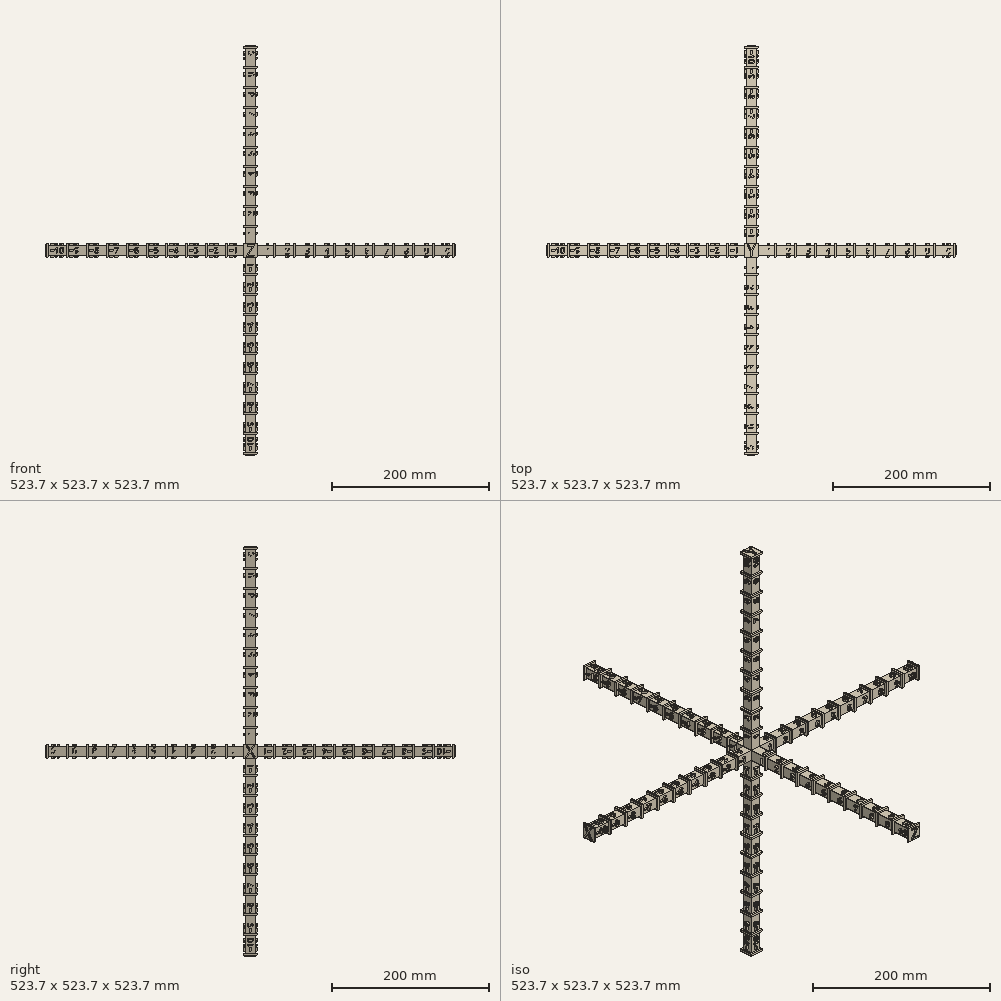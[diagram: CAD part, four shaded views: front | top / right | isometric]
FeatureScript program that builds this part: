
annotation { "Feature Type Name" : "Feature", "Feature Type Description" : "" }
export const myFeature = defineFeature(function(context is Context, id is Id, definition is map)
    precondition{}
    {
        {
            var Q0;
            Q0=qCreatedBy(makeId("Front.planeOp"),FACE);
            var sketch = newSketch(context, id + "F0", { "sketchPlane" : qUnion([Q0])});
            skLineSegment(sketch, "E0.bottom", {"start": v(-6.35, 260.35) * mm, "end": v(6.35, 260.35) * mm});
            skLineSegment(sketch, "E0.top", {"start": v(-6.35, -260.35) * mm, "end": v(6.35, -260.35) * mm});
            skLineSegment(sketch, "E0.left", {"start": v(-6.35, 260.35) * mm, "end": v(-6.35, -260.35) * mm});
            skLineSegment(sketch, "E0.right", {"start": v(6.35, 260.35) * mm, "end": v(6.35, -260.35) * mm});
            skPoint(sketch, "E0.middle", {"position": v(0, 0) * mm});
            skLineSegment(sketch, "E1.bottom", {"start": v(-260.35, 6.35) * mm, "end": v(260.35, 6.35) * mm});
            skLineSegment(sketch, "E1.top", {"start": v(-260.35, -6.35) * mm, "end": v(260.35, -6.35) * mm});
            skLineSegment(sketch, "E1.left", {"start": v(-260.35, 6.35) * mm, "end": v(-260.35, -6.35) * mm});
            skLineSegment(sketch, "E1.right", {"start": v(260.35, 6.35) * mm, "end": v(260.35, -6.35) * mm});
            skSolve(sketch);
        }
        {
            var Q0;
            Q0 = qSketchRegion(id + "F0", true);
            extrude(context, id + "F1", {"entities" : qUnion([Q0]), "endBound" : BoundingType.SYMMETRIC, "depth" : 12.7 * mm});
        }
        {
            var Q0;
            Q0=makeQuery(id+"F1.opExtrude","CAP_FACE",FACE,{"disambiguationData":[OSD([sQuery(id+"F0.wireOp",EDGE,"E0.bottom"),sQuery(id+"F0.wireOp",EDGE,"E0.top"),sQuery(id+"F0.wireOp",EDGE,"E0.left"),sQuery(id+"F0.wireOp",EDGE,"E0.right"),sQuery(id+"F0.wireOp",EDGE,"E1.bottom"),sQuery(id+"F0.wireOp",EDGE,"E1.top"),sQuery(id+"F0.wireOp",EDGE,"E1.left"),sQuery(id+"F0.wireOp",EDGE,"E1.right")])],"isStart":false});
            var sketch = newSketch(context, id + "F2", { "sketchPlane" : qUnion([Q0])});
            skLineSegment(sketch, "E2.bottom", {"start": v(-6.35, 6.35) * mm, "end": v(6.35, 6.35) * mm});
            skLineSegment(sketch, "E2.top", {"start": v(-6.35, -6.35) * mm, "end": v(6.35, -6.35) * mm});
            skLineSegment(sketch, "E2.left", {"start": v(-6.35, 6.35) * mm, "end": v(-6.35, -6.35) * mm});
            skLineSegment(sketch, "E2.right", {"start": v(6.35, 6.35) * mm, "end": v(6.35, -6.35) * mm});
            skSolve(sketch);
        }
        {
            var Q0;
            Q0 = qSketchRegion(id + "F2", true);
            extrude(context, id + "F3", {"entities" : qUnion([Q0]), "operationType" : NewBodyOperationType.ADD, "depth" : 254 * mm, "hasSecondDirection" : true, "secondDirectionOppositeDirection" : true, "secondDirectionDepth" : 266.7 * mm});
        }
        {
            var Q0;
            {var subQ0=sQuery(id+"F0.wireOp",EDGE,"E0.right");var subQ1=sQuery(id+"F0.wireOp",EDGE,"E0.top");var subQ2=sQuery(id+"F0.wireOp",EDGE,"E1.top");var subQ4=sQuery(id+"F0.wireOp",EDGE,"E0.bottom");var subQ5=sQuery(id+"F0.wireOp",EDGE,"E1.bottom");var subQ7=sQuery(id+"F0.wireOp",EDGE,"E1.right");var subQ8=makeQuery(id+"F1.opExtrude","CAP_FACE",FACE,{"disambiguationData":[OSD([subQ4,subQ1,sQuery(id+"F0.wireOp",EDGE,"E0.left"),subQ0,subQ5,subQ2,sQuery(id+"F0.wireOp",EDGE,"E1.left"),subQ7])],"isStart":false});Q0=makeQuery(id+"F3.boolean.opBoolean","SPLIT",FACE,{"disambiguationData":[TD([makeQuery(id+"F1.opExtrude","SWEPT_FACE",FACE,{"disambiguationData":[OSD([subQ7])]})])],"derivedFrom":subQ8});}
            var sketch = newSketch(context, id + "F4", { "sketchPlane" : qUnion([Q0])});
            skLineSegment(sketch, "E3.bottom", {"start": v(29.21, 6.35) * mm, "end": v(31.75, 6.35) * mm});
            skLineSegment(sketch, "E3.top", {"start": v(29.21, -6.35) * mm, "end": v(31.75, -6.35) * mm});
            skLineSegment(sketch, "E3.left", {"start": v(29.21, 6.35) * mm, "end": v(29.21, -6.35) * mm});
            skLineSegment(sketch, "E3.right", {"start": v(31.75, 6.35) * mm, "end": v(31.75, -6.35) * mm});
            skLineSegment(sketch, "E4.1.0.0", {"start": v(54.61, 6.35) * mm, "end": v(54.61, -6.35) * mm});
            skLineSegment(sketch, "E4.1.0.1", {"start": v(54.61, 6.35) * mm, "end": v(57.15, 6.35) * mm});
            skLineSegment(sketch, "E4.1.0.2", {"start": v(57.15, 6.35) * mm, "end": v(57.15, -6.35) * mm});
            skLineSegment(sketch, "E4.1.0.3", {"start": v(54.61, -6.35) * mm, "end": v(57.15, -6.35) * mm});
            skLineSegment(sketch, "E4.2.0.0", {"start": v(80.01, 6.35) * mm, "end": v(80.01, -6.35) * mm});
            skLineSegment(sketch, "E4.2.0.1", {"start": v(80.01, 6.35) * mm, "end": v(82.55, 6.35) * mm});
            skLineSegment(sketch, "E4.2.0.2", {"start": v(82.55, 6.35) * mm, "end": v(82.55, -6.35) * mm});
            skLineSegment(sketch, "E4.2.0.3", {"start": v(80.01, -6.35) * mm, "end": v(82.55, -6.35) * mm});
            skLineSegment(sketch, "E4.3.0.0", {"start": v(105.41, 6.35) * mm, "end": v(105.41, -6.35) * mm});
            skLineSegment(sketch, "E4.3.0.1", {"start": v(105.41, 6.35) * mm, "end": v(107.95, 6.35) * mm});
            skLineSegment(sketch, "E4.3.0.2", {"start": v(107.95, 6.35) * mm, "end": v(107.95, -6.35) * mm});
            skLineSegment(sketch, "E4.3.0.3", {"start": v(105.41, -6.35) * mm, "end": v(107.95, -6.35) * mm});
            skLineSegment(sketch, "E4.4.0.0", {"start": v(130.81, 6.35) * mm, "end": v(130.81, -6.35) * mm});
            skLineSegment(sketch, "E4.4.0.1", {"start": v(130.81, 6.35) * mm, "end": v(133.35, 6.35) * mm});
            skLineSegment(sketch, "E4.4.0.2", {"start": v(133.35, 6.35) * mm, "end": v(133.35, -6.35) * mm});
            skLineSegment(sketch, "E4.4.0.3", {"start": v(130.81, -6.35) * mm, "end": v(133.35, -6.35) * mm});
            skLineSegment(sketch, "E4.5.0.0", {"start": v(156.21, 6.35) * mm, "end": v(156.21, -6.35) * mm});
            skLineSegment(sketch, "E4.5.0.1", {"start": v(156.21, 6.35) * mm, "end": v(158.75, 6.35) * mm});
            skLineSegment(sketch, "E4.5.0.2", {"start": v(158.75, 6.35) * mm, "end": v(158.75, -6.35) * mm});
            skLineSegment(sketch, "E4.5.0.3", {"start": v(156.21, -6.35) * mm, "end": v(158.75, -6.35) * mm});
            skLineSegment(sketch, "E4.6.0.0", {"start": v(181.61, 6.35) * mm, "end": v(181.61, -6.35) * mm});
            skLineSegment(sketch, "E4.6.0.1", {"start": v(181.61, 6.35) * mm, "end": v(184.15, 6.35) * mm});
            skLineSegment(sketch, "E4.6.0.2", {"start": v(184.15, 6.35) * mm, "end": v(184.15, -6.35) * mm});
            skLineSegment(sketch, "E4.6.0.3", {"start": v(181.61, -6.35) * mm, "end": v(184.15, -6.35) * mm});
            skLineSegment(sketch, "E4.7.0.0", {"start": v(207.01, 6.35) * mm, "end": v(207.01, -6.35) * mm});
            skLineSegment(sketch, "E4.7.0.1", {"start": v(207.01, 6.35) * mm, "end": v(209.55, 6.35) * mm});
            skLineSegment(sketch, "E4.7.0.2", {"start": v(209.55, 6.35) * mm, "end": v(209.55, -6.35) * mm});
            skLineSegment(sketch, "E4.7.0.3", {"start": v(207.01, -6.35) * mm, "end": v(209.55, -6.35) * mm});
            skLineSegment(sketch, "E4.8.0.0", {"start": v(232.41, 6.35) * mm, "end": v(232.41, -6.35) * mm});
            skLineSegment(sketch, "E4.8.0.1", {"start": v(232.41, 6.35) * mm, "end": v(234.95, 6.35) * mm});
            skLineSegment(sketch, "E4.8.0.2", {"start": v(234.95, 6.35) * mm, "end": v(234.95, -6.35) * mm});
            skLineSegment(sketch, "E4.8.0.3", {"start": v(232.41, -6.35) * mm, "end": v(234.95, -6.35) * mm});
            skLineSegment(sketch, "E4.9.0.0", {"start": v(257.81, 6.35) * mm, "end": v(257.81, -6.35) * mm});
            skLineSegment(sketch, "E4.9.0.1", {"start": v(257.81, 6.35) * mm, "end": v(260.35, 6.35) * mm});
            skLineSegment(sketch, "E4.9.0.2", {"start": v(260.35, 6.35) * mm, "end": v(260.35, -6.35) * mm});
            skLineSegment(sketch, "E4.9.0.3", {"start": v(257.81, -6.35) * mm, "end": v(260.35, -6.35) * mm});
            skLineSegment(sketch, "E4.direction1", {"start": v(29.21, -6.35) * mm, "end": v(54.61, -6.35) * mm, "construction": true});
            skSolve(sketch);
        }
        {
            var Q0;
            Q0 = qSketchRegion(id + "F4", true);
            extrude(context, id + "F5", {"entities" : qUnion([Q0]), "depth" : 2.54 * mm});
        }
        {
            var Q0;
            {var subQ0=sQuery(id+"F0.wireOp",EDGE,"E1.bottom");Q0=makeQuery(id+"F5.boolean.opBoolean","MERGE",FACE,{"derivedFrom":[makeQuery(id+"F1.opExtrude","SWEPT_FACE",FACE,{"disambiguationData":[OSD([subQ0]),TDD([makeQuery(id+"F0.imprint","IMPRINT",EDGE,{"disambiguationData":[TD([[makeQuery(id+"F0.imprint","INTERSECT",VERTEX,{"derivedFrom":[subQ0,sQuery(id+"F0.wireOp",EDGE,"E1.right")]}),1.0]])],"derivedFrom":subQ0})])]}),makeQuery(id+"F5.opExtrude","SWEPT_FACE",FACE,{"disambiguationData":[OSD([sQuery(id+"F4.wireOp",EDGE,"E3.bottom")])]}),makeQuery(id+"F5.opExtrude","SWEPT_FACE",FACE,{"disambiguationData":[OSD([sQuery(id+"F4.wireOp",EDGE,"E4.1.0.1")])]}),makeQuery(id+"F5.opExtrude","SWEPT_FACE",FACE,{"disambiguationData":[OSD([sQuery(id+"F4.wireOp",EDGE,"E4.2.0.1")])]}),makeQuery(id+"F5.opExtrude","SWEPT_FACE",FACE,{"disambiguationData":[OSD([sQuery(id+"F4.wireOp",EDGE,"E4.3.0.1")])]}),makeQuery(id+"F5.opExtrude","SWEPT_FACE",FACE,{"disambiguationData":[OSD([sQuery(id+"F4.wireOp",EDGE,"E4.4.0.1")])]}),makeQuery(id+"F5.opExtrude","SWEPT_FACE",FACE,{"disambiguationData":[OSD([sQuery(id+"F4.wireOp",EDGE,"E4.5.0.1")])]}),makeQuery(id+"F5.opExtrude","SWEPT_FACE",FACE,{"disambiguationData":[OSD([sQuery(id+"F4.wireOp",EDGE,"E4.6.0.1")])]}),makeQuery(id+"F5.opExtrude","SWEPT_FACE",FACE,{"disambiguationData":[OSD([sQuery(id+"F4.wireOp",EDGE,"E4.7.0.1")])]}),makeQuery(id+"F5.opExtrude","SWEPT_FACE",FACE,{"disambiguationData":[OSD([sQuery(id+"F4.wireOp",EDGE,"E4.8.0.1")])]}),makeQuery(id+"F5.opExtrude","SWEPT_FACE",FACE,{"disambiguationData":[OSD([sQuery(id+"F4.wireOp",EDGE,"E4.9.0.1")])]})]});}
            var sketch = newSketch(context, id + "F6", { "sketchPlane" : qUnion([Q0])});
            skLineSegment(sketch, "E5.bottom", {"start": v(29.21, -8.9) * mm, "end": v(31.75, -8.9) * mm});
            skLineSegment(sketch, "E5.top", {"start": v(29.21, 6.35) * mm, "end": v(31.75, 6.35) * mm});
            skLineSegment(sketch, "E5.left", {"start": v(29.21, -8.9) * mm, "end": v(29.21, 6.35) * mm});
            skLineSegment(sketch, "E5.right", {"start": v(31.75, -8.9) * mm, "end": v(31.75, 6.35) * mm});
            skLineSegment(sketch, "E6.1.0.0", {"start": v(57.15, -8.9) * mm, "end": v(57.15, 6.35) * mm});
            skLineSegment(sketch, "E6.1.0.1", {"start": v(54.61, -8.9) * mm, "end": v(54.61, 6.35) * mm});
            skLineSegment(sketch, "E6.1.0.2", {"start": v(54.61, -8.9) * mm, "end": v(57.15, -8.9) * mm});
            skLineSegment(sketch, "E6.1.0.3", {"start": v(54.61, 6.35) * mm, "end": v(57.15, 6.35) * mm});
            skLineSegment(sketch, "E6.2.0.0", {"start": v(82.55, -8.9) * mm, "end": v(82.55, 6.35) * mm});
            skLineSegment(sketch, "E6.2.0.1", {"start": v(80.01, -8.9) * mm, "end": v(80.01, 6.35) * mm});
            skLineSegment(sketch, "E6.2.0.2", {"start": v(80.01, -8.9) * mm, "end": v(82.55, -8.9) * mm});
            skLineSegment(sketch, "E6.2.0.3", {"start": v(80.01, 6.35) * mm, "end": v(82.55, 6.35) * mm});
            skLineSegment(sketch, "E6.3.0.0", {"start": v(107.95, -8.9) * mm, "end": v(107.95, 6.35) * mm});
            skLineSegment(sketch, "E6.3.0.1", {"start": v(105.41, -8.9) * mm, "end": v(105.41, 6.35) * mm});
            skLineSegment(sketch, "E6.3.0.2", {"start": v(105.41, -8.9) * mm, "end": v(107.95, -8.9) * mm});
            skLineSegment(sketch, "E6.3.0.3", {"start": v(105.41, 6.35) * mm, "end": v(107.95, 6.35) * mm});
            skLineSegment(sketch, "E6.4.0.0", {"start": v(133.35, -8.9) * mm, "end": v(133.35, 6.35) * mm});
            skLineSegment(sketch, "E6.4.0.1", {"start": v(130.81, -8.9) * mm, "end": v(130.81, 6.35) * mm});
            skLineSegment(sketch, "E6.4.0.2", {"start": v(130.81, -8.9) * mm, "end": v(133.35, -8.9) * mm});
            skLineSegment(sketch, "E6.4.0.3", {"start": v(130.81, 6.35) * mm, "end": v(133.35, 6.35) * mm});
            skLineSegment(sketch, "E6.5.0.0", {"start": v(158.75, -8.9) * mm, "end": v(158.75, 6.35) * mm});
            skLineSegment(sketch, "E6.5.0.1", {"start": v(156.21, -8.9) * mm, "end": v(156.21, 6.35) * mm});
            skLineSegment(sketch, "E6.5.0.2", {"start": v(156.21, -8.9) * mm, "end": v(158.75, -8.9) * mm});
            skLineSegment(sketch, "E6.5.0.3", {"start": v(156.21, 6.35) * mm, "end": v(158.75, 6.35) * mm});
            skLineSegment(sketch, "E6.6.0.0", {"start": v(184.15, -8.9) * mm, "end": v(184.15, 6.35) * mm});
            skLineSegment(sketch, "E6.6.0.1", {"start": v(181.61, -8.9) * mm, "end": v(181.61, 6.35) * mm});
            skLineSegment(sketch, "E6.6.0.2", {"start": v(181.61, -8.9) * mm, "end": v(184.15, -8.9) * mm});
            skLineSegment(sketch, "E6.6.0.3", {"start": v(181.61, 6.35) * mm, "end": v(184.15, 6.35) * mm});
            skLineSegment(sketch, "E6.7.0.0", {"start": v(209.55, -8.9) * mm, "end": v(209.55, 6.35) * mm});
            skLineSegment(sketch, "E6.7.0.1", {"start": v(207.01, -8.9) * mm, "end": v(207.01, 6.35) * mm});
            skLineSegment(sketch, "E6.7.0.2", {"start": v(207.01, -8.9) * mm, "end": v(209.55, -8.9) * mm});
            skLineSegment(sketch, "E6.7.0.3", {"start": v(207.01, 6.35) * mm, "end": v(209.55, 6.35) * mm});
            skLineSegment(sketch, "E6.8.0.0", {"start": v(234.95, -8.9) * mm, "end": v(234.95, 6.35) * mm});
            skLineSegment(sketch, "E6.8.0.1", {"start": v(232.41, -8.9) * mm, "end": v(232.41, 6.35) * mm});
            skLineSegment(sketch, "E6.8.0.2", {"start": v(232.41, -8.9) * mm, "end": v(234.95, -8.9) * mm});
            skLineSegment(sketch, "E6.8.0.3", {"start": v(232.41, 6.35) * mm, "end": v(234.95, 6.35) * mm});
            skLineSegment(sketch, "E6.9.0.0", {"start": v(260.35, -8.9) * mm, "end": v(260.35, 6.35) * mm});
            skLineSegment(sketch, "E6.9.0.1", {"start": v(257.81, -8.9) * mm, "end": v(257.81, 6.35) * mm});
            skLineSegment(sketch, "E6.9.0.2", {"start": v(257.81, -8.9) * mm, "end": v(260.35, -8.9) * mm});
            skLineSegment(sketch, "E6.9.0.3", {"start": v(257.81, 6.35) * mm, "end": v(260.35, 6.35) * mm});
            skLineSegment(sketch, "E6.direction1", {"start": v(31.75, -8.9) * mm, "end": v(57.15, -8.9) * mm, "construction": true});
            skSolve(sketch);
        }
        {
            var Q0;
            Q0 = qSketchRegion(id + "F6", true);
            extrude(context, id + "F7", {"entities" : qUnion([Q0]), "depth" : 2.54 * mm});
        }
        {
            var Q0;
            {var subQ0=sQuery(id+"F0.wireOp",EDGE,"E1.right");var subQ1=sQuery(id+"F0.wireOp",EDGE,"E1.bottom");var subQ2=sQuery(id+"F0.wireOp",EDGE,"E0.right");var subQ4=sQuery(id+"F0.wireOp",EDGE,"E0.top");var subQ5=sQuery(id+"F0.wireOp",EDGE,"E1.top");var subQ7=sQuery(id+"F0.wireOp",EDGE,"E0.bottom");var subQ8=makeQuery(id+"F1.opExtrude","CAP_FACE",FACE,{"disambiguationData":[OSD([subQ7,subQ4,sQuery(id+"F0.wireOp",EDGE,"E0.left"),subQ2,subQ1,subQ5,sQuery(id+"F0.wireOp",EDGE,"E1.left"),subQ0])],"isStart":true});Q0=makeQuery(id+"F7.boolean.opBoolean","MERGE",FACE,{"derivedFrom":[makeQuery(id+"F3.boolean.opBoolean","SPLIT",FACE,{"disambiguationData":[TD([makeQuery(id+"F1.opExtrude","SWEPT_FACE",FACE,{"disambiguationData":[OSD([subQ0])]})])],"derivedFrom":subQ8}),makeQuery(id+"F7.opExtrude","SWEPT_FACE",FACE,{"disambiguationData":[OSD([sQuery(id+"F6.wireOp",EDGE,"E5.top")])]}),makeQuery(id+"F7.opExtrude","SWEPT_FACE",FACE,{"disambiguationData":[OSD([sQuery(id+"F6.wireOp",EDGE,"E6.1.0.3")])]}),makeQuery(id+"F7.opExtrude","SWEPT_FACE",FACE,{"disambiguationData":[OSD([sQuery(id+"F6.wireOp",EDGE,"E6.2.0.3")])]}),makeQuery(id+"F7.opExtrude","SWEPT_FACE",FACE,{"disambiguationData":[OSD([sQuery(id+"F6.wireOp",EDGE,"E6.3.0.3")])]}),makeQuery(id+"F7.opExtrude","SWEPT_FACE",FACE,{"disambiguationData":[OSD([sQuery(id+"F6.wireOp",EDGE,"E6.4.0.3")])]}),makeQuery(id+"F7.opExtrude","SWEPT_FACE",FACE,{"disambiguationData":[OSD([sQuery(id+"F6.wireOp",EDGE,"E6.5.0.3")])]}),makeQuery(id+"F7.opExtrude","SWEPT_FACE",FACE,{"disambiguationData":[OSD([sQuery(id+"F6.wireOp",EDGE,"E6.6.0.3")])]}),makeQuery(id+"F7.opExtrude","SWEPT_FACE",FACE,{"disambiguationData":[OSD([sQuery(id+"F6.wireOp",EDGE,"E6.7.0.3")])]}),makeQuery(id+"F7.opExtrude","SWEPT_FACE",FACE,{"disambiguationData":[OSD([sQuery(id+"F6.wireOp",EDGE,"E6.8.0.3")])]}),makeQuery(id+"F7.opExtrude","SWEPT_FACE",FACE,{"disambiguationData":[OSD([sQuery(id+"F6.wireOp",EDGE,"E6.9.0.3")])]})]});}
            var sketch = newSketch(context, id + "F8", { "sketchPlane" : qUnion([Q0])});
            skLineSegment(sketch, "E7.bottom", {"start": v(-29.21, 8.9) * mm, "end": v(-31.75, 8.9) * mm});
            skLineSegment(sketch, "E7.top", {"start": v(-29.21, -6.35) * mm, "end": v(-31.75, -6.35) * mm});
            skLineSegment(sketch, "E7.left", {"start": v(-29.21, 8.9) * mm, "end": v(-29.21, -6.35) * mm});
            skLineSegment(sketch, "E7.right", {"start": v(-31.75, 8.9) * mm, "end": v(-31.75, -6.35) * mm});
            skLineSegment(sketch, "E8.1.0.0", {"start": v(-54.61, 8.9) * mm, "end": v(-54.61, -6.35) * mm});
            skLineSegment(sketch, "E8.1.0.1", {"start": v(-54.61, -6.35) * mm, "end": v(-57.15, -6.35) * mm});
            skLineSegment(sketch, "E8.1.0.2", {"start": v(-57.15, 8.9) * mm, "end": v(-57.15, -6.35) * mm});
            skLineSegment(sketch, "E8.1.0.3", {"start": v(-54.61, 8.9) * mm, "end": v(-57.15, 8.9) * mm});
            skLineSegment(sketch, "E8.2.0.0", {"start": v(-80.01, 8.9) * mm, "end": v(-80.01, -6.35) * mm});
            skLineSegment(sketch, "E8.2.0.1", {"start": v(-80.01, -6.35) * mm, "end": v(-82.55, -6.35) * mm});
            skLineSegment(sketch, "E8.2.0.2", {"start": v(-82.55, 8.9) * mm, "end": v(-82.55, -6.35) * mm});
            skLineSegment(sketch, "E8.2.0.3", {"start": v(-80.01, 8.9) * mm, "end": v(-82.55, 8.9) * mm});
            skLineSegment(sketch, "E8.3.0.0", {"start": v(-105.41, 8.9) * mm, "end": v(-105.41, -6.35) * mm});
            skLineSegment(sketch, "E8.3.0.1", {"start": v(-105.41, -6.35) * mm, "end": v(-107.95, -6.35) * mm});
            skLineSegment(sketch, "E8.3.0.2", {"start": v(-107.95, 8.9) * mm, "end": v(-107.95, -6.35) * mm});
            skLineSegment(sketch, "E8.3.0.3", {"start": v(-105.41, 8.9) * mm, "end": v(-107.95, 8.9) * mm});
            skLineSegment(sketch, "E8.4.0.0", {"start": v(-130.81, 8.9) * mm, "end": v(-130.81, -6.35) * mm});
            skLineSegment(sketch, "E8.4.0.1", {"start": v(-130.81, -6.35) * mm, "end": v(-133.35, -6.35) * mm});
            skLineSegment(sketch, "E8.4.0.2", {"start": v(-133.35, 8.9) * mm, "end": v(-133.35, -6.35) * mm});
            skLineSegment(sketch, "E8.4.0.3", {"start": v(-130.81, 8.9) * mm, "end": v(-133.35, 8.9) * mm});
            skLineSegment(sketch, "E8.5.0.0", {"start": v(-156.21, 8.9) * mm, "end": v(-156.21, -6.35) * mm});
            skLineSegment(sketch, "E8.5.0.1", {"start": v(-156.21, -6.35) * mm, "end": v(-158.75, -6.35) * mm});
            skLineSegment(sketch, "E8.5.0.2", {"start": v(-158.75, 8.9) * mm, "end": v(-158.75, -6.35) * mm});
            skLineSegment(sketch, "E8.5.0.3", {"start": v(-156.21, 8.9) * mm, "end": v(-158.75, 8.9) * mm});
            skLineSegment(sketch, "E8.6.0.0", {"start": v(-181.61, 8.9) * mm, "end": v(-181.61, -6.35) * mm});
            skLineSegment(sketch, "E8.6.0.1", {"start": v(-181.61, -6.35) * mm, "end": v(-184.15, -6.35) * mm});
            skLineSegment(sketch, "E8.6.0.2", {"start": v(-184.15, 8.9) * mm, "end": v(-184.15, -6.35) * mm});
            skLineSegment(sketch, "E8.6.0.3", {"start": v(-181.61, 8.9) * mm, "end": v(-184.15, 8.9) * mm});
            skLineSegment(sketch, "E8.7.0.0", {"start": v(-207.01, 8.9) * mm, "end": v(-207.01, -6.35) * mm});
            skLineSegment(sketch, "E8.7.0.1", {"start": v(-207.01, -6.35) * mm, "end": v(-209.55, -6.35) * mm});
            skLineSegment(sketch, "E8.7.0.2", {"start": v(-209.55, 8.9) * mm, "end": v(-209.55, -6.35) * mm});
            skLineSegment(sketch, "E8.7.0.3", {"start": v(-207.01, 8.9) * mm, "end": v(-209.55, 8.9) * mm});
            skLineSegment(sketch, "E8.8.0.0", {"start": v(-232.41, 8.9) * mm, "end": v(-232.41, -6.35) * mm});
            skLineSegment(sketch, "E8.8.0.1", {"start": v(-232.41, -6.35) * mm, "end": v(-234.95, -6.35) * mm});
            skLineSegment(sketch, "E8.8.0.2", {"start": v(-234.95, 8.9) * mm, "end": v(-234.95, -6.35) * mm});
            skLineSegment(sketch, "E8.8.0.3", {"start": v(-232.41, 8.9) * mm, "end": v(-234.95, 8.9) * mm});
            skLineSegment(sketch, "E8.9.0.0", {"start": v(-257.81, 8.9) * mm, "end": v(-257.81, -6.35) * mm});
            skLineSegment(sketch, "E8.9.0.1", {"start": v(-257.81, -6.35) * mm, "end": v(-260.35, -6.35) * mm});
            skLineSegment(sketch, "E8.9.0.2", {"start": v(-260.35, 8.9) * mm, "end": v(-260.35, -6.35) * mm});
            skLineSegment(sketch, "E8.9.0.3", {"start": v(-257.81, 8.9) * mm, "end": v(-260.35, 8.9) * mm});
            skLineSegment(sketch, "E8.direction1", {"start": v(-29.21, -6.35) * mm, "end": v(-54.61, -6.35) * mm, "construction": true});
            skSolve(sketch);
        }
        {
            var Q0;
            Q0 = qSketchRegion(id + "F8", true);
            extrude(context, id + "F9", {"entities" : qUnion([Q0]), "depth" : 2.54 * mm});
        }
        {
            var Q0;
            {var subQ0=sQuery(id+"F0.wireOp",EDGE,"E1.top");Q0=makeQuery(id+"F9.boolean.opBoolean","MERGE",FACE,{"derivedFrom":[makeQuery(id+"F5.boolean.opBoolean","MERGE",FACE,{"derivedFrom":[makeQuery(id+"F1.opExtrude","SWEPT_FACE",FACE,{"disambiguationData":[OSD([subQ0]),TDD([makeQuery(id+"F0.imprint","IMPRINT",EDGE,{"disambiguationData":[TD([[makeQuery(id+"F0.imprint","INTERSECT",VERTEX,{"derivedFrom":[subQ0,sQuery(id+"F0.wireOp",EDGE,"E1.right")]}),1.0]])],"derivedFrom":subQ0})])]}),makeQuery(id+"F5.opExtrude","SWEPT_FACE",FACE,{"disambiguationData":[OSD([sQuery(id+"F4.wireOp",EDGE,"E3.top")])]}),makeQuery(id+"F5.opExtrude","SWEPT_FACE",FACE,{"disambiguationData":[OSD([sQuery(id+"F4.wireOp",EDGE,"E4.1.0.3")])]}),makeQuery(id+"F5.opExtrude","SWEPT_FACE",FACE,{"disambiguationData":[OSD([sQuery(id+"F4.wireOp",EDGE,"E4.2.0.3")])]}),makeQuery(id+"F5.opExtrude","SWEPT_FACE",FACE,{"disambiguationData":[OSD([sQuery(id+"F4.wireOp",EDGE,"E4.3.0.3")])]}),makeQuery(id+"F5.opExtrude","SWEPT_FACE",FACE,{"disambiguationData":[OSD([sQuery(id+"F4.wireOp",EDGE,"E4.4.0.3")])]}),makeQuery(id+"F5.opExtrude","SWEPT_FACE",FACE,{"disambiguationData":[OSD([sQuery(id+"F4.wireOp",EDGE,"E4.5.0.3")])]}),makeQuery(id+"F5.opExtrude","SWEPT_FACE",FACE,{"disambiguationData":[OSD([sQuery(id+"F4.wireOp",EDGE,"E4.6.0.3")])]}),makeQuery(id+"F5.opExtrude","SWEPT_FACE",FACE,{"disambiguationData":[OSD([sQuery(id+"F4.wireOp",EDGE,"E4.7.0.3")])]}),makeQuery(id+"F5.opExtrude","SWEPT_FACE",FACE,{"disambiguationData":[OSD([sQuery(id+"F4.wireOp",EDGE,"E4.8.0.3")])]}),makeQuery(id+"F5.opExtrude","SWEPT_FACE",FACE,{"disambiguationData":[OSD([sQuery(id+"F4.wireOp",EDGE,"E4.9.0.3")])]})]}),makeQuery(id+"F9.opExtrude","SWEPT_FACE",FACE,{"disambiguationData":[OSD([sQuery(id+"F8.wireOp",EDGE,"E7.top")])]}),makeQuery(id+"F9.opExtrude","SWEPT_FACE",FACE,{"disambiguationData":[OSD([sQuery(id+"F8.wireOp",EDGE,"E8.1.0.1")])]}),makeQuery(id+"F9.opExtrude","SWEPT_FACE",FACE,{"disambiguationData":[OSD([sQuery(id+"F8.wireOp",EDGE,"E8.2.0.1")])]}),makeQuery(id+"F9.opExtrude","SWEPT_FACE",FACE,{"disambiguationData":[OSD([sQuery(id+"F8.wireOp",EDGE,"E8.3.0.1")])]}),makeQuery(id+"F9.opExtrude","SWEPT_FACE",FACE,{"disambiguationData":[OSD([sQuery(id+"F8.wireOp",EDGE,"E8.4.0.1")])]}),makeQuery(id+"F9.opExtrude","SWEPT_FACE",FACE,{"disambiguationData":[OSD([sQuery(id+"F8.wireOp",EDGE,"E8.5.0.1")])]}),makeQuery(id+"F9.opExtrude","SWEPT_FACE",FACE,{"disambiguationData":[OSD([sQuery(id+"F8.wireOp",EDGE,"E8.6.0.1")])]}),makeQuery(id+"F9.opExtrude","SWEPT_FACE",FACE,{"disambiguationData":[OSD([sQuery(id+"F8.wireOp",EDGE,"E8.7.0.1")])]}),makeQuery(id+"F9.opExtrude","SWEPT_FACE",FACE,{"disambiguationData":[OSD([sQuery(id+"F8.wireOp",EDGE,"E8.8.0.1")])]}),makeQuery(id+"F9.opExtrude","SWEPT_FACE",FACE,{"disambiguationData":[OSD([sQuery(id+"F8.wireOp",EDGE,"E8.9.0.1")])]})]});}
            var sketch = newSketch(context, id + "F10", { "sketchPlane" : qUnion([Q0])});
            skLineSegment(sketch, "E9.bottom", {"start": v(29.21, -8.9) * mm, "end": v(31.75, -8.9) * mm});
            skLineSegment(sketch, "E9.top", {"start": v(29.21, 8.9) * mm, "end": v(31.75, 8.9) * mm});
            skLineSegment(sketch, "E9.left", {"start": v(29.21, -8.9) * mm, "end": v(29.21, 8.9) * mm});
            skLineSegment(sketch, "E9.right", {"start": v(31.75, -8.9) * mm, "end": v(31.75, 8.9) * mm});
            skLineSegment(sketch, "E10.1.0.0", {"start": v(54.61, -8.9) * mm, "end": v(54.61, 8.9) * mm});
            skLineSegment(sketch, "E10.1.0.1", {"start": v(54.61, 8.9) * mm, "end": v(57.15, 8.9) * mm});
            skLineSegment(sketch, "E10.1.0.2", {"start": v(57.15, -8.9) * mm, "end": v(57.15, 8.9) * mm});
            skLineSegment(sketch, "E10.1.0.3", {"start": v(54.61, -8.9) * mm, "end": v(57.15, -8.9) * mm});
            skLineSegment(sketch, "E10.2.0.0", {"start": v(80.01, -8.9) * mm, "end": v(80.01, 8.9) * mm});
            skLineSegment(sketch, "E10.2.0.1", {"start": v(80.01, 8.9) * mm, "end": v(82.55, 8.9) * mm});
            skLineSegment(sketch, "E10.2.0.2", {"start": v(82.55, -8.9) * mm, "end": v(82.55, 8.9) * mm});
            skLineSegment(sketch, "E10.2.0.3", {"start": v(80.01, -8.9) * mm, "end": v(82.55, -8.9) * mm});
            skLineSegment(sketch, "E10.3.0.0", {"start": v(105.41, -8.9) * mm, "end": v(105.41, 8.9) * mm});
            skLineSegment(sketch, "E10.3.0.1", {"start": v(105.41, 8.9) * mm, "end": v(107.95, 8.9) * mm});
            skLineSegment(sketch, "E10.3.0.2", {"start": v(107.95, -8.9) * mm, "end": v(107.95, 8.9) * mm});
            skLineSegment(sketch, "E10.3.0.3", {"start": v(105.41, -8.9) * mm, "end": v(107.95, -8.9) * mm});
            skLineSegment(sketch, "E10.4.0.0", {"start": v(130.81, -8.9) * mm, "end": v(130.81, 8.9) * mm});
            skLineSegment(sketch, "E10.4.0.1", {"start": v(130.81, 8.9) * mm, "end": v(133.35, 8.9) * mm});
            skLineSegment(sketch, "E10.4.0.2", {"start": v(133.35, -8.9) * mm, "end": v(133.35, 8.9) * mm});
            skLineSegment(sketch, "E10.4.0.3", {"start": v(130.81, -8.9) * mm, "end": v(133.35, -8.9) * mm});
            skLineSegment(sketch, "E10.5.0.0", {"start": v(156.21, -8.9) * mm, "end": v(156.21, 8.9) * mm});
            skLineSegment(sketch, "E10.5.0.1", {"start": v(156.21, 8.9) * mm, "end": v(158.75, 8.9) * mm});
            skLineSegment(sketch, "E10.5.0.2", {"start": v(158.75, -8.9) * mm, "end": v(158.75, 8.9) * mm});
            skLineSegment(sketch, "E10.5.0.3", {"start": v(156.21, -8.9) * mm, "end": v(158.75, -8.9) * mm});
            skLineSegment(sketch, "E10.6.0.0", {"start": v(181.61, -8.9) * mm, "end": v(181.61, 8.9) * mm});
            skLineSegment(sketch, "E10.6.0.1", {"start": v(181.61, 8.9) * mm, "end": v(184.15, 8.9) * mm});
            skLineSegment(sketch, "E10.6.0.2", {"start": v(184.15, -8.9) * mm, "end": v(184.15, 8.9) * mm});
            skLineSegment(sketch, "E10.6.0.3", {"start": v(181.61, -8.9) * mm, "end": v(184.15, -8.9) * mm});
            skLineSegment(sketch, "E10.7.0.0", {"start": v(207.01, -8.9) * mm, "end": v(207.01, 8.9) * mm});
            skLineSegment(sketch, "E10.7.0.1", {"start": v(207.01, 8.9) * mm, "end": v(209.55, 8.9) * mm});
            skLineSegment(sketch, "E10.7.0.2", {"start": v(209.55, -8.9) * mm, "end": v(209.55, 8.9) * mm});
            skLineSegment(sketch, "E10.7.0.3", {"start": v(207.01, -8.9) * mm, "end": v(209.55, -8.9) * mm});
            skLineSegment(sketch, "E10.8.0.0", {"start": v(232.41, -8.9) * mm, "end": v(232.41, 8.9) * mm});
            skLineSegment(sketch, "E10.8.0.1", {"start": v(232.41, 8.9) * mm, "end": v(234.95, 8.9) * mm});
            skLineSegment(sketch, "E10.8.0.2", {"start": v(234.95, -8.9) * mm, "end": v(234.95, 8.9) * mm});
            skLineSegment(sketch, "E10.8.0.3", {"start": v(232.41, -8.9) * mm, "end": v(234.95, -8.9) * mm});
            skLineSegment(sketch, "E10.9.0.0", {"start": v(257.81, -8.9) * mm, "end": v(257.81, 8.9) * mm});
            skLineSegment(sketch, "E10.9.0.1", {"start": v(257.81, 8.9) * mm, "end": v(260.35, 8.9) * mm});
            skLineSegment(sketch, "E10.9.0.2", {"start": v(260.35, -8.9) * mm, "end": v(260.35, 8.9) * mm});
            skLineSegment(sketch, "E10.9.0.3", {"start": v(257.81, -8.9) * mm, "end": v(260.35, -8.9) * mm});
            skLineSegment(sketch, "E10.direction1", {"start": v(29.21, -8.9) * mm, "end": v(54.61, -8.9) * mm, "construction": true});
            skSolve(sketch);
        }
        {
            var Q0;
            Q0 = qSketchRegion(id + "F10", true);
            extrude(context, id + "F11", {"entities" : qUnion([Q0]), "depth" : 2.54 * mm});
        }
        {
            var Q0;
            Q0=qCreatedBy(makeId("Front.planeOp"),FACE);
            var sketch = newSketch(context, id + "F12", { "sketchPlane" : qUnion([Q0])});
            skLineSegment(sketch, "E11", {"start": v(0, 259.8) * mm, "end": v(0, -262.33) * mm});
            skSolve(sketch);
        }
        {
            var Q0;
            Q0=qCreatedBy(makeId("Top.planeOp"),FACE);
            var sketch = newSketch(context, id + "F13", { "sketchPlane" : qUnion([Q0])});
            skLineSegment(sketch, "E12", {"start": v(-260.75, 0) * mm, "end": v(260.1, 0) * mm});
            skSolve(sketch);
        }
        {
            var Q0;
            Q0=qCreatedBy(makeId("Top.planeOp"),FACE);
            var sketch = newSketch(context, id + "F14", { "sketchPlane" : qUnion([Q0])});
            skLineSegment(sketch, "E13", {"start": v(0, -260.56) * mm, "end": v(0, 260.69) * mm});
            skSolve(sketch);
        }
        {
            var Q0;
            Q0=makeQuery(id+"F5.opExtrude","SWEPT_BODY",BODY,{"disambiguationData":[OSD([sQuery(id+"F4.wireOp",EDGE,"E3.bottom"),sQuery(id+"F4.wireOp",EDGE,"E3.top"),sQuery(id+"F4.wireOp",EDGE,"E3.left"),sQuery(id+"F4.wireOp",EDGE,"E3.right")])]});
            var Q1;
            Q1=makeQuery(id+"F5.opExtrude","SWEPT_BODY",BODY,{"disambiguationData":[OSD([sQuery(id+"F4.wireOp",EDGE,"E4.1.0.0"),sQuery(id+"F4.wireOp",EDGE,"E4.1.0.1"),sQuery(id+"F4.wireOp",EDGE,"E4.1.0.2"),sQuery(id+"F4.wireOp",EDGE,"E4.1.0.3")])]});
            var Q2;
            Q2=makeQuery(id+"F5.opExtrude","SWEPT_BODY",BODY,{"disambiguationData":[OSD([sQuery(id+"F4.wireOp",EDGE,"E4.2.0.0"),sQuery(id+"F4.wireOp",EDGE,"E4.2.0.1"),sQuery(id+"F4.wireOp",EDGE,"E4.2.0.2"),sQuery(id+"F4.wireOp",EDGE,"E4.2.0.3")])]});
            var Q3;
            Q3=makeQuery(id+"F5.opExtrude","SWEPT_BODY",BODY,{"disambiguationData":[OSD([sQuery(id+"F4.wireOp",EDGE,"E4.3.0.0"),sQuery(id+"F4.wireOp",EDGE,"E4.3.0.1"),sQuery(id+"F4.wireOp",EDGE,"E4.3.0.2"),sQuery(id+"F4.wireOp",EDGE,"E4.3.0.3")])]});
            var Q4;
            Q4=makeQuery(id+"F5.opExtrude","SWEPT_BODY",BODY,{"disambiguationData":[OSD([sQuery(id+"F4.wireOp",EDGE,"E4.4.0.0"),sQuery(id+"F4.wireOp",EDGE,"E4.4.0.1"),sQuery(id+"F4.wireOp",EDGE,"E4.4.0.2"),sQuery(id+"F4.wireOp",EDGE,"E4.4.0.3")])]});
            var Q5;
            Q5=makeQuery(id+"F5.opExtrude","SWEPT_BODY",BODY,{"disambiguationData":[OSD([sQuery(id+"F4.wireOp",EDGE,"E4.5.0.0"),sQuery(id+"F4.wireOp",EDGE,"E4.5.0.1"),sQuery(id+"F4.wireOp",EDGE,"E4.5.0.2"),sQuery(id+"F4.wireOp",EDGE,"E4.5.0.3")])]});
            var Q6;
            Q6=makeQuery(id+"F5.opExtrude","SWEPT_BODY",BODY,{"disambiguationData":[OSD([sQuery(id+"F4.wireOp",EDGE,"E4.6.0.0"),sQuery(id+"F4.wireOp",EDGE,"E4.6.0.1"),sQuery(id+"F4.wireOp",EDGE,"E4.6.0.2"),sQuery(id+"F4.wireOp",EDGE,"E4.6.0.3")])]});
            var Q7;
            Q7=makeQuery(id+"F5.opExtrude","SWEPT_BODY",BODY,{"disambiguationData":[OSD([sQuery(id+"F4.wireOp",EDGE,"E4.7.0.0"),sQuery(id+"F4.wireOp",EDGE,"E4.7.0.1"),sQuery(id+"F4.wireOp",EDGE,"E4.7.0.2"),sQuery(id+"F4.wireOp",EDGE,"E4.7.0.3")])]});
            var Q8;
            Q8=makeQuery(id+"F5.opExtrude","SWEPT_BODY",BODY,{"disambiguationData":[OSD([sQuery(id+"F4.wireOp",EDGE,"E4.8.0.0"),sQuery(id+"F4.wireOp",EDGE,"E4.8.0.1"),sQuery(id+"F4.wireOp",EDGE,"E4.8.0.2"),sQuery(id+"F4.wireOp",EDGE,"E4.8.0.3")])]});
            var Q9;
            Q9=makeQuery(id+"F5.opExtrude","SWEPT_BODY",BODY,{"disambiguationData":[OSD([sQuery(id+"F4.wireOp",EDGE,"E4.9.0.0"),sQuery(id+"F4.wireOp",EDGE,"E4.9.0.1"),sQuery(id+"F4.wireOp",EDGE,"E4.9.0.2"),sQuery(id+"F4.wireOp",EDGE,"E4.9.0.3")])]});
            var Q10;
            Q10=makeQuery(id+"F7.opExtrude","SWEPT_BODY",BODY,{"disambiguationData":[OSD([sQuery(id+"F6.wireOp",EDGE,"E5.bottom"),sQuery(id+"F6.wireOp",EDGE,"E5.top"),sQuery(id+"F6.wireOp",EDGE,"E5.left"),sQuery(id+"F6.wireOp",EDGE,"E5.right")])]});
            var Q11;
            Q11=makeQuery(id+"F7.opExtrude","SWEPT_BODY",BODY,{"disambiguationData":[OSD([sQuery(id+"F6.wireOp",EDGE,"E6.1.0.0"),sQuery(id+"F6.wireOp",EDGE,"E6.1.0.1"),sQuery(id+"F6.wireOp",EDGE,"E6.1.0.2"),sQuery(id+"F6.wireOp",EDGE,"E6.1.0.3")])]});
            var Q12;
            Q12=makeQuery(id+"F7.opExtrude","SWEPT_BODY",BODY,{"disambiguationData":[OSD([sQuery(id+"F6.wireOp",EDGE,"E6.2.0.0"),sQuery(id+"F6.wireOp",EDGE,"E6.2.0.1"),sQuery(id+"F6.wireOp",EDGE,"E6.2.0.2"),sQuery(id+"F6.wireOp",EDGE,"E6.2.0.3")])]});
            var Q13;
            Q13=makeQuery(id+"F7.opExtrude","SWEPT_BODY",BODY,{"disambiguationData":[OSD([sQuery(id+"F6.wireOp",EDGE,"E6.3.0.0"),sQuery(id+"F6.wireOp",EDGE,"E6.3.0.1"),sQuery(id+"F6.wireOp",EDGE,"E6.3.0.2"),sQuery(id+"F6.wireOp",EDGE,"E6.3.0.3")])]});
            var Q14;
            Q14=makeQuery(id+"F7.opExtrude","SWEPT_BODY",BODY,{"disambiguationData":[OSD([sQuery(id+"F6.wireOp",EDGE,"E6.4.0.0"),sQuery(id+"F6.wireOp",EDGE,"E6.4.0.1"),sQuery(id+"F6.wireOp",EDGE,"E6.4.0.2"),sQuery(id+"F6.wireOp",EDGE,"E6.4.0.3")])]});
            var Q15;
            Q15=makeQuery(id+"F7.opExtrude","SWEPT_BODY",BODY,{"disambiguationData":[OSD([sQuery(id+"F6.wireOp",EDGE,"E6.5.0.0"),sQuery(id+"F6.wireOp",EDGE,"E6.5.0.1"),sQuery(id+"F6.wireOp",EDGE,"E6.5.0.2"),sQuery(id+"F6.wireOp",EDGE,"E6.5.0.3")])]});
            var Q16;
            Q16=makeQuery(id+"F7.opExtrude","SWEPT_BODY",BODY,{"disambiguationData":[OSD([sQuery(id+"F6.wireOp",EDGE,"E6.6.0.0"),sQuery(id+"F6.wireOp",EDGE,"E6.6.0.1"),sQuery(id+"F6.wireOp",EDGE,"E6.6.0.2"),sQuery(id+"F6.wireOp",EDGE,"E6.6.0.3")])]});
            var Q17;
            Q17=makeQuery(id+"F7.opExtrude","SWEPT_BODY",BODY,{"disambiguationData":[OSD([sQuery(id+"F6.wireOp",EDGE,"E6.7.0.0"),sQuery(id+"F6.wireOp",EDGE,"E6.7.0.1"),sQuery(id+"F6.wireOp",EDGE,"E6.7.0.2"),sQuery(id+"F6.wireOp",EDGE,"E6.7.0.3")])]});
            var Q18;
            Q18=makeQuery(id+"F7.opExtrude","SWEPT_BODY",BODY,{"disambiguationData":[OSD([sQuery(id+"F6.wireOp",EDGE,"E6.8.0.0"),sQuery(id+"F6.wireOp",EDGE,"E6.8.0.1"),sQuery(id+"F6.wireOp",EDGE,"E6.8.0.2"),sQuery(id+"F6.wireOp",EDGE,"E6.8.0.3")])]});
            var Q19;
            Q19=makeQuery(id+"F7.opExtrude","SWEPT_BODY",BODY,{"disambiguationData":[OSD([sQuery(id+"F6.wireOp",EDGE,"E6.9.0.0"),sQuery(id+"F6.wireOp",EDGE,"E6.9.0.1"),sQuery(id+"F6.wireOp",EDGE,"E6.9.0.2"),sQuery(id+"F6.wireOp",EDGE,"E6.9.0.3")])]});
            var Q20;
            Q20=makeQuery(id+"F9.opExtrude","SWEPT_BODY",BODY,{"disambiguationData":[OSD([sQuery(id+"F8.wireOp",EDGE,"E7.bottom"),sQuery(id+"F8.wireOp",EDGE,"E7.top"),sQuery(id+"F8.wireOp",EDGE,"E7.left"),sQuery(id+"F8.wireOp",EDGE,"E7.right")])]});
            var Q21;
            Q21=makeQuery(id+"F9.opExtrude","SWEPT_BODY",BODY,{"disambiguationData":[OSD([sQuery(id+"F8.wireOp",EDGE,"E8.1.0.0"),sQuery(id+"F8.wireOp",EDGE,"E8.1.0.1"),sQuery(id+"F8.wireOp",EDGE,"E8.1.0.2"),sQuery(id+"F8.wireOp",EDGE,"E8.1.0.3")])]});
            var Q22;
            Q22=makeQuery(id+"F9.opExtrude","SWEPT_BODY",BODY,{"disambiguationData":[OSD([sQuery(id+"F8.wireOp",EDGE,"E8.2.0.0"),sQuery(id+"F8.wireOp",EDGE,"E8.2.0.1"),sQuery(id+"F8.wireOp",EDGE,"E8.2.0.2"),sQuery(id+"F8.wireOp",EDGE,"E8.2.0.3")])]});
            var Q23;
            Q23=makeQuery(id+"F9.opExtrude","SWEPT_BODY",BODY,{"disambiguationData":[OSD([sQuery(id+"F8.wireOp",EDGE,"E8.3.0.0"),sQuery(id+"F8.wireOp",EDGE,"E8.3.0.1"),sQuery(id+"F8.wireOp",EDGE,"E8.3.0.2"),sQuery(id+"F8.wireOp",EDGE,"E8.3.0.3")])]});
            var Q24;
            Q24=makeQuery(id+"F9.opExtrude","SWEPT_BODY",BODY,{"disambiguationData":[OSD([sQuery(id+"F8.wireOp",EDGE,"E8.4.0.0"),sQuery(id+"F8.wireOp",EDGE,"E8.4.0.1"),sQuery(id+"F8.wireOp",EDGE,"E8.4.0.2"),sQuery(id+"F8.wireOp",EDGE,"E8.4.0.3")])]});
            var Q25;
            Q25=makeQuery(id+"F9.opExtrude","SWEPT_BODY",BODY,{"disambiguationData":[OSD([sQuery(id+"F8.wireOp",EDGE,"E8.5.0.0"),sQuery(id+"F8.wireOp",EDGE,"E8.5.0.1"),sQuery(id+"F8.wireOp",EDGE,"E8.5.0.2"),sQuery(id+"F8.wireOp",EDGE,"E8.5.0.3")])]});
            var Q26;
            Q26=makeQuery(id+"F9.opExtrude","SWEPT_BODY",BODY,{"disambiguationData":[OSD([sQuery(id+"F8.wireOp",EDGE,"E8.6.0.0"),sQuery(id+"F8.wireOp",EDGE,"E8.6.0.1"),sQuery(id+"F8.wireOp",EDGE,"E8.6.0.2"),sQuery(id+"F8.wireOp",EDGE,"E8.6.0.3")])]});
            var Q27;
            Q27=makeQuery(id+"F9.opExtrude","SWEPT_BODY",BODY,{"disambiguationData":[OSD([sQuery(id+"F8.wireOp",EDGE,"E8.7.0.0"),sQuery(id+"F8.wireOp",EDGE,"E8.7.0.1"),sQuery(id+"F8.wireOp",EDGE,"E8.7.0.2"),sQuery(id+"F8.wireOp",EDGE,"E8.7.0.3")])]});
            var Q28;
            Q28=makeQuery(id+"F9.opExtrude","SWEPT_BODY",BODY,{"disambiguationData":[OSD([sQuery(id+"F8.wireOp",EDGE,"E8.8.0.0"),sQuery(id+"F8.wireOp",EDGE,"E8.8.0.1"),sQuery(id+"F8.wireOp",EDGE,"E8.8.0.2"),sQuery(id+"F8.wireOp",EDGE,"E8.8.0.3")])]});
            var Q29;
            Q29=makeQuery(id+"F9.opExtrude","SWEPT_BODY",BODY,{"disambiguationData":[OSD([sQuery(id+"F8.wireOp",EDGE,"E8.9.0.0"),sQuery(id+"F8.wireOp",EDGE,"E8.9.0.1"),sQuery(id+"F8.wireOp",EDGE,"E8.9.0.2"),sQuery(id+"F8.wireOp",EDGE,"E8.9.0.3")])]});
            var Q30;
            Q30=makeQuery(id+"F11.opExtrude","SWEPT_BODY",BODY,{"disambiguationData":[OSD([sQuery(id+"F10.wireOp",EDGE,"E9.bottom"),sQuery(id+"F10.wireOp",EDGE,"E9.top"),sQuery(id+"F10.wireOp",EDGE,"E9.left"),sQuery(id+"F10.wireOp",EDGE,"E9.right")])]});
            var Q31;
            Q31=makeQuery(id+"F11.opExtrude","SWEPT_BODY",BODY,{"disambiguationData":[OSD([sQuery(id+"F10.wireOp",EDGE,"E10.1.0.0"),sQuery(id+"F10.wireOp",EDGE,"E10.1.0.1"),sQuery(id+"F10.wireOp",EDGE,"E10.1.0.2"),sQuery(id+"F10.wireOp",EDGE,"E10.1.0.3")])]});
            var Q32;
            Q32=makeQuery(id+"F11.opExtrude","SWEPT_BODY",BODY,{"disambiguationData":[OSD([sQuery(id+"F10.wireOp",EDGE,"E10.2.0.0"),sQuery(id+"F10.wireOp",EDGE,"E10.2.0.1"),sQuery(id+"F10.wireOp",EDGE,"E10.2.0.2"),sQuery(id+"F10.wireOp",EDGE,"E10.2.0.3")])]});
            var Q33;
            Q33=makeQuery(id+"F11.opExtrude","SWEPT_BODY",BODY,{"disambiguationData":[OSD([sQuery(id+"F10.wireOp",EDGE,"E10.3.0.0"),sQuery(id+"F10.wireOp",EDGE,"E10.3.0.1"),sQuery(id+"F10.wireOp",EDGE,"E10.3.0.2"),sQuery(id+"F10.wireOp",EDGE,"E10.3.0.3")])]});
            var Q34;
            Q34=makeQuery(id+"F11.opExtrude","SWEPT_BODY",BODY,{"disambiguationData":[OSD([sQuery(id+"F10.wireOp",EDGE,"E10.4.0.0"),sQuery(id+"F10.wireOp",EDGE,"E10.4.0.1"),sQuery(id+"F10.wireOp",EDGE,"E10.4.0.2"),sQuery(id+"F10.wireOp",EDGE,"E10.4.0.3")])]});
            var Q35;
            Q35=makeQuery(id+"F11.opExtrude","SWEPT_BODY",BODY,{"disambiguationData":[OSD([sQuery(id+"F10.wireOp",EDGE,"E10.5.0.0"),sQuery(id+"F10.wireOp",EDGE,"E10.5.0.1"),sQuery(id+"F10.wireOp",EDGE,"E10.5.0.2"),sQuery(id+"F10.wireOp",EDGE,"E10.5.0.3")])]});
            var Q36;
            Q36=makeQuery(id+"F11.opExtrude","SWEPT_BODY",BODY,{"disambiguationData":[OSD([sQuery(id+"F10.wireOp",EDGE,"E10.6.0.0"),sQuery(id+"F10.wireOp",EDGE,"E10.6.0.1"),sQuery(id+"F10.wireOp",EDGE,"E10.6.0.2"),sQuery(id+"F10.wireOp",EDGE,"E10.6.0.3")])]});
            var Q37;
            Q37=makeQuery(id+"F11.opExtrude","SWEPT_BODY",BODY,{"disambiguationData":[OSD([sQuery(id+"F10.wireOp",EDGE,"E10.7.0.0"),sQuery(id+"F10.wireOp",EDGE,"E10.7.0.1"),sQuery(id+"F10.wireOp",EDGE,"E10.7.0.2"),sQuery(id+"F10.wireOp",EDGE,"E10.7.0.3")])]});
            var Q38;
            Q38=makeQuery(id+"F11.opExtrude","SWEPT_BODY",BODY,{"disambiguationData":[OSD([sQuery(id+"F10.wireOp",EDGE,"E10.8.0.0"),sQuery(id+"F10.wireOp",EDGE,"E10.8.0.1"),sQuery(id+"F10.wireOp",EDGE,"E10.8.0.2"),sQuery(id+"F10.wireOp",EDGE,"E10.8.0.3")])]});
            var Q39;
            Q39=makeQuery(id+"F11.opExtrude","SWEPT_BODY",BODY,{"disambiguationData":[OSD([sQuery(id+"F10.wireOp",EDGE,"E10.9.0.0"),sQuery(id+"F10.wireOp",EDGE,"E10.9.0.1"),sQuery(id+"F10.wireOp",EDGE,"E10.9.0.2"),sQuery(id+"F10.wireOp",EDGE,"E10.9.0.3")])]});
            booleanBodies(context, id + "F15", {"operationType" : BooleanOperationType.UNION, "tools" : qUnion([Q0, Q1, Q2, Q3, Q4, Q5, Q6, Q7, Q8, Q9, Q10, Q11, Q12, Q13, Q14, Q15, Q16, Q17, Q18, Q19, Q20, Q21, Q22, Q23, Q24, Q25, Q26, Q27, Q28, Q29, Q30, Q31, Q32, Q33, Q34, Q35, Q36, Q37, Q38, Q39])});
        }
        {
            var Q0;
            Q0=makeQuery(id+"F5.opExtrude","SWEPT_BODY",BODY,{"disambiguationData":[OSD([sQuery(id+"F4.wireOp",EDGE,"E3.bottom"),sQuery(id+"F4.wireOp",EDGE,"E3.top"),sQuery(id+"F4.wireOp",EDGE,"E3.left"),sQuery(id+"F4.wireOp",EDGE,"E3.right")])]});
            var Q1;
            Q1=makeQuery(id+"F5.opExtrude","SWEPT_BODY",BODY,{"disambiguationData":[OSD([sQuery(id+"F4.wireOp",EDGE,"E4.1.0.0"),sQuery(id+"F4.wireOp",EDGE,"E4.1.0.1"),sQuery(id+"F4.wireOp",EDGE,"E4.1.0.2"),sQuery(id+"F4.wireOp",EDGE,"E4.1.0.3")])]});
            var Q2;
            Q2=makeQuery(id+"F5.opExtrude","SWEPT_BODY",BODY,{"disambiguationData":[OSD([sQuery(id+"F4.wireOp",EDGE,"E4.2.0.0"),sQuery(id+"F4.wireOp",EDGE,"E4.2.0.1"),sQuery(id+"F4.wireOp",EDGE,"E4.2.0.2"),sQuery(id+"F4.wireOp",EDGE,"E4.2.0.3")])]});
            var Q3;
            Q3=makeQuery(id+"F5.opExtrude","SWEPT_BODY",BODY,{"disambiguationData":[OSD([sQuery(id+"F4.wireOp",EDGE,"E4.3.0.0"),sQuery(id+"F4.wireOp",EDGE,"E4.3.0.1"),sQuery(id+"F4.wireOp",EDGE,"E4.3.0.2"),sQuery(id+"F4.wireOp",EDGE,"E4.3.0.3")])]});
            var Q4;
            Q4=makeQuery(id+"F5.opExtrude","SWEPT_BODY",BODY,{"disambiguationData":[OSD([sQuery(id+"F4.wireOp",EDGE,"E4.4.0.0"),sQuery(id+"F4.wireOp",EDGE,"E4.4.0.1"),sQuery(id+"F4.wireOp",EDGE,"E4.4.0.2"),sQuery(id+"F4.wireOp",EDGE,"E4.4.0.3")])]});
            var Q5;
            Q5=makeQuery(id+"F5.opExtrude","SWEPT_BODY",BODY,{"disambiguationData":[OSD([sQuery(id+"F4.wireOp",EDGE,"E4.5.0.0"),sQuery(id+"F4.wireOp",EDGE,"E4.5.0.1"),sQuery(id+"F4.wireOp",EDGE,"E4.5.0.2"),sQuery(id+"F4.wireOp",EDGE,"E4.5.0.3")])]});
            var Q6;
            Q6=makeQuery(id+"F5.opExtrude","SWEPT_BODY",BODY,{"disambiguationData":[OSD([sQuery(id+"F4.wireOp",EDGE,"E4.6.0.0"),sQuery(id+"F4.wireOp",EDGE,"E4.6.0.1"),sQuery(id+"F4.wireOp",EDGE,"E4.6.0.2"),sQuery(id+"F4.wireOp",EDGE,"E4.6.0.3")])]});
            var Q7;
            Q7=makeQuery(id+"F5.opExtrude","SWEPT_BODY",BODY,{"disambiguationData":[OSD([sQuery(id+"F4.wireOp",EDGE,"E4.7.0.0"),sQuery(id+"F4.wireOp",EDGE,"E4.7.0.1"),sQuery(id+"F4.wireOp",EDGE,"E4.7.0.2"),sQuery(id+"F4.wireOp",EDGE,"E4.7.0.3")])]});
            var Q8;
            Q8=makeQuery(id+"F5.opExtrude","SWEPT_BODY",BODY,{"disambiguationData":[OSD([sQuery(id+"F4.wireOp",EDGE,"E4.8.0.0"),sQuery(id+"F4.wireOp",EDGE,"E4.8.0.1"),sQuery(id+"F4.wireOp",EDGE,"E4.8.0.2"),sQuery(id+"F4.wireOp",EDGE,"E4.8.0.3")])]});
            var Q9;
            Q9=makeQuery(id+"F5.opExtrude","SWEPT_BODY",BODY,{"disambiguationData":[OSD([sQuery(id+"F4.wireOp",EDGE,"E4.9.0.0"),sQuery(id+"F4.wireOp",EDGE,"E4.9.0.1"),sQuery(id+"F4.wireOp",EDGE,"E4.9.0.2"),sQuery(id+"F4.wireOp",EDGE,"E4.9.0.3")])]});
            var Q10;
            Q10=sQuery(id+"F12.wireOp",EDGE,"E11");
            circularPattern(context, id + "F16", {"entities" : qUnion([Q0, Q1, Q2, Q3, Q4, Q5, Q6, Q7, Q8, Q9]), "axis" : qUnion([Q10]), "angle" : 360 * degree, "instanceCount" : 4, "equalSpace" : true});
        }
        {
            var Q0;
            Q0=makeQuery(id+"F5.opExtrude","SWEPT_BODY",BODY,{"disambiguationData":[OSD([sQuery(id+"F4.wireOp",EDGE,"E3.bottom"),sQuery(id+"F4.wireOp",EDGE,"E3.top"),sQuery(id+"F4.wireOp",EDGE,"E3.left"),sQuery(id+"F4.wireOp",EDGE,"E3.right")])]});
            var Q1;
            Q1=makeQuery(id+"F5.opExtrude","SWEPT_BODY",BODY,{"disambiguationData":[OSD([sQuery(id+"F4.wireOp",EDGE,"E4.1.0.0"),sQuery(id+"F4.wireOp",EDGE,"E4.1.0.1"),sQuery(id+"F4.wireOp",EDGE,"E4.1.0.2"),sQuery(id+"F4.wireOp",EDGE,"E4.1.0.3")])]});
            var Q2;
            Q2=makeQuery(id+"F5.opExtrude","SWEPT_BODY",BODY,{"disambiguationData":[OSD([sQuery(id+"F4.wireOp",EDGE,"E4.2.0.0"),sQuery(id+"F4.wireOp",EDGE,"E4.2.0.1"),sQuery(id+"F4.wireOp",EDGE,"E4.2.0.2"),sQuery(id+"F4.wireOp",EDGE,"E4.2.0.3")])]});
            var Q3;
            Q3=makeQuery(id+"F5.opExtrude","SWEPT_BODY",BODY,{"disambiguationData":[OSD([sQuery(id+"F4.wireOp",EDGE,"E4.3.0.0"),sQuery(id+"F4.wireOp",EDGE,"E4.3.0.1"),sQuery(id+"F4.wireOp",EDGE,"E4.3.0.2"),sQuery(id+"F4.wireOp",EDGE,"E4.3.0.3")])]});
            var Q4;
            Q4=makeQuery(id+"F5.opExtrude","SWEPT_BODY",BODY,{"disambiguationData":[OSD([sQuery(id+"F4.wireOp",EDGE,"E4.4.0.0"),sQuery(id+"F4.wireOp",EDGE,"E4.4.0.1"),sQuery(id+"F4.wireOp",EDGE,"E4.4.0.2"),sQuery(id+"F4.wireOp",EDGE,"E4.4.0.3")])]});
            var Q5;
            Q5=makeQuery(id+"F5.opExtrude","SWEPT_BODY",BODY,{"disambiguationData":[OSD([sQuery(id+"F4.wireOp",EDGE,"E4.5.0.0"),sQuery(id+"F4.wireOp",EDGE,"E4.5.0.1"),sQuery(id+"F4.wireOp",EDGE,"E4.5.0.2"),sQuery(id+"F4.wireOp",EDGE,"E4.5.0.3")])]});
            var Q6;
            Q6=makeQuery(id+"F5.opExtrude","SWEPT_BODY",BODY,{"disambiguationData":[OSD([sQuery(id+"F4.wireOp",EDGE,"E4.6.0.0"),sQuery(id+"F4.wireOp",EDGE,"E4.6.0.1"),sQuery(id+"F4.wireOp",EDGE,"E4.6.0.2"),sQuery(id+"F4.wireOp",EDGE,"E4.6.0.3")])]});
            var Q7;
            Q7=makeQuery(id+"F5.opExtrude","SWEPT_BODY",BODY,{"disambiguationData":[OSD([sQuery(id+"F4.wireOp",EDGE,"E4.7.0.0"),sQuery(id+"F4.wireOp",EDGE,"E4.7.0.1"),sQuery(id+"F4.wireOp",EDGE,"E4.7.0.2"),sQuery(id+"F4.wireOp",EDGE,"E4.7.0.3")])]});
            var Q8;
            Q8=makeQuery(id+"F5.opExtrude","SWEPT_BODY",BODY,{"disambiguationData":[OSD([sQuery(id+"F4.wireOp",EDGE,"E4.8.0.0"),sQuery(id+"F4.wireOp",EDGE,"E4.8.0.1"),sQuery(id+"F4.wireOp",EDGE,"E4.8.0.2"),sQuery(id+"F4.wireOp",EDGE,"E4.8.0.3")])]});
            var Q9;
            Q9=makeQuery(id+"F5.opExtrude","SWEPT_BODY",BODY,{"disambiguationData":[OSD([sQuery(id+"F4.wireOp",EDGE,"E4.9.0.0"),sQuery(id+"F4.wireOp",EDGE,"E4.9.0.1"),sQuery(id+"F4.wireOp",EDGE,"E4.9.0.2"),sQuery(id+"F4.wireOp",EDGE,"E4.9.0.3")])]});
            var Q10;
            Q10=sQuery(id+"F14.wireOp",EDGE,"E13");
            circularPattern(context, id + "F17", {"entities" : qUnion([Q0, Q1, Q2, Q3, Q4, Q5, Q6, Q7, Q8, Q9]), "axis" : qUnion([Q10]), "angle" : 90 * degree, "instanceCount" : 2});
        }
        {
            var Q0;
            Q0=makeQuery(id+"F5.opExtrude","SWEPT_BODY",BODY,{"disambiguationData":[OSD([sQuery(id+"F4.wireOp",EDGE,"E3.bottom"),sQuery(id+"F4.wireOp",EDGE,"E3.top"),sQuery(id+"F4.wireOp",EDGE,"E3.left"),sQuery(id+"F4.wireOp",EDGE,"E3.right")])]});
            var Q1;
            Q1=makeQuery(id+"F5.opExtrude","SWEPT_BODY",BODY,{"disambiguationData":[OSD([sQuery(id+"F4.wireOp",EDGE,"E4.1.0.0"),sQuery(id+"F4.wireOp",EDGE,"E4.1.0.1"),sQuery(id+"F4.wireOp",EDGE,"E4.1.0.2"),sQuery(id+"F4.wireOp",EDGE,"E4.1.0.3")])]});
            var Q2;
            Q2=makeQuery(id+"F5.opExtrude","SWEPT_BODY",BODY,{"disambiguationData":[OSD([sQuery(id+"F4.wireOp",EDGE,"E4.2.0.0"),sQuery(id+"F4.wireOp",EDGE,"E4.2.0.1"),sQuery(id+"F4.wireOp",EDGE,"E4.2.0.2"),sQuery(id+"F4.wireOp",EDGE,"E4.2.0.3")])]});
            var Q3;
            Q3=makeQuery(id+"F5.opExtrude","SWEPT_BODY",BODY,{"disambiguationData":[OSD([sQuery(id+"F4.wireOp",EDGE,"E4.3.0.0"),sQuery(id+"F4.wireOp",EDGE,"E4.3.0.1"),sQuery(id+"F4.wireOp",EDGE,"E4.3.0.2"),sQuery(id+"F4.wireOp",EDGE,"E4.3.0.3")])]});
            var Q4;
            Q4=makeQuery(id+"F5.opExtrude","SWEPT_BODY",BODY,{"disambiguationData":[OSD([sQuery(id+"F4.wireOp",EDGE,"E4.4.0.0"),sQuery(id+"F4.wireOp",EDGE,"E4.4.0.1"),sQuery(id+"F4.wireOp",EDGE,"E4.4.0.2"),sQuery(id+"F4.wireOp",EDGE,"E4.4.0.3")])]});
            var Q5;
            Q5=makeQuery(id+"F5.opExtrude","SWEPT_BODY",BODY,{"disambiguationData":[OSD([sQuery(id+"F4.wireOp",EDGE,"E4.5.0.0"),sQuery(id+"F4.wireOp",EDGE,"E4.5.0.1"),sQuery(id+"F4.wireOp",EDGE,"E4.5.0.2"),sQuery(id+"F4.wireOp",EDGE,"E4.5.0.3")])]});
            var Q6;
            Q6=makeQuery(id+"F5.opExtrude","SWEPT_BODY",BODY,{"disambiguationData":[OSD([sQuery(id+"F4.wireOp",EDGE,"E4.6.0.0"),sQuery(id+"F4.wireOp",EDGE,"E4.6.0.1"),sQuery(id+"F4.wireOp",EDGE,"E4.6.0.2"),sQuery(id+"F4.wireOp",EDGE,"E4.6.0.3")])]});
            var Q7;
            Q7=makeQuery(id+"F5.opExtrude","SWEPT_BODY",BODY,{"disambiguationData":[OSD([sQuery(id+"F4.wireOp",EDGE,"E4.7.0.0"),sQuery(id+"F4.wireOp",EDGE,"E4.7.0.1"),sQuery(id+"F4.wireOp",EDGE,"E4.7.0.2"),sQuery(id+"F4.wireOp",EDGE,"E4.7.0.3")])]});
            var Q8;
            Q8=makeQuery(id+"F5.opExtrude","SWEPT_BODY",BODY,{"disambiguationData":[OSD([sQuery(id+"F4.wireOp",EDGE,"E4.8.0.0"),sQuery(id+"F4.wireOp",EDGE,"E4.8.0.1"),sQuery(id+"F4.wireOp",EDGE,"E4.8.0.2"),sQuery(id+"F4.wireOp",EDGE,"E4.8.0.3")])]});
            var Q9;
            Q9=makeQuery(id+"F5.opExtrude","SWEPT_BODY",BODY,{"disambiguationData":[OSD([sQuery(id+"F4.wireOp",EDGE,"E4.9.0.0"),sQuery(id+"F4.wireOp",EDGE,"E4.9.0.1"),sQuery(id+"F4.wireOp",EDGE,"E4.9.0.2"),sQuery(id+"F4.wireOp",EDGE,"E4.9.0.3")])]});
            var Q10;
            Q10=sQuery(id+"F14.wireOp",EDGE,"E13");
            circularPattern(context, id + "F18", {"entities" : qUnion([Q0, Q1, Q2, Q3, Q4, Q5, Q6, Q7, Q8, Q9]), "axis" : qUnion([Q10]), "angle" : 90 * degree, "instanceCount" : 2, "oppositeDirection" : true});
        }
        {
            var Q0;
            Q0=makeQuery(id+"F1.opExtrude","SWEPT_BODY",BODY,{"disambiguationData":[OSD([sQuery(id+"F0.wireOp",EDGE,"E0.bottom"),sQuery(id+"F0.wireOp",EDGE,"E0.top"),sQuery(id+"F0.wireOp",EDGE,"E0.left"),sQuery(id+"F0.wireOp",EDGE,"E0.right"),sQuery(id+"F0.wireOp",EDGE,"E1.bottom"),sQuery(id+"F0.wireOp",EDGE,"E1.top"),sQuery(id+"F0.wireOp",EDGE,"E1.left"),sQuery(id+"F0.wireOp",EDGE,"E1.right")])]});
            var Q1;
            Q1=makeQuery(id+"F5.opExtrude","SWEPT_BODY",BODY,{"disambiguationData":[OSD([sQuery(id+"F4.wireOp",EDGE,"E3.bottom"),sQuery(id+"F4.wireOp",EDGE,"E3.top"),sQuery(id+"F4.wireOp",EDGE,"E3.left"),sQuery(id+"F4.wireOp",EDGE,"E3.right")])]});
            var Q2;
            Q2=makeQuery(id+"F5.opExtrude","SWEPT_BODY",BODY,{"disambiguationData":[OSD([sQuery(id+"F4.wireOp",EDGE,"E4.1.0.0"),sQuery(id+"F4.wireOp",EDGE,"E4.1.0.1"),sQuery(id+"F4.wireOp",EDGE,"E4.1.0.2"),sQuery(id+"F4.wireOp",EDGE,"E4.1.0.3")])]});
            var Q3;
            Q3=makeQuery(id+"F5.opExtrude","SWEPT_BODY",BODY,{"disambiguationData":[OSD([sQuery(id+"F4.wireOp",EDGE,"E4.2.0.0"),sQuery(id+"F4.wireOp",EDGE,"E4.2.0.1"),sQuery(id+"F4.wireOp",EDGE,"E4.2.0.2"),sQuery(id+"F4.wireOp",EDGE,"E4.2.0.3")])]});
            var Q4;
            Q4=makeQuery(id+"F5.opExtrude","SWEPT_BODY",BODY,{"disambiguationData":[OSD([sQuery(id+"F4.wireOp",EDGE,"E4.3.0.0"),sQuery(id+"F4.wireOp",EDGE,"E4.3.0.1"),sQuery(id+"F4.wireOp",EDGE,"E4.3.0.2"),sQuery(id+"F4.wireOp",EDGE,"E4.3.0.3")])]});
            var Q5;
            Q5=makeQuery(id+"F5.opExtrude","SWEPT_BODY",BODY,{"disambiguationData":[OSD([sQuery(id+"F4.wireOp",EDGE,"E4.4.0.0"),sQuery(id+"F4.wireOp",EDGE,"E4.4.0.1"),sQuery(id+"F4.wireOp",EDGE,"E4.4.0.2"),sQuery(id+"F4.wireOp",EDGE,"E4.4.0.3")])]});
            var Q6;
            Q6=makeQuery(id+"F5.opExtrude","SWEPT_BODY",BODY,{"disambiguationData":[OSD([sQuery(id+"F4.wireOp",EDGE,"E4.5.0.0"),sQuery(id+"F4.wireOp",EDGE,"E4.5.0.1"),sQuery(id+"F4.wireOp",EDGE,"E4.5.0.2"),sQuery(id+"F4.wireOp",EDGE,"E4.5.0.3")])]});
            var Q7;
            Q7=makeQuery(id+"F5.opExtrude","SWEPT_BODY",BODY,{"disambiguationData":[OSD([sQuery(id+"F4.wireOp",EDGE,"E4.6.0.0"),sQuery(id+"F4.wireOp",EDGE,"E4.6.0.1"),sQuery(id+"F4.wireOp",EDGE,"E4.6.0.2"),sQuery(id+"F4.wireOp",EDGE,"E4.6.0.3")])]});
            var Q8;
            Q8=makeQuery(id+"F5.opExtrude","SWEPT_BODY",BODY,{"disambiguationData":[OSD([sQuery(id+"F4.wireOp",EDGE,"E4.7.0.0"),sQuery(id+"F4.wireOp",EDGE,"E4.7.0.1"),sQuery(id+"F4.wireOp",EDGE,"E4.7.0.2"),sQuery(id+"F4.wireOp",EDGE,"E4.7.0.3")])]});
            var Q9;
            Q9=makeQuery(id+"F5.opExtrude","SWEPT_BODY",BODY,{"disambiguationData":[OSD([sQuery(id+"F4.wireOp",EDGE,"E4.8.0.0"),sQuery(id+"F4.wireOp",EDGE,"E4.8.0.1"),sQuery(id+"F4.wireOp",EDGE,"E4.8.0.2"),sQuery(id+"F4.wireOp",EDGE,"E4.8.0.3")])]});
            var Q10;
            Q10=makeQuery(id+"F5.opExtrude","SWEPT_BODY",BODY,{"disambiguationData":[OSD([sQuery(id+"F4.wireOp",EDGE,"E4.9.0.0"),sQuery(id+"F4.wireOp",EDGE,"E4.9.0.1"),sQuery(id+"F4.wireOp",EDGE,"E4.9.0.2"),sQuery(id+"F4.wireOp",EDGE,"E4.9.0.3")])]});
            var Q11;
            Q11=makeQuery(id+"F16.opPattern","COPY",BODY,{"derivedFrom":makeQuery(id+"F5.opExtrude","SWEPT_BODY",BODY,{"disambiguationData":[OSD([sQuery(id+"F4.wireOp",EDGE,"E3.bottom"),sQuery(id+"F4.wireOp",EDGE,"E3.top"),sQuery(id+"F4.wireOp",EDGE,"E3.left"),sQuery(id+"F4.wireOp",EDGE,"E3.right")])]}),"instanceName":"1"});
            var Q12;
            Q12=makeQuery(id+"F16.opPattern","COPY",BODY,{"derivedFrom":makeQuery(id+"F5.opExtrude","SWEPT_BODY",BODY,{"disambiguationData":[OSD([sQuery(id+"F4.wireOp",EDGE,"E4.1.0.0"),sQuery(id+"F4.wireOp",EDGE,"E4.1.0.1"),sQuery(id+"F4.wireOp",EDGE,"E4.1.0.2"),sQuery(id+"F4.wireOp",EDGE,"E4.1.0.3")])]}),"instanceName":"1"});
            var Q13;
            Q13=makeQuery(id+"F16.opPattern","COPY",BODY,{"derivedFrom":makeQuery(id+"F5.opExtrude","SWEPT_BODY",BODY,{"disambiguationData":[OSD([sQuery(id+"F4.wireOp",EDGE,"E4.2.0.0"),sQuery(id+"F4.wireOp",EDGE,"E4.2.0.1"),sQuery(id+"F4.wireOp",EDGE,"E4.2.0.2"),sQuery(id+"F4.wireOp",EDGE,"E4.2.0.3")])]}),"instanceName":"1"});
            var Q14;
            Q14=makeQuery(id+"F16.opPattern","COPY",BODY,{"derivedFrom":makeQuery(id+"F5.opExtrude","SWEPT_BODY",BODY,{"disambiguationData":[OSD([sQuery(id+"F4.wireOp",EDGE,"E4.3.0.0"),sQuery(id+"F4.wireOp",EDGE,"E4.3.0.1"),sQuery(id+"F4.wireOp",EDGE,"E4.3.0.2"),sQuery(id+"F4.wireOp",EDGE,"E4.3.0.3")])]}),"instanceName":"1"});
            var Q15;
            Q15=makeQuery(id+"F16.opPattern","COPY",BODY,{"derivedFrom":makeQuery(id+"F5.opExtrude","SWEPT_BODY",BODY,{"disambiguationData":[OSD([sQuery(id+"F4.wireOp",EDGE,"E4.4.0.0"),sQuery(id+"F4.wireOp",EDGE,"E4.4.0.1"),sQuery(id+"F4.wireOp",EDGE,"E4.4.0.2"),sQuery(id+"F4.wireOp",EDGE,"E4.4.0.3")])]}),"instanceName":"1"});
            var Q16;
            Q16=makeQuery(id+"F16.opPattern","COPY",BODY,{"derivedFrom":makeQuery(id+"F5.opExtrude","SWEPT_BODY",BODY,{"disambiguationData":[OSD([sQuery(id+"F4.wireOp",EDGE,"E4.5.0.0"),sQuery(id+"F4.wireOp",EDGE,"E4.5.0.1"),sQuery(id+"F4.wireOp",EDGE,"E4.5.0.2"),sQuery(id+"F4.wireOp",EDGE,"E4.5.0.3")])]}),"instanceName":"1"});
            var Q17;
            Q17=makeQuery(id+"F16.opPattern","COPY",BODY,{"derivedFrom":makeQuery(id+"F5.opExtrude","SWEPT_BODY",BODY,{"disambiguationData":[OSD([sQuery(id+"F4.wireOp",EDGE,"E4.6.0.0"),sQuery(id+"F4.wireOp",EDGE,"E4.6.0.1"),sQuery(id+"F4.wireOp",EDGE,"E4.6.0.2"),sQuery(id+"F4.wireOp",EDGE,"E4.6.0.3")])]}),"instanceName":"1"});
            var Q18;
            Q18=makeQuery(id+"F16.opPattern","COPY",BODY,{"derivedFrom":makeQuery(id+"F5.opExtrude","SWEPT_BODY",BODY,{"disambiguationData":[OSD([sQuery(id+"F4.wireOp",EDGE,"E4.7.0.0"),sQuery(id+"F4.wireOp",EDGE,"E4.7.0.1"),sQuery(id+"F4.wireOp",EDGE,"E4.7.0.2"),sQuery(id+"F4.wireOp",EDGE,"E4.7.0.3")])]}),"instanceName":"1"});
            var Q19;
            Q19=makeQuery(id+"F16.opPattern","COPY",BODY,{"derivedFrom":makeQuery(id+"F5.opExtrude","SWEPT_BODY",BODY,{"disambiguationData":[OSD([sQuery(id+"F4.wireOp",EDGE,"E4.8.0.0"),sQuery(id+"F4.wireOp",EDGE,"E4.8.0.1"),sQuery(id+"F4.wireOp",EDGE,"E4.8.0.2"),sQuery(id+"F4.wireOp",EDGE,"E4.8.0.3")])]}),"instanceName":"1"});
            var Q20;
            Q20=makeQuery(id+"F16.opPattern","COPY",BODY,{"derivedFrom":makeQuery(id+"F5.opExtrude","SWEPT_BODY",BODY,{"disambiguationData":[OSD([sQuery(id+"F4.wireOp",EDGE,"E4.9.0.0"),sQuery(id+"F4.wireOp",EDGE,"E4.9.0.1"),sQuery(id+"F4.wireOp",EDGE,"E4.9.0.2"),sQuery(id+"F4.wireOp",EDGE,"E4.9.0.3")])]}),"instanceName":"1"});
            var Q21;
            Q21=makeQuery(id+"F16.opPattern","COPY",BODY,{"derivedFrom":makeQuery(id+"F5.opExtrude","SWEPT_BODY",BODY,{"disambiguationData":[OSD([sQuery(id+"F4.wireOp",EDGE,"E3.bottom"),sQuery(id+"F4.wireOp",EDGE,"E3.top"),sQuery(id+"F4.wireOp",EDGE,"E3.left"),sQuery(id+"F4.wireOp",EDGE,"E3.right")])]}),"instanceName":"2"});
            var Q22;
            Q22=makeQuery(id+"F16.opPattern","COPY",BODY,{"derivedFrom":makeQuery(id+"F5.opExtrude","SWEPT_BODY",BODY,{"disambiguationData":[OSD([sQuery(id+"F4.wireOp",EDGE,"E4.1.0.0"),sQuery(id+"F4.wireOp",EDGE,"E4.1.0.1"),sQuery(id+"F4.wireOp",EDGE,"E4.1.0.2"),sQuery(id+"F4.wireOp",EDGE,"E4.1.0.3")])]}),"instanceName":"2"});
            var Q23;
            Q23=makeQuery(id+"F16.opPattern","COPY",BODY,{"derivedFrom":makeQuery(id+"F5.opExtrude","SWEPT_BODY",BODY,{"disambiguationData":[OSD([sQuery(id+"F4.wireOp",EDGE,"E4.2.0.0"),sQuery(id+"F4.wireOp",EDGE,"E4.2.0.1"),sQuery(id+"F4.wireOp",EDGE,"E4.2.0.2"),sQuery(id+"F4.wireOp",EDGE,"E4.2.0.3")])]}),"instanceName":"2"});
            var Q24;
            Q24=makeQuery(id+"F16.opPattern","COPY",BODY,{"derivedFrom":makeQuery(id+"F5.opExtrude","SWEPT_BODY",BODY,{"disambiguationData":[OSD([sQuery(id+"F4.wireOp",EDGE,"E4.3.0.0"),sQuery(id+"F4.wireOp",EDGE,"E4.3.0.1"),sQuery(id+"F4.wireOp",EDGE,"E4.3.0.2"),sQuery(id+"F4.wireOp",EDGE,"E4.3.0.3")])]}),"instanceName":"2"});
            var Q25;
            Q25=makeQuery(id+"F16.opPattern","COPY",BODY,{"derivedFrom":makeQuery(id+"F5.opExtrude","SWEPT_BODY",BODY,{"disambiguationData":[OSD([sQuery(id+"F4.wireOp",EDGE,"E4.4.0.0"),sQuery(id+"F4.wireOp",EDGE,"E4.4.0.1"),sQuery(id+"F4.wireOp",EDGE,"E4.4.0.2"),sQuery(id+"F4.wireOp",EDGE,"E4.4.0.3")])]}),"instanceName":"2"});
            var Q26;
            Q26=makeQuery(id+"F16.opPattern","COPY",BODY,{"derivedFrom":makeQuery(id+"F5.opExtrude","SWEPT_BODY",BODY,{"disambiguationData":[OSD([sQuery(id+"F4.wireOp",EDGE,"E4.5.0.0"),sQuery(id+"F4.wireOp",EDGE,"E4.5.0.1"),sQuery(id+"F4.wireOp",EDGE,"E4.5.0.2"),sQuery(id+"F4.wireOp",EDGE,"E4.5.0.3")])]}),"instanceName":"2"});
            var Q27;
            Q27=makeQuery(id+"F16.opPattern","COPY",BODY,{"derivedFrom":makeQuery(id+"F5.opExtrude","SWEPT_BODY",BODY,{"disambiguationData":[OSD([sQuery(id+"F4.wireOp",EDGE,"E4.6.0.0"),sQuery(id+"F4.wireOp",EDGE,"E4.6.0.1"),sQuery(id+"F4.wireOp",EDGE,"E4.6.0.2"),sQuery(id+"F4.wireOp",EDGE,"E4.6.0.3")])]}),"instanceName":"2"});
            var Q28;
            Q28=makeQuery(id+"F16.opPattern","COPY",BODY,{"derivedFrom":makeQuery(id+"F5.opExtrude","SWEPT_BODY",BODY,{"disambiguationData":[OSD([sQuery(id+"F4.wireOp",EDGE,"E4.7.0.0"),sQuery(id+"F4.wireOp",EDGE,"E4.7.0.1"),sQuery(id+"F4.wireOp",EDGE,"E4.7.0.2"),sQuery(id+"F4.wireOp",EDGE,"E4.7.0.3")])]}),"instanceName":"2"});
            var Q29;
            Q29=makeQuery(id+"F16.opPattern","COPY",BODY,{"derivedFrom":makeQuery(id+"F5.opExtrude","SWEPT_BODY",BODY,{"disambiguationData":[OSD([sQuery(id+"F4.wireOp",EDGE,"E4.8.0.0"),sQuery(id+"F4.wireOp",EDGE,"E4.8.0.1"),sQuery(id+"F4.wireOp",EDGE,"E4.8.0.2"),sQuery(id+"F4.wireOp",EDGE,"E4.8.0.3")])]}),"instanceName":"2"});
            var Q30;
            Q30=makeQuery(id+"F16.opPattern","COPY",BODY,{"derivedFrom":makeQuery(id+"F5.opExtrude","SWEPT_BODY",BODY,{"disambiguationData":[OSD([sQuery(id+"F4.wireOp",EDGE,"E4.9.0.0"),sQuery(id+"F4.wireOp",EDGE,"E4.9.0.1"),sQuery(id+"F4.wireOp",EDGE,"E4.9.0.2"),sQuery(id+"F4.wireOp",EDGE,"E4.9.0.3")])]}),"instanceName":"2"});
            var Q31;
            Q31=makeQuery(id+"F16.opPattern","COPY",BODY,{"derivedFrom":makeQuery(id+"F5.opExtrude","SWEPT_BODY",BODY,{"disambiguationData":[OSD([sQuery(id+"F4.wireOp",EDGE,"E3.bottom"),sQuery(id+"F4.wireOp",EDGE,"E3.top"),sQuery(id+"F4.wireOp",EDGE,"E3.left"),sQuery(id+"F4.wireOp",EDGE,"E3.right")])]}),"instanceName":"3"});
            var Q32;
            Q32=makeQuery(id+"F16.opPattern","COPY",BODY,{"derivedFrom":makeQuery(id+"F5.opExtrude","SWEPT_BODY",BODY,{"disambiguationData":[OSD([sQuery(id+"F4.wireOp",EDGE,"E4.1.0.0"),sQuery(id+"F4.wireOp",EDGE,"E4.1.0.1"),sQuery(id+"F4.wireOp",EDGE,"E4.1.0.2"),sQuery(id+"F4.wireOp",EDGE,"E4.1.0.3")])]}),"instanceName":"3"});
            var Q33;
            Q33=makeQuery(id+"F16.opPattern","COPY",BODY,{"derivedFrom":makeQuery(id+"F5.opExtrude","SWEPT_BODY",BODY,{"disambiguationData":[OSD([sQuery(id+"F4.wireOp",EDGE,"E4.2.0.0"),sQuery(id+"F4.wireOp",EDGE,"E4.2.0.1"),sQuery(id+"F4.wireOp",EDGE,"E4.2.0.2"),sQuery(id+"F4.wireOp",EDGE,"E4.2.0.3")])]}),"instanceName":"3"});
            var Q34;
            Q34=makeQuery(id+"F16.opPattern","COPY",BODY,{"derivedFrom":makeQuery(id+"F5.opExtrude","SWEPT_BODY",BODY,{"disambiguationData":[OSD([sQuery(id+"F4.wireOp",EDGE,"E4.3.0.0"),sQuery(id+"F4.wireOp",EDGE,"E4.3.0.1"),sQuery(id+"F4.wireOp",EDGE,"E4.3.0.2"),sQuery(id+"F4.wireOp",EDGE,"E4.3.0.3")])]}),"instanceName":"3"});
            var Q35;
            Q35=makeQuery(id+"F16.opPattern","COPY",BODY,{"derivedFrom":makeQuery(id+"F5.opExtrude","SWEPT_BODY",BODY,{"disambiguationData":[OSD([sQuery(id+"F4.wireOp",EDGE,"E4.4.0.0"),sQuery(id+"F4.wireOp",EDGE,"E4.4.0.1"),sQuery(id+"F4.wireOp",EDGE,"E4.4.0.2"),sQuery(id+"F4.wireOp",EDGE,"E4.4.0.3")])]}),"instanceName":"3"});
            var Q36;
            Q36=makeQuery(id+"F16.opPattern","COPY",BODY,{"derivedFrom":makeQuery(id+"F5.opExtrude","SWEPT_BODY",BODY,{"disambiguationData":[OSD([sQuery(id+"F4.wireOp",EDGE,"E4.5.0.0"),sQuery(id+"F4.wireOp",EDGE,"E4.5.0.1"),sQuery(id+"F4.wireOp",EDGE,"E4.5.0.2"),sQuery(id+"F4.wireOp",EDGE,"E4.5.0.3")])]}),"instanceName":"3"});
            var Q37;
            Q37=makeQuery(id+"F16.opPattern","COPY",BODY,{"derivedFrom":makeQuery(id+"F5.opExtrude","SWEPT_BODY",BODY,{"disambiguationData":[OSD([sQuery(id+"F4.wireOp",EDGE,"E4.6.0.0"),sQuery(id+"F4.wireOp",EDGE,"E4.6.0.1"),sQuery(id+"F4.wireOp",EDGE,"E4.6.0.2"),sQuery(id+"F4.wireOp",EDGE,"E4.6.0.3")])]}),"instanceName":"3"});
            var Q38;
            Q38=makeQuery(id+"F16.opPattern","COPY",BODY,{"derivedFrom":makeQuery(id+"F5.opExtrude","SWEPT_BODY",BODY,{"disambiguationData":[OSD([sQuery(id+"F4.wireOp",EDGE,"E4.7.0.0"),sQuery(id+"F4.wireOp",EDGE,"E4.7.0.1"),sQuery(id+"F4.wireOp",EDGE,"E4.7.0.2"),sQuery(id+"F4.wireOp",EDGE,"E4.7.0.3")])]}),"instanceName":"3"});
            var Q39;
            Q39=makeQuery(id+"F16.opPattern","COPY",BODY,{"derivedFrom":makeQuery(id+"F5.opExtrude","SWEPT_BODY",BODY,{"disambiguationData":[OSD([sQuery(id+"F4.wireOp",EDGE,"E4.8.0.0"),sQuery(id+"F4.wireOp",EDGE,"E4.8.0.1"),sQuery(id+"F4.wireOp",EDGE,"E4.8.0.2"),sQuery(id+"F4.wireOp",EDGE,"E4.8.0.3")])]}),"instanceName":"3"});
            var Q40;
            Q40=makeQuery(id+"F16.opPattern","COPY",BODY,{"derivedFrom":makeQuery(id+"F5.opExtrude","SWEPT_BODY",BODY,{"disambiguationData":[OSD([sQuery(id+"F4.wireOp",EDGE,"E4.9.0.0"),sQuery(id+"F4.wireOp",EDGE,"E4.9.0.1"),sQuery(id+"F4.wireOp",EDGE,"E4.9.0.2"),sQuery(id+"F4.wireOp",EDGE,"E4.9.0.3")])]}),"instanceName":"3"});
            var Q41;
            Q41=makeQuery(id+"F17.opPattern","COPY",BODY,{"derivedFrom":makeQuery(id+"F5.opExtrude","SWEPT_BODY",BODY,{"disambiguationData":[OSD([sQuery(id+"F4.wireOp",EDGE,"E3.bottom"),sQuery(id+"F4.wireOp",EDGE,"E3.top"),sQuery(id+"F4.wireOp",EDGE,"E3.left"),sQuery(id+"F4.wireOp",EDGE,"E3.right")])]}),"instanceName":"1"});
            var Q42;
            Q42=makeQuery(id+"F17.opPattern","COPY",BODY,{"derivedFrom":makeQuery(id+"F5.opExtrude","SWEPT_BODY",BODY,{"disambiguationData":[OSD([sQuery(id+"F4.wireOp",EDGE,"E4.1.0.0"),sQuery(id+"F4.wireOp",EDGE,"E4.1.0.1"),sQuery(id+"F4.wireOp",EDGE,"E4.1.0.2"),sQuery(id+"F4.wireOp",EDGE,"E4.1.0.3")])]}),"instanceName":"1"});
            var Q43;
            Q43=makeQuery(id+"F17.opPattern","COPY",BODY,{"derivedFrom":makeQuery(id+"F5.opExtrude","SWEPT_BODY",BODY,{"disambiguationData":[OSD([sQuery(id+"F4.wireOp",EDGE,"E4.2.0.0"),sQuery(id+"F4.wireOp",EDGE,"E4.2.0.1"),sQuery(id+"F4.wireOp",EDGE,"E4.2.0.2"),sQuery(id+"F4.wireOp",EDGE,"E4.2.0.3")])]}),"instanceName":"1"});
            var Q44;
            Q44=makeQuery(id+"F17.opPattern","COPY",BODY,{"derivedFrom":makeQuery(id+"F5.opExtrude","SWEPT_BODY",BODY,{"disambiguationData":[OSD([sQuery(id+"F4.wireOp",EDGE,"E4.3.0.0"),sQuery(id+"F4.wireOp",EDGE,"E4.3.0.1"),sQuery(id+"F4.wireOp",EDGE,"E4.3.0.2"),sQuery(id+"F4.wireOp",EDGE,"E4.3.0.3")])]}),"instanceName":"1"});
            var Q45;
            Q45=makeQuery(id+"F17.opPattern","COPY",BODY,{"derivedFrom":makeQuery(id+"F5.opExtrude","SWEPT_BODY",BODY,{"disambiguationData":[OSD([sQuery(id+"F4.wireOp",EDGE,"E4.4.0.0"),sQuery(id+"F4.wireOp",EDGE,"E4.4.0.1"),sQuery(id+"F4.wireOp",EDGE,"E4.4.0.2"),sQuery(id+"F4.wireOp",EDGE,"E4.4.0.3")])]}),"instanceName":"1"});
            var Q46;
            Q46=makeQuery(id+"F17.opPattern","COPY",BODY,{"derivedFrom":makeQuery(id+"F5.opExtrude","SWEPT_BODY",BODY,{"disambiguationData":[OSD([sQuery(id+"F4.wireOp",EDGE,"E4.5.0.0"),sQuery(id+"F4.wireOp",EDGE,"E4.5.0.1"),sQuery(id+"F4.wireOp",EDGE,"E4.5.0.2"),sQuery(id+"F4.wireOp",EDGE,"E4.5.0.3")])]}),"instanceName":"1"});
            var Q47;
            Q47=makeQuery(id+"F17.opPattern","COPY",BODY,{"derivedFrom":makeQuery(id+"F5.opExtrude","SWEPT_BODY",BODY,{"disambiguationData":[OSD([sQuery(id+"F4.wireOp",EDGE,"E4.6.0.0"),sQuery(id+"F4.wireOp",EDGE,"E4.6.0.1"),sQuery(id+"F4.wireOp",EDGE,"E4.6.0.2"),sQuery(id+"F4.wireOp",EDGE,"E4.6.0.3")])]}),"instanceName":"1"});
            var Q48;
            Q48=makeQuery(id+"F17.opPattern","COPY",BODY,{"derivedFrom":makeQuery(id+"F5.opExtrude","SWEPT_BODY",BODY,{"disambiguationData":[OSD([sQuery(id+"F4.wireOp",EDGE,"E4.7.0.0"),sQuery(id+"F4.wireOp",EDGE,"E4.7.0.1"),sQuery(id+"F4.wireOp",EDGE,"E4.7.0.2"),sQuery(id+"F4.wireOp",EDGE,"E4.7.0.3")])]}),"instanceName":"1"});
            var Q49;
            Q49=makeQuery(id+"F17.opPattern","COPY",BODY,{"derivedFrom":makeQuery(id+"F5.opExtrude","SWEPT_BODY",BODY,{"disambiguationData":[OSD([sQuery(id+"F4.wireOp",EDGE,"E4.8.0.0"),sQuery(id+"F4.wireOp",EDGE,"E4.8.0.1"),sQuery(id+"F4.wireOp",EDGE,"E4.8.0.2"),sQuery(id+"F4.wireOp",EDGE,"E4.8.0.3")])]}),"instanceName":"1"});
            var Q50;
            Q50=makeQuery(id+"F17.opPattern","COPY",BODY,{"derivedFrom":makeQuery(id+"F5.opExtrude","SWEPT_BODY",BODY,{"disambiguationData":[OSD([sQuery(id+"F4.wireOp",EDGE,"E4.9.0.0"),sQuery(id+"F4.wireOp",EDGE,"E4.9.0.1"),sQuery(id+"F4.wireOp",EDGE,"E4.9.0.2"),sQuery(id+"F4.wireOp",EDGE,"E4.9.0.3")])]}),"instanceName":"1"});
            var Q51;
            Q51=makeQuery(id+"F18.opPattern","COPY",BODY,{"derivedFrom":makeQuery(id+"F5.opExtrude","SWEPT_BODY",BODY,{"disambiguationData":[OSD([sQuery(id+"F4.wireOp",EDGE,"E3.bottom"),sQuery(id+"F4.wireOp",EDGE,"E3.top"),sQuery(id+"F4.wireOp",EDGE,"E3.left"),sQuery(id+"F4.wireOp",EDGE,"E3.right")])]}),"instanceName":"1"});
            var Q52;
            Q52=makeQuery(id+"F18.opPattern","COPY",BODY,{"derivedFrom":makeQuery(id+"F5.opExtrude","SWEPT_BODY",BODY,{"disambiguationData":[OSD([sQuery(id+"F4.wireOp",EDGE,"E4.1.0.0"),sQuery(id+"F4.wireOp",EDGE,"E4.1.0.1"),sQuery(id+"F4.wireOp",EDGE,"E4.1.0.2"),sQuery(id+"F4.wireOp",EDGE,"E4.1.0.3")])]}),"instanceName":"1"});
            var Q53;
            Q53=makeQuery(id+"F18.opPattern","COPY",BODY,{"derivedFrom":makeQuery(id+"F5.opExtrude","SWEPT_BODY",BODY,{"disambiguationData":[OSD([sQuery(id+"F4.wireOp",EDGE,"E4.2.0.0"),sQuery(id+"F4.wireOp",EDGE,"E4.2.0.1"),sQuery(id+"F4.wireOp",EDGE,"E4.2.0.2"),sQuery(id+"F4.wireOp",EDGE,"E4.2.0.3")])]}),"instanceName":"1"});
            var Q54;
            Q54=makeQuery(id+"F18.opPattern","COPY",BODY,{"derivedFrom":makeQuery(id+"F5.opExtrude","SWEPT_BODY",BODY,{"disambiguationData":[OSD([sQuery(id+"F4.wireOp",EDGE,"E4.3.0.0"),sQuery(id+"F4.wireOp",EDGE,"E4.3.0.1"),sQuery(id+"F4.wireOp",EDGE,"E4.3.0.2"),sQuery(id+"F4.wireOp",EDGE,"E4.3.0.3")])]}),"instanceName":"1"});
            var Q55;
            Q55=makeQuery(id+"F18.opPattern","COPY",BODY,{"derivedFrom":makeQuery(id+"F5.opExtrude","SWEPT_BODY",BODY,{"disambiguationData":[OSD([sQuery(id+"F4.wireOp",EDGE,"E4.4.0.0"),sQuery(id+"F4.wireOp",EDGE,"E4.4.0.1"),sQuery(id+"F4.wireOp",EDGE,"E4.4.0.2"),sQuery(id+"F4.wireOp",EDGE,"E4.4.0.3")])]}),"instanceName":"1"});
            var Q56;
            Q56=makeQuery(id+"F18.opPattern","COPY",BODY,{"derivedFrom":makeQuery(id+"F5.opExtrude","SWEPT_BODY",BODY,{"disambiguationData":[OSD([sQuery(id+"F4.wireOp",EDGE,"E4.5.0.0"),sQuery(id+"F4.wireOp",EDGE,"E4.5.0.1"),sQuery(id+"F4.wireOp",EDGE,"E4.5.0.2"),sQuery(id+"F4.wireOp",EDGE,"E4.5.0.3")])]}),"instanceName":"1"});
            var Q57;
            Q57=makeQuery(id+"F18.opPattern","COPY",BODY,{"derivedFrom":makeQuery(id+"F5.opExtrude","SWEPT_BODY",BODY,{"disambiguationData":[OSD([sQuery(id+"F4.wireOp",EDGE,"E4.6.0.0"),sQuery(id+"F4.wireOp",EDGE,"E4.6.0.1"),sQuery(id+"F4.wireOp",EDGE,"E4.6.0.2"),sQuery(id+"F4.wireOp",EDGE,"E4.6.0.3")])]}),"instanceName":"1"});
            var Q58;
            Q58=makeQuery(id+"F18.opPattern","COPY",BODY,{"derivedFrom":makeQuery(id+"F5.opExtrude","SWEPT_BODY",BODY,{"disambiguationData":[OSD([sQuery(id+"F4.wireOp",EDGE,"E4.7.0.0"),sQuery(id+"F4.wireOp",EDGE,"E4.7.0.1"),sQuery(id+"F4.wireOp",EDGE,"E4.7.0.2"),sQuery(id+"F4.wireOp",EDGE,"E4.7.0.3")])]}),"instanceName":"1"});
            var Q59;
            Q59=makeQuery(id+"F18.opPattern","COPY",BODY,{"derivedFrom":makeQuery(id+"F5.opExtrude","SWEPT_BODY",BODY,{"disambiguationData":[OSD([sQuery(id+"F4.wireOp",EDGE,"E4.8.0.0"),sQuery(id+"F4.wireOp",EDGE,"E4.8.0.1"),sQuery(id+"F4.wireOp",EDGE,"E4.8.0.2"),sQuery(id+"F4.wireOp",EDGE,"E4.8.0.3")])]}),"instanceName":"1"});
            var Q60;
            Q60=makeQuery(id+"F18.opPattern","COPY",BODY,{"derivedFrom":makeQuery(id+"F5.opExtrude","SWEPT_BODY",BODY,{"disambiguationData":[OSD([sQuery(id+"F4.wireOp",EDGE,"E4.9.0.0"),sQuery(id+"F4.wireOp",EDGE,"E4.9.0.1"),sQuery(id+"F4.wireOp",EDGE,"E4.9.0.2"),sQuery(id+"F4.wireOp",EDGE,"E4.9.0.3")])]}),"instanceName":"1"});
            booleanBodies(context, id + "F19", {"operationType" : BooleanOperationType.UNION, "tools" : qUnion([Q0, Q1, Q2, Q3, Q4, Q5, Q6, Q7, Q8, Q9, Q10, Q11, Q12, Q13, Q14, Q15, Q16, Q17, Q18, Q19, Q20, Q21, Q22, Q23, Q24, Q25, Q26, Q27, Q28, Q29, Q30, Q31, Q32, Q33, Q34, Q35, Q36, Q37, Q38, Q39, Q40, Q41, Q42, Q43, Q44, Q45, Q46, Q47, Q48, Q49, Q50, Q51, Q52, Q53, Q54, Q55, Q56, Q57, Q58, Q59, Q60])});
        }
        {
            var Q0;
            {var subQ1=makeQuery(id+"F3.opExtrude","SWEPT_FACE",FACE,{"disambiguationData":[OSD([sQuery(id+"F2.wireOp",EDGE,"E2.bottom")])]});var subQ2=sQuery(id+"F0.wireOp",EDGE,"E1.right");var subQ3=sQuery(id+"F0.wireOp",EDGE,"E1.top");var subQ4=sQuery(id+"F0.wireOp",EDGE,"E0.right");var subQ7=sQuery(id+"F0.wireOp",EDGE,"E1.bottom");var subQ8=sQuery(id+"F0.wireOp",EDGE,"E0.top");var subQ9=sQuery(id+"F0.wireOp",EDGE,"E0.bottom");var subQ10=makeQuery(id+"F1.opExtrude","CAP_FACE",FACE,{"disambiguationData":[OSD([subQ9,subQ8,sQuery(id+"F0.wireOp",EDGE,"E0.left"),subQ4,subQ7,subQ3,sQuery(id+"F0.wireOp",EDGE,"E1.left"),subQ2])],"isStart":false});Q0=makeQuery(id+"F19.opBoolean","SPLIT",FACE,{"disambiguationData":[TD([subQ1])],"derivedFrom":makeQuery(id+"F3.boolean.opBoolean","SPLIT",FACE,{"disambiguationData":[TD([makeQuery(id+"F1.opExtrude","SWEPT_FACE",FACE,{"disambiguationData":[OSD([subQ2])]})])],"derivedFrom":subQ10})});}
            var sketch = newSketch(context, id + "F20", { "sketchPlane" : qUnion([Q0])});
            skText(sketch, "E14", { "text": "1\n", "fontName": "OpenSans-Regular.ttf"});
            skText(sketch, "E15", { "text": "2\n", "fontName": "OpenSans-Regular.ttf"});
            skText(sketch, "E16", { "text": "3\n\n", "fontName": "OpenSans-Regular.ttf"});
            skText(sketch, "E17", { "text": "4\n", "fontName": "OpenSans-Regular.ttf"});
            skText(sketch, "E18", { "text": "5", "fontName": "OpenSans-Regular.ttf"});
            skText(sketch, "E19", { "text": "6", "fontName": "OpenSans-Regular.ttf"});
            skText(sketch, "E20", { "text": "7", "fontName": "OpenSans-Regular.ttf"});
            skText(sketch, "E21", { "text": "8", "fontName": "OpenSans-Regular.ttf"});
            skText(sketch, "E22", { "text": "9\n", "fontName": "OpenSans-Regular.ttf"});
            skText(sketch, "E23", { "text": "10", "fontName": "OpenSans-Regular.ttf"});
            const initialGuessF20  = {"E14": [0.01974, -0.00453, 1, 0, 0.00762], "E15": [0.04425, -0.00453, 1, 0, 0.00762], "E16": [0.06967, -0.00453, 1, 0, 0.00762], "E17": [0.09487, -0.00453, 1, 0, 0.00762], "E18": [0.12047, -0.00453, 1, 0, 0.00762], "E19": [0.14582, -0.00453, 1, 0, 0.00762], "E20": [0.17123, -0.00453, 1, 0, 0.00762], "E21": [0.19664, -0.00453, 1, 0, 0.00762], "E22": [0.22205, -0.00453, 1, 0, 0.00762], "E23": [0.24312, -0.00453, 1, 0, 0.00762]};
            skSetInitialGuess(sketch, initialGuessF20);
            skSolve(sketch);
        }
        {
            var Q0;
            Q0 = qSketchRegion(id + "F20", true);
            extrude(context, id + "F21", {"entities" : qUnion([Q0]), "depth" : 2.54 * mm});
        }
        {
            var Q0;
            Q0=makeQuery(id+"F21.opExtrude","SWEPT_BODY",BODY,{"disambiguationData":[OSD([sQuery(id+"F20.wireOp",EDGE,"E14.sketch_text.stroke-0"),sQuery(id+"F20.wireOp",EDGE,"E14.sketch_text.stroke-1"),sQuery(id+"F20.wireOp",EDGE,"E14.sketch_text.stroke-2"),sQuery(id+"F20.wireOp",EDGE,"E14.sketch_text.stroke-3"),sQuery(id+"F20.wireOp",EDGE,"E14.sketch_text.stroke-4"),sQuery(id+"F20.wireOp",EDGE,"E14.sketch_text.stroke-5"),sQuery(id+"F20.wireOp",EDGE,"E14.sketch_text.stroke-6"),sQuery(id+"F20.wireOp",EDGE,"E14.sketch_text.stroke-7"),sQuery(id+"F20.wireOp",EDGE,"E14.sketch_text.stroke-8")])]});
            var Q1;
            Q1=makeQuery(id+"F21.opExtrude","SWEPT_BODY",BODY,{"disambiguationData":[OSD([sQuery(id+"F20.wireOp",EDGE,"E15.sketch_text.stroke-0"),sQuery(id+"F20.wireOp",EDGE,"E15.sketch_text.stroke-1"),sQuery(id+"F20.wireOp",EDGE,"E15.sketch_text.stroke-2"),sQuery(id+"F20.wireOp",EDGE,"E15.sketch_text.stroke-3"),sQuery(id+"F20.wireOp",EDGE,"E15.sketch_text.stroke-4"),sQuery(id+"F20.wireOp",EDGE,"E15.sketch_text.stroke-5"),sQuery(id+"F20.wireOp",EDGE,"E15.sketch_text.stroke-6"),sQuery(id+"F20.wireOp",EDGE,"E15.sketch_text.stroke-7"),sQuery(id+"F20.wireOp",EDGE,"E15.sketch_text.stroke-8"),sQuery(id+"F20.wireOp",EDGE,"E15.sketch_text.stroke-9"),sQuery(id+"F20.wireOp",EDGE,"E15.sketch_text.stroke-10"),sQuery(id+"F20.wireOp",EDGE,"E15.sketch_text.stroke-11"),sQuery(id+"F20.wireOp",EDGE,"E15.sketch_text.stroke-12"),sQuery(id+"F20.wireOp",EDGE,"E15.sketch_text.stroke-13"),sQuery(id+"F20.wireOp",EDGE,"E15.sketch_text.stroke-14"),sQuery(id+"F20.wireOp",EDGE,"E15.sketch_text.stroke-15"),sQuery(id+"F20.wireOp",EDGE,"E15.sketch_text.stroke-16"),sQuery(id+"F20.wireOp",EDGE,"E15.sketch_text.stroke-17"),sQuery(id+"F20.wireOp",EDGE,"E15.sketch_text.stroke-18"),sQuery(id+"F20.wireOp",EDGE,"E15.sketch_text.stroke-19")])]});
            var Q2;
            Q2=makeQuery(id+"F21.opExtrude","SWEPT_BODY",BODY,{"disambiguationData":[OSD([sQuery(id+"F20.wireOp",EDGE,"E16.sketch_text.stroke-0"),sQuery(id+"F20.wireOp",EDGE,"E16.sketch_text.stroke-1"),sQuery(id+"F20.wireOp",EDGE,"E16.sketch_text.stroke-2"),sQuery(id+"F20.wireOp",EDGE,"E16.sketch_text.stroke-3"),sQuery(id+"F20.wireOp",EDGE,"E16.sketch_text.stroke-4"),sQuery(id+"F20.wireOp",EDGE,"E16.sketch_text.stroke-5"),sQuery(id+"F20.wireOp",EDGE,"E16.sketch_text.stroke-6"),sQuery(id+"F20.wireOp",EDGE,"E16.sketch_text.stroke-7"),sQuery(id+"F20.wireOp",EDGE,"E16.sketch_text.stroke-8"),sQuery(id+"F20.wireOp",EDGE,"E16.sketch_text.stroke-9"),sQuery(id+"F20.wireOp",EDGE,"E16.sketch_text.stroke-10"),sQuery(id+"F20.wireOp",EDGE,"E16.sketch_text.stroke-11"),sQuery(id+"F20.wireOp",EDGE,"E16.sketch_text.stroke-12"),sQuery(id+"F20.wireOp",EDGE,"E16.sketch_text.stroke-13"),sQuery(id+"F20.wireOp",EDGE,"E16.sketch_text.stroke-14"),sQuery(id+"F20.wireOp",EDGE,"E16.sketch_text.stroke-15"),sQuery(id+"F20.wireOp",EDGE,"E16.sketch_text.stroke-16"),sQuery(id+"F20.wireOp",EDGE,"E16.sketch_text.stroke-17"),sQuery(id+"F20.wireOp",EDGE,"E16.sketch_text.stroke-18"),sQuery(id+"F20.wireOp",EDGE,"E16.sketch_text.stroke-19"),sQuery(id+"F20.wireOp",EDGE,"E16.sketch_text.stroke-20"),sQuery(id+"F20.wireOp",EDGE,"E16.sketch_text.stroke-21"),sQuery(id+"F20.wireOp",EDGE,"E16.sketch_text.stroke-22"),sQuery(id+"F20.wireOp",EDGE,"E16.sketch_text.stroke-23"),sQuery(id+"F20.wireOp",EDGE,"E16.sketch_text.stroke-24"),sQuery(id+"F20.wireOp",EDGE,"E16.sketch_text.stroke-25"),sQuery(id+"F20.wireOp",EDGE,"E16.sketch_text.stroke-26"),sQuery(id+"F20.wireOp",EDGE,"E16.sketch_text.stroke-27")])]});
            var Q3;
            Q3=makeQuery(id+"F21.opExtrude","SWEPT_BODY",BODY,{"disambiguationData":[OSD([sQuery(id+"F20.wireOp",EDGE,"E17.sketch_text.stroke-0"),sQuery(id+"F20.wireOp",EDGE,"E17.sketch_text.stroke-1"),sQuery(id+"F20.wireOp",EDGE,"E17.sketch_text.stroke-2"),sQuery(id+"F20.wireOp",EDGE,"E17.sketch_text.stroke-3"),sQuery(id+"F20.wireOp",EDGE,"E17.sketch_text.stroke-4"),sQuery(id+"F20.wireOp",EDGE,"E17.sketch_text.stroke-5"),sQuery(id+"F20.wireOp",EDGE,"E17.sketch_text.stroke-6"),sQuery(id+"F20.wireOp",EDGE,"E17.sketch_text.stroke-7"),sQuery(id+"F20.wireOp",EDGE,"E17.sketch_text.stroke-8"),sQuery(id+"F20.wireOp",EDGE,"E17.sketch_text.stroke-9"),sQuery(id+"F20.wireOp",EDGE,"E17.sketch_text.stroke-10"),sQuery(id+"F20.wireOp",EDGE,"E17.sketch_text.stroke-11"),sQuery(id+"F20.wireOp",EDGE,"E17.sketch_text.stroke-12"),sQuery(id+"F20.wireOp",EDGE,"E17.sketch_text.stroke-13"),sQuery(id+"F20.wireOp",EDGE,"E17.sketch_text.stroke-14"),sQuery(id+"F20.wireOp",EDGE,"E17.sketch_text.stroke-15"),sQuery(id+"F20.wireOp",EDGE,"E17.sketch_text.stroke-16")])]});
            var Q4;
            Q4=makeQuery(id+"F21.opExtrude","SWEPT_BODY",BODY,{"disambiguationData":[OSD([sQuery(id+"F20.wireOp",EDGE,"E18.sketch_text.stroke-0"),sQuery(id+"F20.wireOp",EDGE,"E18.sketch_text.stroke-1"),sQuery(id+"F20.wireOp",EDGE,"E18.sketch_text.stroke-2"),sQuery(id+"F20.wireOp",EDGE,"E18.sketch_text.stroke-3"),sQuery(id+"F20.wireOp",EDGE,"E18.sketch_text.stroke-4"),sQuery(id+"F20.wireOp",EDGE,"E18.sketch_text.stroke-5"),sQuery(id+"F20.wireOp",EDGE,"E18.sketch_text.stroke-6"),sQuery(id+"F20.wireOp",EDGE,"E18.sketch_text.stroke-7"),sQuery(id+"F20.wireOp",EDGE,"E18.sketch_text.stroke-8"),sQuery(id+"F20.wireOp",EDGE,"E18.sketch_text.stroke-9"),sQuery(id+"F20.wireOp",EDGE,"E18.sketch_text.stroke-10"),sQuery(id+"F20.wireOp",EDGE,"E18.sketch_text.stroke-11"),sQuery(id+"F20.wireOp",EDGE,"E18.sketch_text.stroke-12"),sQuery(id+"F20.wireOp",EDGE,"E18.sketch_text.stroke-13"),sQuery(id+"F20.wireOp",EDGE,"E18.sketch_text.stroke-14"),sQuery(id+"F20.wireOp",EDGE,"E18.sketch_text.stroke-15"),sQuery(id+"F20.wireOp",EDGE,"E18.sketch_text.stroke-16"),sQuery(id+"F20.wireOp",EDGE,"E18.sketch_text.stroke-17"),sQuery(id+"F20.wireOp",EDGE,"E18.sketch_text.stroke-18")])]});
            var Q5;
            Q5=makeQuery(id+"F21.opExtrude","SWEPT_BODY",BODY,{"disambiguationData":[OSD([sQuery(id+"F20.wireOp",EDGE,"E19.sketch_text.stroke-0"),sQuery(id+"F20.wireOp",EDGE,"E19.sketch_text.stroke-1"),sQuery(id+"F20.wireOp",EDGE,"E19.sketch_text.stroke-2"),sQuery(id+"F20.wireOp",EDGE,"E19.sketch_text.stroke-3"),sQuery(id+"F20.wireOp",EDGE,"E19.sketch_text.stroke-4"),sQuery(id+"F20.wireOp",EDGE,"E19.sketch_text.stroke-5"),sQuery(id+"F20.wireOp",EDGE,"E19.sketch_text.stroke-6"),sQuery(id+"F20.wireOp",EDGE,"E19.sketch_text.stroke-7"),sQuery(id+"F20.wireOp",EDGE,"E19.sketch_text.stroke-8"),sQuery(id+"F20.wireOp",EDGE,"E19.sketch_text.stroke-9"),sQuery(id+"F20.wireOp",EDGE,"E19.sketch_text.stroke-10"),sQuery(id+"F20.wireOp",EDGE,"E19.sketch_text.stroke-11"),sQuery(id+"F20.wireOp",EDGE,"E19.sketch_text.stroke-12"),sQuery(id+"F20.wireOp",EDGE,"E19.sketch_text.stroke-13"),sQuery(id+"F20.wireOp",EDGE,"E19.sketch_text.stroke-14"),sQuery(id+"F20.wireOp",EDGE,"E19.sketch_text.stroke-15"),sQuery(id+"F20.wireOp",EDGE,"E19.sketch_text.stroke-16"),sQuery(id+"F20.wireOp",EDGE,"E19.sketch_text.stroke-17"),sQuery(id+"F20.wireOp",EDGE,"E19.sketch_text.stroke-18"),sQuery(id+"F20.wireOp",EDGE,"E19.sketch_text.stroke-19"),sQuery(id+"F20.wireOp",EDGE,"E19.sketch_text.stroke-20"),sQuery(id+"F20.wireOp",EDGE,"E19.sketch_text.stroke-21"),sQuery(id+"F20.wireOp",EDGE,"E19.sketch_text.stroke-22"),sQuery(id+"F20.wireOp",EDGE,"E19.sketch_text.stroke-23"),sQuery(id+"F20.wireOp",EDGE,"E19.sketch_text.stroke-24")])]});
            var Q6;
            Q6=makeQuery(id+"F21.opExtrude","SWEPT_BODY",BODY,{"disambiguationData":[OSD([sQuery(id+"F20.wireOp",EDGE,"E20.sketch_text.stroke-0"),sQuery(id+"F20.wireOp",EDGE,"E20.sketch_text.stroke-1"),sQuery(id+"F20.wireOp",EDGE,"E20.sketch_text.stroke-2"),sQuery(id+"F20.wireOp",EDGE,"E20.sketch_text.stroke-3"),sQuery(id+"F20.wireOp",EDGE,"E20.sketch_text.stroke-4"),sQuery(id+"F20.wireOp",EDGE,"E20.sketch_text.stroke-5"),sQuery(id+"F20.wireOp",EDGE,"E20.sketch_text.stroke-6")])]});
            var Q7;
            Q7=makeQuery(id+"F21.opExtrude","SWEPT_BODY",BODY,{"disambiguationData":[OSD([sQuery(id+"F20.wireOp",EDGE,"E21.sketch_text.stroke-0"),sQuery(id+"F20.wireOp",EDGE,"E21.sketch_text.stroke-1"),sQuery(id+"F20.wireOp",EDGE,"E21.sketch_text.stroke-2"),sQuery(id+"F20.wireOp",EDGE,"E21.sketch_text.stroke-3"),sQuery(id+"F20.wireOp",EDGE,"E21.sketch_text.stroke-4"),sQuery(id+"F20.wireOp",EDGE,"E21.sketch_text.stroke-5"),sQuery(id+"F20.wireOp",EDGE,"E21.sketch_text.stroke-6"),sQuery(id+"F20.wireOp",EDGE,"E21.sketch_text.stroke-7"),sQuery(id+"F20.wireOp",EDGE,"E21.sketch_text.stroke-8"),sQuery(id+"F20.wireOp",EDGE,"E21.sketch_text.stroke-9"),sQuery(id+"F20.wireOp",EDGE,"E21.sketch_text.stroke-10"),sQuery(id+"F20.wireOp",EDGE,"E21.sketch_text.stroke-11"),sQuery(id+"F20.wireOp",EDGE,"E21.sketch_text.stroke-12"),sQuery(id+"F20.wireOp",EDGE,"E21.sketch_text.stroke-13"),sQuery(id+"F20.wireOp",EDGE,"E21.sketch_text.stroke-14"),sQuery(id+"F20.wireOp",EDGE,"E21.sketch_text.stroke-15"),sQuery(id+"F20.wireOp",EDGE,"E21.sketch_text.stroke-16"),sQuery(id+"F20.wireOp",EDGE,"E21.sketch_text.stroke-17"),sQuery(id+"F20.wireOp",EDGE,"E21.sketch_text.stroke-18"),sQuery(id+"F20.wireOp",EDGE,"E21.sketch_text.stroke-19"),sQuery(id+"F20.wireOp",EDGE,"E21.sketch_text.stroke-20"),sQuery(id+"F20.wireOp",EDGE,"E21.sketch_text.stroke-21"),sQuery(id+"F20.wireOp",EDGE,"E21.sketch_text.stroke-22"),sQuery(id+"F20.wireOp",EDGE,"E21.sketch_text.stroke-23"),sQuery(id+"F20.wireOp",EDGE,"E21.sketch_text.stroke-24"),sQuery(id+"F20.wireOp",EDGE,"E21.sketch_text.stroke-25"),sQuery(id+"F20.wireOp",EDGE,"E21.sketch_text.stroke-26"),sQuery(id+"F20.wireOp",EDGE,"E21.sketch_text.stroke-27"),sQuery(id+"F20.wireOp",EDGE,"E21.sketch_text.stroke-28"),sQuery(id+"F20.wireOp",EDGE,"E21.sketch_text.stroke-29"),sQuery(id+"F20.wireOp",EDGE,"E21.sketch_text.stroke-30")])]});
            var Q8;
            Q8=makeQuery(id+"F21.opExtrude","SWEPT_BODY",BODY,{"disambiguationData":[OSD([sQuery(id+"F20.wireOp",EDGE,"E22.sketch_text.stroke-0"),sQuery(id+"F20.wireOp",EDGE,"E22.sketch_text.stroke-1"),sQuery(id+"F20.wireOp",EDGE,"E22.sketch_text.stroke-2"),sQuery(id+"F20.wireOp",EDGE,"E22.sketch_text.stroke-3"),sQuery(id+"F20.wireOp",EDGE,"E22.sketch_text.stroke-4"),sQuery(id+"F20.wireOp",EDGE,"E22.sketch_text.stroke-5"),sQuery(id+"F20.wireOp",EDGE,"E22.sketch_text.stroke-6"),sQuery(id+"F20.wireOp",EDGE,"E22.sketch_text.stroke-7"),sQuery(id+"F20.wireOp",EDGE,"E22.sketch_text.stroke-8"),sQuery(id+"F20.wireOp",EDGE,"E22.sketch_text.stroke-9"),sQuery(id+"F20.wireOp",EDGE,"E22.sketch_text.stroke-10"),sQuery(id+"F20.wireOp",EDGE,"E22.sketch_text.stroke-11"),sQuery(id+"F20.wireOp",EDGE,"E22.sketch_text.stroke-12"),sQuery(id+"F20.wireOp",EDGE,"E22.sketch_text.stroke-13"),sQuery(id+"F20.wireOp",EDGE,"E22.sketch_text.stroke-14"),sQuery(id+"F20.wireOp",EDGE,"E22.sketch_text.stroke-15"),sQuery(id+"F20.wireOp",EDGE,"E22.sketch_text.stroke-16"),sQuery(id+"F20.wireOp",EDGE,"E22.sketch_text.stroke-17"),sQuery(id+"F20.wireOp",EDGE,"E22.sketch_text.stroke-18"),sQuery(id+"F20.wireOp",EDGE,"E22.sketch_text.stroke-19"),sQuery(id+"F20.wireOp",EDGE,"E22.sketch_text.stroke-20"),sQuery(id+"F20.wireOp",EDGE,"E22.sketch_text.stroke-21"),sQuery(id+"F20.wireOp",EDGE,"E22.sketch_text.stroke-22"),sQuery(id+"F20.wireOp",EDGE,"E22.sketch_text.stroke-23"),sQuery(id+"F20.wireOp",EDGE,"E22.sketch_text.stroke-24"),sQuery(id+"F20.wireOp",EDGE,"E22.sketch_text.stroke-25")])]});
            var Q9;
            Q9=makeQuery(id+"F21.opExtrude","SWEPT_BODY",BODY,{"disambiguationData":[OSD([sQuery(id+"F20.wireOp",EDGE,"E23.sketch_text.stroke-0"),sQuery(id+"F20.wireOp",EDGE,"E23.sketch_text.stroke-1"),sQuery(id+"F20.wireOp",EDGE,"E23.sketch_text.stroke-2"),sQuery(id+"F20.wireOp",EDGE,"E23.sketch_text.stroke-3"),sQuery(id+"F20.wireOp",EDGE,"E23.sketch_text.stroke-4"),sQuery(id+"F20.wireOp",EDGE,"E23.sketch_text.stroke-5"),sQuery(id+"F20.wireOp",EDGE,"E23.sketch_text.stroke-6"),sQuery(id+"F20.wireOp",EDGE,"E23.sketch_text.stroke-7"),sQuery(id+"F20.wireOp",EDGE,"E23.sketch_text.stroke-8")])]});
            var Q10;
            Q10=makeQuery(id+"F21.opExtrude","SWEPT_BODY",BODY,{"disambiguationData":[OSD([sQuery(id+"F20.wireOp",EDGE,"E23.sketch_text.stroke-9"),sQuery(id+"F20.wireOp",EDGE,"E23.sketch_text.stroke-10"),sQuery(id+"F20.wireOp",EDGE,"E23.sketch_text.stroke-11"),sQuery(id+"F20.wireOp",EDGE,"E23.sketch_text.stroke-12"),sQuery(id+"F20.wireOp",EDGE,"E23.sketch_text.stroke-13"),sQuery(id+"F20.wireOp",EDGE,"E23.sketch_text.stroke-14"),sQuery(id+"F20.wireOp",EDGE,"E23.sketch_text.stroke-15"),sQuery(id+"F20.wireOp",EDGE,"E23.sketch_text.stroke-16"),sQuery(id+"F20.wireOp",EDGE,"E23.sketch_text.stroke-17"),sQuery(id+"F20.wireOp",EDGE,"E23.sketch_text.stroke-18"),sQuery(id+"F20.wireOp",EDGE,"E23.sketch_text.stroke-19"),sQuery(id+"F20.wireOp",EDGE,"E23.sketch_text.stroke-20"),sQuery(id+"F20.wireOp",EDGE,"E23.sketch_text.stroke-21"),sQuery(id+"F20.wireOp",EDGE,"E23.sketch_text.stroke-22"),sQuery(id+"F20.wireOp",EDGE,"E23.sketch_text.stroke-23"),sQuery(id+"F20.wireOp",EDGE,"E23.sketch_text.stroke-24")])]});
            var Q11;
            Q11=sQuery(id+"F14.wireOp",EDGE,"E13");
            circularPattern(context, id + "F22", {"entities" : qUnion([Q0, Q1, Q2, Q3, Q4, Q5, Q6, Q7, Q8, Q9, Q10]), "axis" : qUnion([Q11]), "angle" : 90 * degree, "instanceCount" : 2, "oppositeDirection" : true});
        }
        {
            var Q0;
            Q0=makeQuery(id+"F21.opExtrude","SWEPT_BODY",BODY,{"disambiguationData":[OSD([sQuery(id+"F20.wireOp",EDGE,"E14.sketch_text.stroke-0"),sQuery(id+"F20.wireOp",EDGE,"E14.sketch_text.stroke-1"),sQuery(id+"F20.wireOp",EDGE,"E14.sketch_text.stroke-2"),sQuery(id+"F20.wireOp",EDGE,"E14.sketch_text.stroke-3"),sQuery(id+"F20.wireOp",EDGE,"E14.sketch_text.stroke-4"),sQuery(id+"F20.wireOp",EDGE,"E14.sketch_text.stroke-5"),sQuery(id+"F20.wireOp",EDGE,"E14.sketch_text.stroke-6"),sQuery(id+"F20.wireOp",EDGE,"E14.sketch_text.stroke-7"),sQuery(id+"F20.wireOp",EDGE,"E14.sketch_text.stroke-8")])]});
            var Q1;
            Q1=makeQuery(id+"F21.opExtrude","SWEPT_BODY",BODY,{"disambiguationData":[OSD([sQuery(id+"F20.wireOp",EDGE,"E15.sketch_text.stroke-0"),sQuery(id+"F20.wireOp",EDGE,"E15.sketch_text.stroke-1"),sQuery(id+"F20.wireOp",EDGE,"E15.sketch_text.stroke-2"),sQuery(id+"F20.wireOp",EDGE,"E15.sketch_text.stroke-3"),sQuery(id+"F20.wireOp",EDGE,"E15.sketch_text.stroke-4"),sQuery(id+"F20.wireOp",EDGE,"E15.sketch_text.stroke-5"),sQuery(id+"F20.wireOp",EDGE,"E15.sketch_text.stroke-6"),sQuery(id+"F20.wireOp",EDGE,"E15.sketch_text.stroke-7"),sQuery(id+"F20.wireOp",EDGE,"E15.sketch_text.stroke-8"),sQuery(id+"F20.wireOp",EDGE,"E15.sketch_text.stroke-9"),sQuery(id+"F20.wireOp",EDGE,"E15.sketch_text.stroke-10"),sQuery(id+"F20.wireOp",EDGE,"E15.sketch_text.stroke-11"),sQuery(id+"F20.wireOp",EDGE,"E15.sketch_text.stroke-12"),sQuery(id+"F20.wireOp",EDGE,"E15.sketch_text.stroke-13"),sQuery(id+"F20.wireOp",EDGE,"E15.sketch_text.stroke-14"),sQuery(id+"F20.wireOp",EDGE,"E15.sketch_text.stroke-15"),sQuery(id+"F20.wireOp",EDGE,"E15.sketch_text.stroke-16"),sQuery(id+"F20.wireOp",EDGE,"E15.sketch_text.stroke-17"),sQuery(id+"F20.wireOp",EDGE,"E15.sketch_text.stroke-18"),sQuery(id+"F20.wireOp",EDGE,"E15.sketch_text.stroke-19")])]});
            var Q2;
            Q2=makeQuery(id+"F21.opExtrude","SWEPT_BODY",BODY,{"disambiguationData":[OSD([sQuery(id+"F20.wireOp",EDGE,"E16.sketch_text.stroke-0"),sQuery(id+"F20.wireOp",EDGE,"E16.sketch_text.stroke-1"),sQuery(id+"F20.wireOp",EDGE,"E16.sketch_text.stroke-2"),sQuery(id+"F20.wireOp",EDGE,"E16.sketch_text.stroke-3"),sQuery(id+"F20.wireOp",EDGE,"E16.sketch_text.stroke-4"),sQuery(id+"F20.wireOp",EDGE,"E16.sketch_text.stroke-5"),sQuery(id+"F20.wireOp",EDGE,"E16.sketch_text.stroke-6"),sQuery(id+"F20.wireOp",EDGE,"E16.sketch_text.stroke-7"),sQuery(id+"F20.wireOp",EDGE,"E16.sketch_text.stroke-8"),sQuery(id+"F20.wireOp",EDGE,"E16.sketch_text.stroke-9"),sQuery(id+"F20.wireOp",EDGE,"E16.sketch_text.stroke-10"),sQuery(id+"F20.wireOp",EDGE,"E16.sketch_text.stroke-11"),sQuery(id+"F20.wireOp",EDGE,"E16.sketch_text.stroke-12"),sQuery(id+"F20.wireOp",EDGE,"E16.sketch_text.stroke-13"),sQuery(id+"F20.wireOp",EDGE,"E16.sketch_text.stroke-14"),sQuery(id+"F20.wireOp",EDGE,"E16.sketch_text.stroke-15"),sQuery(id+"F20.wireOp",EDGE,"E16.sketch_text.stroke-16"),sQuery(id+"F20.wireOp",EDGE,"E16.sketch_text.stroke-17"),sQuery(id+"F20.wireOp",EDGE,"E16.sketch_text.stroke-18"),sQuery(id+"F20.wireOp",EDGE,"E16.sketch_text.stroke-19"),sQuery(id+"F20.wireOp",EDGE,"E16.sketch_text.stroke-20"),sQuery(id+"F20.wireOp",EDGE,"E16.sketch_text.stroke-21"),sQuery(id+"F20.wireOp",EDGE,"E16.sketch_text.stroke-22"),sQuery(id+"F20.wireOp",EDGE,"E16.sketch_text.stroke-23"),sQuery(id+"F20.wireOp",EDGE,"E16.sketch_text.stroke-24"),sQuery(id+"F20.wireOp",EDGE,"E16.sketch_text.stroke-25"),sQuery(id+"F20.wireOp",EDGE,"E16.sketch_text.stroke-26"),sQuery(id+"F20.wireOp",EDGE,"E16.sketch_text.stroke-27")])]});
            var Q3;
            Q3=makeQuery(id+"F21.opExtrude","SWEPT_BODY",BODY,{"disambiguationData":[OSD([sQuery(id+"F20.wireOp",EDGE,"E17.sketch_text.stroke-0"),sQuery(id+"F20.wireOp",EDGE,"E17.sketch_text.stroke-1"),sQuery(id+"F20.wireOp",EDGE,"E17.sketch_text.stroke-2"),sQuery(id+"F20.wireOp",EDGE,"E17.sketch_text.stroke-3"),sQuery(id+"F20.wireOp",EDGE,"E17.sketch_text.stroke-4"),sQuery(id+"F20.wireOp",EDGE,"E17.sketch_text.stroke-5"),sQuery(id+"F20.wireOp",EDGE,"E17.sketch_text.stroke-6"),sQuery(id+"F20.wireOp",EDGE,"E17.sketch_text.stroke-7"),sQuery(id+"F20.wireOp",EDGE,"E17.sketch_text.stroke-8"),sQuery(id+"F20.wireOp",EDGE,"E17.sketch_text.stroke-9"),sQuery(id+"F20.wireOp",EDGE,"E17.sketch_text.stroke-10"),sQuery(id+"F20.wireOp",EDGE,"E17.sketch_text.stroke-11"),sQuery(id+"F20.wireOp",EDGE,"E17.sketch_text.stroke-12"),sQuery(id+"F20.wireOp",EDGE,"E17.sketch_text.stroke-13"),sQuery(id+"F20.wireOp",EDGE,"E17.sketch_text.stroke-14"),sQuery(id+"F20.wireOp",EDGE,"E17.sketch_text.stroke-15"),sQuery(id+"F20.wireOp",EDGE,"E17.sketch_text.stroke-16")])]});
            var Q4;
            Q4=makeQuery(id+"F21.opExtrude","SWEPT_BODY",BODY,{"disambiguationData":[OSD([sQuery(id+"F20.wireOp",EDGE,"E18.sketch_text.stroke-0"),sQuery(id+"F20.wireOp",EDGE,"E18.sketch_text.stroke-1"),sQuery(id+"F20.wireOp",EDGE,"E18.sketch_text.stroke-2"),sQuery(id+"F20.wireOp",EDGE,"E18.sketch_text.stroke-3"),sQuery(id+"F20.wireOp",EDGE,"E18.sketch_text.stroke-4"),sQuery(id+"F20.wireOp",EDGE,"E18.sketch_text.stroke-5"),sQuery(id+"F20.wireOp",EDGE,"E18.sketch_text.stroke-6"),sQuery(id+"F20.wireOp",EDGE,"E18.sketch_text.stroke-7"),sQuery(id+"F20.wireOp",EDGE,"E18.sketch_text.stroke-8"),sQuery(id+"F20.wireOp",EDGE,"E18.sketch_text.stroke-9"),sQuery(id+"F20.wireOp",EDGE,"E18.sketch_text.stroke-10"),sQuery(id+"F20.wireOp",EDGE,"E18.sketch_text.stroke-11"),sQuery(id+"F20.wireOp",EDGE,"E18.sketch_text.stroke-12"),sQuery(id+"F20.wireOp",EDGE,"E18.sketch_text.stroke-13"),sQuery(id+"F20.wireOp",EDGE,"E18.sketch_text.stroke-14"),sQuery(id+"F20.wireOp",EDGE,"E18.sketch_text.stroke-15"),sQuery(id+"F20.wireOp",EDGE,"E18.sketch_text.stroke-16"),sQuery(id+"F20.wireOp",EDGE,"E18.sketch_text.stroke-17"),sQuery(id+"F20.wireOp",EDGE,"E18.sketch_text.stroke-18")])]});
            var Q5;
            Q5=makeQuery(id+"F21.opExtrude","SWEPT_BODY",BODY,{"disambiguationData":[OSD([sQuery(id+"F20.wireOp",EDGE,"E19.sketch_text.stroke-0"),sQuery(id+"F20.wireOp",EDGE,"E19.sketch_text.stroke-1"),sQuery(id+"F20.wireOp",EDGE,"E19.sketch_text.stroke-2"),sQuery(id+"F20.wireOp",EDGE,"E19.sketch_text.stroke-3"),sQuery(id+"F20.wireOp",EDGE,"E19.sketch_text.stroke-4"),sQuery(id+"F20.wireOp",EDGE,"E19.sketch_text.stroke-5"),sQuery(id+"F20.wireOp",EDGE,"E19.sketch_text.stroke-6"),sQuery(id+"F20.wireOp",EDGE,"E19.sketch_text.stroke-7"),sQuery(id+"F20.wireOp",EDGE,"E19.sketch_text.stroke-8"),sQuery(id+"F20.wireOp",EDGE,"E19.sketch_text.stroke-9"),sQuery(id+"F20.wireOp",EDGE,"E19.sketch_text.stroke-10"),sQuery(id+"F20.wireOp",EDGE,"E19.sketch_text.stroke-11"),sQuery(id+"F20.wireOp",EDGE,"E19.sketch_text.stroke-12"),sQuery(id+"F20.wireOp",EDGE,"E19.sketch_text.stroke-13"),sQuery(id+"F20.wireOp",EDGE,"E19.sketch_text.stroke-14"),sQuery(id+"F20.wireOp",EDGE,"E19.sketch_text.stroke-15"),sQuery(id+"F20.wireOp",EDGE,"E19.sketch_text.stroke-16"),sQuery(id+"F20.wireOp",EDGE,"E19.sketch_text.stroke-17"),sQuery(id+"F20.wireOp",EDGE,"E19.sketch_text.stroke-18"),sQuery(id+"F20.wireOp",EDGE,"E19.sketch_text.stroke-19"),sQuery(id+"F20.wireOp",EDGE,"E19.sketch_text.stroke-20"),sQuery(id+"F20.wireOp",EDGE,"E19.sketch_text.stroke-21"),sQuery(id+"F20.wireOp",EDGE,"E19.sketch_text.stroke-22"),sQuery(id+"F20.wireOp",EDGE,"E19.sketch_text.stroke-23"),sQuery(id+"F20.wireOp",EDGE,"E19.sketch_text.stroke-24")])]});
            var Q6;
            Q6=makeQuery(id+"F21.opExtrude","SWEPT_BODY",BODY,{"disambiguationData":[OSD([sQuery(id+"F20.wireOp",EDGE,"E20.sketch_text.stroke-0"),sQuery(id+"F20.wireOp",EDGE,"E20.sketch_text.stroke-1"),sQuery(id+"F20.wireOp",EDGE,"E20.sketch_text.stroke-2"),sQuery(id+"F20.wireOp",EDGE,"E20.sketch_text.stroke-3"),sQuery(id+"F20.wireOp",EDGE,"E20.sketch_text.stroke-4"),sQuery(id+"F20.wireOp",EDGE,"E20.sketch_text.stroke-5"),sQuery(id+"F20.wireOp",EDGE,"E20.sketch_text.stroke-6")])]});
            var Q7;
            Q7=makeQuery(id+"F21.opExtrude","SWEPT_BODY",BODY,{"disambiguationData":[OSD([sQuery(id+"F20.wireOp",EDGE,"E21.sketch_text.stroke-0"),sQuery(id+"F20.wireOp",EDGE,"E21.sketch_text.stroke-1"),sQuery(id+"F20.wireOp",EDGE,"E21.sketch_text.stroke-2"),sQuery(id+"F20.wireOp",EDGE,"E21.sketch_text.stroke-3"),sQuery(id+"F20.wireOp",EDGE,"E21.sketch_text.stroke-4"),sQuery(id+"F20.wireOp",EDGE,"E21.sketch_text.stroke-5"),sQuery(id+"F20.wireOp",EDGE,"E21.sketch_text.stroke-6"),sQuery(id+"F20.wireOp",EDGE,"E21.sketch_text.stroke-7"),sQuery(id+"F20.wireOp",EDGE,"E21.sketch_text.stroke-8"),sQuery(id+"F20.wireOp",EDGE,"E21.sketch_text.stroke-9"),sQuery(id+"F20.wireOp",EDGE,"E21.sketch_text.stroke-10"),sQuery(id+"F20.wireOp",EDGE,"E21.sketch_text.stroke-11"),sQuery(id+"F20.wireOp",EDGE,"E21.sketch_text.stroke-12"),sQuery(id+"F20.wireOp",EDGE,"E21.sketch_text.stroke-13"),sQuery(id+"F20.wireOp",EDGE,"E21.sketch_text.stroke-14"),sQuery(id+"F20.wireOp",EDGE,"E21.sketch_text.stroke-15"),sQuery(id+"F20.wireOp",EDGE,"E21.sketch_text.stroke-16"),sQuery(id+"F20.wireOp",EDGE,"E21.sketch_text.stroke-17"),sQuery(id+"F20.wireOp",EDGE,"E21.sketch_text.stroke-18"),sQuery(id+"F20.wireOp",EDGE,"E21.sketch_text.stroke-19"),sQuery(id+"F20.wireOp",EDGE,"E21.sketch_text.stroke-20"),sQuery(id+"F20.wireOp",EDGE,"E21.sketch_text.stroke-21"),sQuery(id+"F20.wireOp",EDGE,"E21.sketch_text.stroke-22"),sQuery(id+"F20.wireOp",EDGE,"E21.sketch_text.stroke-23"),sQuery(id+"F20.wireOp",EDGE,"E21.sketch_text.stroke-24"),sQuery(id+"F20.wireOp",EDGE,"E21.sketch_text.stroke-25"),sQuery(id+"F20.wireOp",EDGE,"E21.sketch_text.stroke-26"),sQuery(id+"F20.wireOp",EDGE,"E21.sketch_text.stroke-27"),sQuery(id+"F20.wireOp",EDGE,"E21.sketch_text.stroke-28"),sQuery(id+"F20.wireOp",EDGE,"E21.sketch_text.stroke-29"),sQuery(id+"F20.wireOp",EDGE,"E21.sketch_text.stroke-30")])]});
            var Q8;
            Q8=makeQuery(id+"F21.opExtrude","SWEPT_BODY",BODY,{"disambiguationData":[OSD([sQuery(id+"F20.wireOp",EDGE,"E22.sketch_text.stroke-0"),sQuery(id+"F20.wireOp",EDGE,"E22.sketch_text.stroke-1"),sQuery(id+"F20.wireOp",EDGE,"E22.sketch_text.stroke-2"),sQuery(id+"F20.wireOp",EDGE,"E22.sketch_text.stroke-3"),sQuery(id+"F20.wireOp",EDGE,"E22.sketch_text.stroke-4"),sQuery(id+"F20.wireOp",EDGE,"E22.sketch_text.stroke-5"),sQuery(id+"F20.wireOp",EDGE,"E22.sketch_text.stroke-6"),sQuery(id+"F20.wireOp",EDGE,"E22.sketch_text.stroke-7"),sQuery(id+"F20.wireOp",EDGE,"E22.sketch_text.stroke-8"),sQuery(id+"F20.wireOp",EDGE,"E22.sketch_text.stroke-9"),sQuery(id+"F20.wireOp",EDGE,"E22.sketch_text.stroke-10"),sQuery(id+"F20.wireOp",EDGE,"E22.sketch_text.stroke-11"),sQuery(id+"F20.wireOp",EDGE,"E22.sketch_text.stroke-12"),sQuery(id+"F20.wireOp",EDGE,"E22.sketch_text.stroke-13"),sQuery(id+"F20.wireOp",EDGE,"E22.sketch_text.stroke-14"),sQuery(id+"F20.wireOp",EDGE,"E22.sketch_text.stroke-15"),sQuery(id+"F20.wireOp",EDGE,"E22.sketch_text.stroke-16"),sQuery(id+"F20.wireOp",EDGE,"E22.sketch_text.stroke-17"),sQuery(id+"F20.wireOp",EDGE,"E22.sketch_text.stroke-18"),sQuery(id+"F20.wireOp",EDGE,"E22.sketch_text.stroke-19"),sQuery(id+"F20.wireOp",EDGE,"E22.sketch_text.stroke-20"),sQuery(id+"F20.wireOp",EDGE,"E22.sketch_text.stroke-21"),sQuery(id+"F20.wireOp",EDGE,"E22.sketch_text.stroke-22"),sQuery(id+"F20.wireOp",EDGE,"E22.sketch_text.stroke-23"),sQuery(id+"F20.wireOp",EDGE,"E22.sketch_text.stroke-24"),sQuery(id+"F20.wireOp",EDGE,"E22.sketch_text.stroke-25")])]});
            var Q9;
            Q9=makeQuery(id+"F21.opExtrude","SWEPT_BODY",BODY,{"disambiguationData":[OSD([sQuery(id+"F20.wireOp",EDGE,"E23.sketch_text.stroke-0"),sQuery(id+"F20.wireOp",EDGE,"E23.sketch_text.stroke-1"),sQuery(id+"F20.wireOp",EDGE,"E23.sketch_text.stroke-2"),sQuery(id+"F20.wireOp",EDGE,"E23.sketch_text.stroke-3"),sQuery(id+"F20.wireOp",EDGE,"E23.sketch_text.stroke-4"),sQuery(id+"F20.wireOp",EDGE,"E23.sketch_text.stroke-5"),sQuery(id+"F20.wireOp",EDGE,"E23.sketch_text.stroke-6"),sQuery(id+"F20.wireOp",EDGE,"E23.sketch_text.stroke-7"),sQuery(id+"F20.wireOp",EDGE,"E23.sketch_text.stroke-8")])]});
            var Q10;
            Q10=makeQuery(id+"F21.opExtrude","SWEPT_BODY",BODY,{"disambiguationData":[OSD([sQuery(id+"F20.wireOp",EDGE,"E23.sketch_text.stroke-9"),sQuery(id+"F20.wireOp",EDGE,"E23.sketch_text.stroke-10"),sQuery(id+"F20.wireOp",EDGE,"E23.sketch_text.stroke-11"),sQuery(id+"F20.wireOp",EDGE,"E23.sketch_text.stroke-12"),sQuery(id+"F20.wireOp",EDGE,"E23.sketch_text.stroke-13"),sQuery(id+"F20.wireOp",EDGE,"E23.sketch_text.stroke-14"),sQuery(id+"F20.wireOp",EDGE,"E23.sketch_text.stroke-15"),sQuery(id+"F20.wireOp",EDGE,"E23.sketch_text.stroke-16"),sQuery(id+"F20.wireOp",EDGE,"E23.sketch_text.stroke-17"),sQuery(id+"F20.wireOp",EDGE,"E23.sketch_text.stroke-18"),sQuery(id+"F20.wireOp",EDGE,"E23.sketch_text.stroke-19"),sQuery(id+"F20.wireOp",EDGE,"E23.sketch_text.stroke-20"),sQuery(id+"F20.wireOp",EDGE,"E23.sketch_text.stroke-21"),sQuery(id+"F20.wireOp",EDGE,"E23.sketch_text.stroke-22"),sQuery(id+"F20.wireOp",EDGE,"E23.sketch_text.stroke-23"),sQuery(id+"F20.wireOp",EDGE,"E23.sketch_text.stroke-24")])]});
            var Q11;
            Q11=sQuery(id+"F12.wireOp",EDGE,"E11");
            circularPattern(context, id + "F23", {"entities" : qUnion([Q0, Q1, Q2, Q3, Q4, Q5, Q6, Q7, Q8, Q9, Q10]), "axis" : qUnion([Q11]), "angle" : 90 * degree, "instanceCount" : 2});
        }
        {
            var Q0;
            {var subQ0=sQuery(id+"F0.wireOp",EDGE,"E0.left");var subQ1=sQuery(id+"F0.wireOp",EDGE,"E0.top");var subQ2=sQuery(id+"F0.wireOp",EDGE,"E1.top");var subQ5=makeQuery(id+"F3.opExtrude","SWEPT_FACE",FACE,{"disambiguationData":[OSD([sQuery(id+"F2.wireOp",EDGE,"E2.bottom")])]});var subQ6=sQuery(id+"F0.wireOp",EDGE,"E0.bottom");var subQ7=sQuery(id+"F0.wireOp",EDGE,"E1.bottom");var subQ10=sQuery(id+"F0.wireOp",EDGE,"E1.left");var subQ12=makeQuery(id+"F1.opExtrude","CAP_FACE",FACE,{"disambiguationData":[OSD([subQ6,subQ1,subQ0,sQuery(id+"F0.wireOp",EDGE,"E0.right"),subQ7,subQ2,subQ10,sQuery(id+"F0.wireOp",EDGE,"E1.right")])],"isStart":false});Q0=makeQuery(id+"F19.opBoolean","SPLIT",FACE,{"disambiguationData":[TD([subQ5])],"derivedFrom":makeQuery(id+"F3.boolean.opBoolean","SPLIT",FACE,{"disambiguationData":[TD([makeQuery(id+"F1.opExtrude","SWEPT_FACE",FACE,{"disambiguationData":[OSD([subQ10])]})])],"derivedFrom":subQ12})});}
            var sketch = newSketch(context, id + "F24", { "sketchPlane" : qUnion([Q0])});
            skText(sketch, "E24", { "text": "1", "fontName": "OpenSans-Regular.ttf"});
            skText(sketch, "E25", { "text": "2", "fontName": "OpenSans-Regular.ttf"});
            skText(sketch, "E26", { "text": "3", "fontName": "OpenSans-Regular.ttf"});
            skText(sketch, "E27", { "text": "4", "fontName": "OpenSans-Regular.ttf"});
            skText(sketch, "E28", { "text": "5", "fontName": "OpenSans-Regular.ttf"});
            skText(sketch, "E29", { "text": "6\n", "fontName": "OpenSans-Regular.ttf"});
            skText(sketch, "E30", { "text": "7", "fontName": "OpenSans-Regular.ttf"});
            skText(sketch, "E31", { "text": "8", "fontName": "OpenSans-Regular.ttf"});
            skText(sketch, "E32", { "text": "9", "fontName": "OpenSans-Regular.ttf"});
            skText(sketch, "E33", { "text": "10", "fontName": "OpenSans-Regular.ttf"});
            skLineSegment(sketch, "E34.bottom", {"start": v(-27.43, 0.76) * mm, "end": v(-22.35, 0.76) * mm});
            skLineSegment(sketch, "E34.top", {"start": v(-27.43, -0.76) * mm, "end": v(-22.35, -0.76) * mm});
            skLineSegment(sketch, "E34.left", {"start": v(-27.43, 0.76) * mm, "end": v(-27.43, -0.76) * mm});
            skLineSegment(sketch, "E34.right", {"start": v(-22.35, 0.76) * mm, "end": v(-22.35, -0.76) * mm});
            skPoint(sketch, "E35", {"position": v(-27.43, 0) * mm});
            skLineSegment(sketch, "E36.1.0.0", {"start": v(-52.83, 0.76) * mm, "end": v(-47.75, 0.76) * mm});
            skLineSegment(sketch, "E36.1.0.1", {"start": v(-52.83, -0.76) * mm, "end": v(-47.75, -0.76) * mm});
            skLineSegment(sketch, "E36.1.0.2", {"start": v(-52.83, 0.76) * mm, "end": v(-52.83, -0.76) * mm});
            skLineSegment(sketch, "E36.1.0.3", {"start": v(-47.75, 0.76) * mm, "end": v(-47.75, -0.76) * mm});
            skLineSegment(sketch, "E36.2.0.0", {"start": v(-78.23, 0.76) * mm, "end": v(-73.15, 0.76) * mm});
            skLineSegment(sketch, "E36.2.0.1", {"start": v(-78.23, -0.76) * mm, "end": v(-73.15, -0.76) * mm});
            skLineSegment(sketch, "E36.2.0.2", {"start": v(-78.23, 0.76) * mm, "end": v(-78.23, -0.76) * mm});
            skLineSegment(sketch, "E36.2.0.3", {"start": v(-73.15, 0.76) * mm, "end": v(-73.15, -0.76) * mm});
            skLineSegment(sketch, "E36.3.0.0", {"start": v(-103.63, 0.76) * mm, "end": v(-98.55, 0.76) * mm});
            skLineSegment(sketch, "E36.3.0.1", {"start": v(-103.63, -0.76) * mm, "end": v(-98.55, -0.76) * mm});
            skLineSegment(sketch, "E36.3.0.2", {"start": v(-103.63, 0.76) * mm, "end": v(-103.63, -0.76) * mm});
            skLineSegment(sketch, "E36.3.0.3", {"start": v(-98.55, 0.76) * mm, "end": v(-98.55, -0.76) * mm});
            skLineSegment(sketch, "E36.4.0.0", {"start": v(-129.03, 0.76) * mm, "end": v(-123.95, 0.76) * mm});
            skLineSegment(sketch, "E36.4.0.1", {"start": v(-129.03, -0.76) * mm, "end": v(-123.95, -0.76) * mm});
            skLineSegment(sketch, "E36.4.0.2", {"start": v(-129.03, 0.76) * mm, "end": v(-129.03, -0.76) * mm});
            skLineSegment(sketch, "E36.4.0.3", {"start": v(-123.95, 0.76) * mm, "end": v(-123.95, -0.76) * mm});
            skLineSegment(sketch, "E36.5.0.0", {"start": v(-154.43, 0.76) * mm, "end": v(-149.35, 0.76) * mm});
            skLineSegment(sketch, "E36.5.0.1", {"start": v(-154.43, -0.76) * mm, "end": v(-149.35, -0.76) * mm});
            skLineSegment(sketch, "E36.5.0.2", {"start": v(-154.43, 0.76) * mm, "end": v(-154.43, -0.76) * mm});
            skLineSegment(sketch, "E36.5.0.3", {"start": v(-149.35, 0.76) * mm, "end": v(-149.35, -0.76) * mm});
            skLineSegment(sketch, "E36.6.0.0", {"start": v(-179.83, 0.76) * mm, "end": v(-174.75, 0.76) * mm});
            skLineSegment(sketch, "E36.6.0.1", {"start": v(-179.83, -0.76) * mm, "end": v(-174.75, -0.76) * mm});
            skLineSegment(sketch, "E36.6.0.2", {"start": v(-179.83, 0.76) * mm, "end": v(-179.83, -0.76) * mm});
            skLineSegment(sketch, "E36.6.0.3", {"start": v(-174.75, 0.76) * mm, "end": v(-174.75, -0.76) * mm});
            skLineSegment(sketch, "E36.7.0.0", {"start": v(-205.23, 0.76) * mm, "end": v(-200.15, 0.76) * mm});
            skLineSegment(sketch, "E36.7.0.1", {"start": v(-205.23, -0.76) * mm, "end": v(-200.15, -0.76) * mm});
            skLineSegment(sketch, "E36.7.0.2", {"start": v(-205.23, 0.76) * mm, "end": v(-205.23, -0.76) * mm});
            skLineSegment(sketch, "E36.7.0.3", {"start": v(-200.15, 0.76) * mm, "end": v(-200.15, -0.76) * mm});
            skLineSegment(sketch, "E36.8.0.0", {"start": v(-230.63, 0.76) * mm, "end": v(-225.55, 0.76) * mm});
            skLineSegment(sketch, "E36.8.0.1", {"start": v(-230.63, -0.76) * mm, "end": v(-225.55, -0.76) * mm});
            skLineSegment(sketch, "E36.8.0.2", {"start": v(-230.63, 0.76) * mm, "end": v(-230.63, -0.76) * mm});
            skLineSegment(sketch, "E36.8.0.3", {"start": v(-225.55, 0.76) * mm, "end": v(-225.55, -0.76) * mm});
            skLineSegment(sketch, "E36.9.0.0", {"start": v(-256.03, 0.76) * mm, "end": v(-250.95, 0.76) * mm});
            skLineSegment(sketch, "E36.9.0.1", {"start": v(-256.03, -0.76) * mm, "end": v(-250.95, -0.76) * mm});
            skLineSegment(sketch, "E36.9.0.2", {"start": v(-256.03, 0.76) * mm, "end": v(-256.03, -0.76) * mm});
            skLineSegment(sketch, "E36.9.0.3", {"start": v(-250.95, 0.76) * mm, "end": v(-250.95, -0.76) * mm});
            skLineSegment(sketch, "E36.direction1", {"start": v(-27.43, 0.76) * mm, "end": v(-52.83, 0.76) * mm, "construction": true});
            const initialGuessF24  = {"E24": [-0.0216, -0.0038, 1, 0, 0.00762], "E25": [-0.047, -0.0038, 1, 0, 0.00762], "E26": [-0.0724, -0.0038, 1, 0, 0.00762], "E27": [-0.0978, -0.0038, 1, 0, 0.00762], "E28": [-0.1232, -0.0038, 1, 0, 0.00762], "E29": [-0.1486, -0.0038, 1, 0, 0.00762], "E30": [-0.174, -0.0038, 1, 0, 0.00762], "E31": [-0.1994, -0.0038, 1, 0, 0.00762], "E32": [-0.2248, -0.0038, 1, 0, 0.00762], "E33": [-0.2502, -0.0038, 1, 0, 0.00762]};
            skSetInitialGuess(sketch, initialGuessF24);
            skSolve(sketch);
        }
        {
            var Q0;
            Q0 = qSketchRegion(id + "F24", true);
            extrude(context, id + "F25", {"entities" : qUnion([Q0]), "depth" : 2.54 * mm});
        }
        {
            var Q0;
            Q0=makeQuery(id+"F25.opExtrude","SWEPT_BODY",BODY,{"disambiguationData":[OSD([sQuery(id+"F24.wireOp",EDGE,"E24.sketch_text.stroke-0"),sQuery(id+"F24.wireOp",EDGE,"E24.sketch_text.stroke-1"),sQuery(id+"F24.wireOp",EDGE,"E24.sketch_text.stroke-2"),sQuery(id+"F24.wireOp",EDGE,"E24.sketch_text.stroke-3"),sQuery(id+"F24.wireOp",EDGE,"E24.sketch_text.stroke-4"),sQuery(id+"F24.wireOp",EDGE,"E24.sketch_text.stroke-5"),sQuery(id+"F24.wireOp",EDGE,"E24.sketch_text.stroke-6"),sQuery(id+"F24.wireOp",EDGE,"E24.sketch_text.stroke-7"),sQuery(id+"F24.wireOp",EDGE,"E24.sketch_text.stroke-8")])]});
            var Q1;
            Q1=makeQuery(id+"F25.opExtrude","SWEPT_BODY",BODY,{"disambiguationData":[OSD([sQuery(id+"F24.wireOp",EDGE,"E25.sketch_text.stroke-0"),sQuery(id+"F24.wireOp",EDGE,"E25.sketch_text.stroke-1"),sQuery(id+"F24.wireOp",EDGE,"E25.sketch_text.stroke-2"),sQuery(id+"F24.wireOp",EDGE,"E25.sketch_text.stroke-3"),sQuery(id+"F24.wireOp",EDGE,"E25.sketch_text.stroke-4"),sQuery(id+"F24.wireOp",EDGE,"E25.sketch_text.stroke-5"),sQuery(id+"F24.wireOp",EDGE,"E25.sketch_text.stroke-6"),sQuery(id+"F24.wireOp",EDGE,"E25.sketch_text.stroke-7"),sQuery(id+"F24.wireOp",EDGE,"E25.sketch_text.stroke-8"),sQuery(id+"F24.wireOp",EDGE,"E25.sketch_text.stroke-9"),sQuery(id+"F24.wireOp",EDGE,"E25.sketch_text.stroke-10"),sQuery(id+"F24.wireOp",EDGE,"E25.sketch_text.stroke-11"),sQuery(id+"F24.wireOp",EDGE,"E25.sketch_text.stroke-12"),sQuery(id+"F24.wireOp",EDGE,"E25.sketch_text.stroke-13"),sQuery(id+"F24.wireOp",EDGE,"E25.sketch_text.stroke-14"),sQuery(id+"F24.wireOp",EDGE,"E25.sketch_text.stroke-15"),sQuery(id+"F24.wireOp",EDGE,"E25.sketch_text.stroke-16"),sQuery(id+"F24.wireOp",EDGE,"E25.sketch_text.stroke-17"),sQuery(id+"F24.wireOp",EDGE,"E25.sketch_text.stroke-18"),sQuery(id+"F24.wireOp",EDGE,"E25.sketch_text.stroke-19")])]});
            var Q2;
            Q2=makeQuery(id+"F25.opExtrude","SWEPT_BODY",BODY,{"disambiguationData":[OSD([sQuery(id+"F24.wireOp",EDGE,"E26.sketch_text.stroke-0"),sQuery(id+"F24.wireOp",EDGE,"E26.sketch_text.stroke-1"),sQuery(id+"F24.wireOp",EDGE,"E26.sketch_text.stroke-2"),sQuery(id+"F24.wireOp",EDGE,"E26.sketch_text.stroke-3"),sQuery(id+"F24.wireOp",EDGE,"E26.sketch_text.stroke-4"),sQuery(id+"F24.wireOp",EDGE,"E26.sketch_text.stroke-5"),sQuery(id+"F24.wireOp",EDGE,"E26.sketch_text.stroke-6"),sQuery(id+"F24.wireOp",EDGE,"E26.sketch_text.stroke-7"),sQuery(id+"F24.wireOp",EDGE,"E26.sketch_text.stroke-8"),sQuery(id+"F24.wireOp",EDGE,"E26.sketch_text.stroke-9"),sQuery(id+"F24.wireOp",EDGE,"E26.sketch_text.stroke-10"),sQuery(id+"F24.wireOp",EDGE,"E26.sketch_text.stroke-11"),sQuery(id+"F24.wireOp",EDGE,"E26.sketch_text.stroke-12"),sQuery(id+"F24.wireOp",EDGE,"E26.sketch_text.stroke-13"),sQuery(id+"F24.wireOp",EDGE,"E26.sketch_text.stroke-14"),sQuery(id+"F24.wireOp",EDGE,"E26.sketch_text.stroke-15"),sQuery(id+"F24.wireOp",EDGE,"E26.sketch_text.stroke-16"),sQuery(id+"F24.wireOp",EDGE,"E26.sketch_text.stroke-17"),sQuery(id+"F24.wireOp",EDGE,"E26.sketch_text.stroke-18"),sQuery(id+"F24.wireOp",EDGE,"E26.sketch_text.stroke-19"),sQuery(id+"F24.wireOp",EDGE,"E26.sketch_text.stroke-20"),sQuery(id+"F24.wireOp",EDGE,"E26.sketch_text.stroke-21"),sQuery(id+"F24.wireOp",EDGE,"E26.sketch_text.stroke-22"),sQuery(id+"F24.wireOp",EDGE,"E26.sketch_text.stroke-23"),sQuery(id+"F24.wireOp",EDGE,"E26.sketch_text.stroke-24"),sQuery(id+"F24.wireOp",EDGE,"E26.sketch_text.stroke-25"),sQuery(id+"F24.wireOp",EDGE,"E26.sketch_text.stroke-26"),sQuery(id+"F24.wireOp",EDGE,"E26.sketch_text.stroke-27")])]});
            var Q3;
            Q3=makeQuery(id+"F25.opExtrude","SWEPT_BODY",BODY,{"disambiguationData":[OSD([sQuery(id+"F24.wireOp",EDGE,"E27.sketch_text.stroke-0"),sQuery(id+"F24.wireOp",EDGE,"E27.sketch_text.stroke-1"),sQuery(id+"F24.wireOp",EDGE,"E27.sketch_text.stroke-2"),sQuery(id+"F24.wireOp",EDGE,"E27.sketch_text.stroke-3"),sQuery(id+"F24.wireOp",EDGE,"E27.sketch_text.stroke-4"),sQuery(id+"F24.wireOp",EDGE,"E27.sketch_text.stroke-5"),sQuery(id+"F24.wireOp",EDGE,"E27.sketch_text.stroke-6"),sQuery(id+"F24.wireOp",EDGE,"E27.sketch_text.stroke-7"),sQuery(id+"F24.wireOp",EDGE,"E27.sketch_text.stroke-8"),sQuery(id+"F24.wireOp",EDGE,"E27.sketch_text.stroke-9"),sQuery(id+"F24.wireOp",EDGE,"E27.sketch_text.stroke-10"),sQuery(id+"F24.wireOp",EDGE,"E27.sketch_text.stroke-11"),sQuery(id+"F24.wireOp",EDGE,"E27.sketch_text.stroke-12"),sQuery(id+"F24.wireOp",EDGE,"E27.sketch_text.stroke-13"),sQuery(id+"F24.wireOp",EDGE,"E27.sketch_text.stroke-14"),sQuery(id+"F24.wireOp",EDGE,"E27.sketch_text.stroke-15"),sQuery(id+"F24.wireOp",EDGE,"E27.sketch_text.stroke-16")])]});
            var Q4;
            Q4=makeQuery(id+"F25.opExtrude","SWEPT_BODY",BODY,{"disambiguationData":[OSD([sQuery(id+"F24.wireOp",EDGE,"E28.sketch_text.stroke-0"),sQuery(id+"F24.wireOp",EDGE,"E28.sketch_text.stroke-1"),sQuery(id+"F24.wireOp",EDGE,"E28.sketch_text.stroke-2"),sQuery(id+"F24.wireOp",EDGE,"E28.sketch_text.stroke-3"),sQuery(id+"F24.wireOp",EDGE,"E28.sketch_text.stroke-4"),sQuery(id+"F24.wireOp",EDGE,"E28.sketch_text.stroke-5"),sQuery(id+"F24.wireOp",EDGE,"E28.sketch_text.stroke-6"),sQuery(id+"F24.wireOp",EDGE,"E28.sketch_text.stroke-7"),sQuery(id+"F24.wireOp",EDGE,"E28.sketch_text.stroke-8"),sQuery(id+"F24.wireOp",EDGE,"E28.sketch_text.stroke-9"),sQuery(id+"F24.wireOp",EDGE,"E28.sketch_text.stroke-10"),sQuery(id+"F24.wireOp",EDGE,"E28.sketch_text.stroke-11"),sQuery(id+"F24.wireOp",EDGE,"E28.sketch_text.stroke-12"),sQuery(id+"F24.wireOp",EDGE,"E28.sketch_text.stroke-13"),sQuery(id+"F24.wireOp",EDGE,"E28.sketch_text.stroke-14"),sQuery(id+"F24.wireOp",EDGE,"E28.sketch_text.stroke-15"),sQuery(id+"F24.wireOp",EDGE,"E28.sketch_text.stroke-16"),sQuery(id+"F24.wireOp",EDGE,"E28.sketch_text.stroke-17"),sQuery(id+"F24.wireOp",EDGE,"E28.sketch_text.stroke-18")])]});
            var Q5;
            Q5=makeQuery(id+"F25.opExtrude","SWEPT_BODY",BODY,{"disambiguationData":[OSD([sQuery(id+"F24.wireOp",EDGE,"E29.sketch_text.stroke-0"),sQuery(id+"F24.wireOp",EDGE,"E29.sketch_text.stroke-1"),sQuery(id+"F24.wireOp",EDGE,"E29.sketch_text.stroke-2"),sQuery(id+"F24.wireOp",EDGE,"E29.sketch_text.stroke-3"),sQuery(id+"F24.wireOp",EDGE,"E29.sketch_text.stroke-4"),sQuery(id+"F24.wireOp",EDGE,"E29.sketch_text.stroke-5"),sQuery(id+"F24.wireOp",EDGE,"E29.sketch_text.stroke-6"),sQuery(id+"F24.wireOp",EDGE,"E29.sketch_text.stroke-7"),sQuery(id+"F24.wireOp",EDGE,"E29.sketch_text.stroke-8"),sQuery(id+"F24.wireOp",EDGE,"E29.sketch_text.stroke-9"),sQuery(id+"F24.wireOp",EDGE,"E29.sketch_text.stroke-10"),sQuery(id+"F24.wireOp",EDGE,"E29.sketch_text.stroke-11"),sQuery(id+"F24.wireOp",EDGE,"E29.sketch_text.stroke-12"),sQuery(id+"F24.wireOp",EDGE,"E29.sketch_text.stroke-13"),sQuery(id+"F24.wireOp",EDGE,"E29.sketch_text.stroke-14"),sQuery(id+"F24.wireOp",EDGE,"E29.sketch_text.stroke-15"),sQuery(id+"F24.wireOp",EDGE,"E29.sketch_text.stroke-16"),sQuery(id+"F24.wireOp",EDGE,"E29.sketch_text.stroke-17"),sQuery(id+"F24.wireOp",EDGE,"E29.sketch_text.stroke-18"),sQuery(id+"F24.wireOp",EDGE,"E29.sketch_text.stroke-19"),sQuery(id+"F24.wireOp",EDGE,"E29.sketch_text.stroke-20"),sQuery(id+"F24.wireOp",EDGE,"E29.sketch_text.stroke-21"),sQuery(id+"F24.wireOp",EDGE,"E29.sketch_text.stroke-22"),sQuery(id+"F24.wireOp",EDGE,"E29.sketch_text.stroke-23"),sQuery(id+"F24.wireOp",EDGE,"E29.sketch_text.stroke-24")])]});
            var Q6;
            Q6=makeQuery(id+"F25.opExtrude","SWEPT_BODY",BODY,{"disambiguationData":[OSD([sQuery(id+"F24.wireOp",EDGE,"E30.sketch_text.stroke-0"),sQuery(id+"F24.wireOp",EDGE,"E30.sketch_text.stroke-1"),sQuery(id+"F24.wireOp",EDGE,"E30.sketch_text.stroke-2"),sQuery(id+"F24.wireOp",EDGE,"E30.sketch_text.stroke-3"),sQuery(id+"F24.wireOp",EDGE,"E30.sketch_text.stroke-4"),sQuery(id+"F24.wireOp",EDGE,"E30.sketch_text.stroke-5"),sQuery(id+"F24.wireOp",EDGE,"E30.sketch_text.stroke-6")])]});
            var Q7;
            Q7=makeQuery(id+"F25.opExtrude","SWEPT_BODY",BODY,{"disambiguationData":[OSD([sQuery(id+"F24.wireOp",EDGE,"E31.sketch_text.stroke-0"),sQuery(id+"F24.wireOp",EDGE,"E31.sketch_text.stroke-1"),sQuery(id+"F24.wireOp",EDGE,"E31.sketch_text.stroke-2"),sQuery(id+"F24.wireOp",EDGE,"E31.sketch_text.stroke-3"),sQuery(id+"F24.wireOp",EDGE,"E31.sketch_text.stroke-4"),sQuery(id+"F24.wireOp",EDGE,"E31.sketch_text.stroke-5"),sQuery(id+"F24.wireOp",EDGE,"E31.sketch_text.stroke-6"),sQuery(id+"F24.wireOp",EDGE,"E31.sketch_text.stroke-7"),sQuery(id+"F24.wireOp",EDGE,"E31.sketch_text.stroke-8"),sQuery(id+"F24.wireOp",EDGE,"E31.sketch_text.stroke-9"),sQuery(id+"F24.wireOp",EDGE,"E31.sketch_text.stroke-10"),sQuery(id+"F24.wireOp",EDGE,"E31.sketch_text.stroke-11"),sQuery(id+"F24.wireOp",EDGE,"E31.sketch_text.stroke-12"),sQuery(id+"F24.wireOp",EDGE,"E31.sketch_text.stroke-13"),sQuery(id+"F24.wireOp",EDGE,"E31.sketch_text.stroke-14"),sQuery(id+"F24.wireOp",EDGE,"E31.sketch_text.stroke-15"),sQuery(id+"F24.wireOp",EDGE,"E31.sketch_text.stroke-16"),sQuery(id+"F24.wireOp",EDGE,"E31.sketch_text.stroke-17"),sQuery(id+"F24.wireOp",EDGE,"E31.sketch_text.stroke-18"),sQuery(id+"F24.wireOp",EDGE,"E31.sketch_text.stroke-19"),sQuery(id+"F24.wireOp",EDGE,"E31.sketch_text.stroke-20"),sQuery(id+"F24.wireOp",EDGE,"E31.sketch_text.stroke-21"),sQuery(id+"F24.wireOp",EDGE,"E31.sketch_text.stroke-22"),sQuery(id+"F24.wireOp",EDGE,"E31.sketch_text.stroke-23"),sQuery(id+"F24.wireOp",EDGE,"E31.sketch_text.stroke-24"),sQuery(id+"F24.wireOp",EDGE,"E31.sketch_text.stroke-25"),sQuery(id+"F24.wireOp",EDGE,"E31.sketch_text.stroke-26"),sQuery(id+"F24.wireOp",EDGE,"E31.sketch_text.stroke-27"),sQuery(id+"F24.wireOp",EDGE,"E31.sketch_text.stroke-28"),sQuery(id+"F24.wireOp",EDGE,"E31.sketch_text.stroke-29"),sQuery(id+"F24.wireOp",EDGE,"E31.sketch_text.stroke-30")])]});
            var Q8;
            Q8=makeQuery(id+"F25.opExtrude","SWEPT_BODY",BODY,{"disambiguationData":[OSD([sQuery(id+"F24.wireOp",EDGE,"E32.sketch_text.stroke-0"),sQuery(id+"F24.wireOp",EDGE,"E32.sketch_text.stroke-1"),sQuery(id+"F24.wireOp",EDGE,"E32.sketch_text.stroke-2"),sQuery(id+"F24.wireOp",EDGE,"E32.sketch_text.stroke-3"),sQuery(id+"F24.wireOp",EDGE,"E32.sketch_text.stroke-4"),sQuery(id+"F24.wireOp",EDGE,"E32.sketch_text.stroke-5"),sQuery(id+"F24.wireOp",EDGE,"E32.sketch_text.stroke-6"),sQuery(id+"F24.wireOp",EDGE,"E32.sketch_text.stroke-7"),sQuery(id+"F24.wireOp",EDGE,"E32.sketch_text.stroke-8"),sQuery(id+"F24.wireOp",EDGE,"E32.sketch_text.stroke-9"),sQuery(id+"F24.wireOp",EDGE,"E32.sketch_text.stroke-10"),sQuery(id+"F24.wireOp",EDGE,"E32.sketch_text.stroke-11"),sQuery(id+"F24.wireOp",EDGE,"E32.sketch_text.stroke-12"),sQuery(id+"F24.wireOp",EDGE,"E32.sketch_text.stroke-13"),sQuery(id+"F24.wireOp",EDGE,"E32.sketch_text.stroke-14"),sQuery(id+"F24.wireOp",EDGE,"E32.sketch_text.stroke-15"),sQuery(id+"F24.wireOp",EDGE,"E32.sketch_text.stroke-16"),sQuery(id+"F24.wireOp",EDGE,"E32.sketch_text.stroke-17"),sQuery(id+"F24.wireOp",EDGE,"E32.sketch_text.stroke-18"),sQuery(id+"F24.wireOp",EDGE,"E32.sketch_text.stroke-19"),sQuery(id+"F24.wireOp",EDGE,"E32.sketch_text.stroke-20"),sQuery(id+"F24.wireOp",EDGE,"E32.sketch_text.stroke-21"),sQuery(id+"F24.wireOp",EDGE,"E32.sketch_text.stroke-22"),sQuery(id+"F24.wireOp",EDGE,"E32.sketch_text.stroke-23"),sQuery(id+"F24.wireOp",EDGE,"E32.sketch_text.stroke-24"),sQuery(id+"F24.wireOp",EDGE,"E32.sketch_text.stroke-25")])]});
            var Q9;
            Q9=makeQuery(id+"F25.opExtrude","SWEPT_BODY",BODY,{"disambiguationData":[OSD([sQuery(id+"F24.wireOp",EDGE,"E33.sketch_text.stroke-0"),sQuery(id+"F24.wireOp",EDGE,"E33.sketch_text.stroke-1"),sQuery(id+"F24.wireOp",EDGE,"E33.sketch_text.stroke-2"),sQuery(id+"F24.wireOp",EDGE,"E33.sketch_text.stroke-3"),sQuery(id+"F24.wireOp",EDGE,"E33.sketch_text.stroke-4"),sQuery(id+"F24.wireOp",EDGE,"E33.sketch_text.stroke-5"),sQuery(id+"F24.wireOp",EDGE,"E33.sketch_text.stroke-6"),sQuery(id+"F24.wireOp",EDGE,"E33.sketch_text.stroke-7"),sQuery(id+"F24.wireOp",EDGE,"E33.sketch_text.stroke-8")])]});
            var Q10;
            Q10=makeQuery(id+"F25.opExtrude","SWEPT_BODY",BODY,{"disambiguationData":[OSD([sQuery(id+"F24.wireOp",EDGE,"E33.sketch_text.stroke-9"),sQuery(id+"F24.wireOp",EDGE,"E33.sketch_text.stroke-10"),sQuery(id+"F24.wireOp",EDGE,"E33.sketch_text.stroke-11"),sQuery(id+"F24.wireOp",EDGE,"E33.sketch_text.stroke-12"),sQuery(id+"F24.wireOp",EDGE,"E33.sketch_text.stroke-13"),sQuery(id+"F24.wireOp",EDGE,"E33.sketch_text.stroke-14"),sQuery(id+"F24.wireOp",EDGE,"E33.sketch_text.stroke-15"),sQuery(id+"F24.wireOp",EDGE,"E33.sketch_text.stroke-16"),sQuery(id+"F24.wireOp",EDGE,"E33.sketch_text.stroke-17"),sQuery(id+"F24.wireOp",EDGE,"E33.sketch_text.stroke-18"),sQuery(id+"F24.wireOp",EDGE,"E33.sketch_text.stroke-19"),sQuery(id+"F24.wireOp",EDGE,"E33.sketch_text.stroke-20"),sQuery(id+"F24.wireOp",EDGE,"E33.sketch_text.stroke-21"),sQuery(id+"F24.wireOp",EDGE,"E33.sketch_text.stroke-22"),sQuery(id+"F24.wireOp",EDGE,"E33.sketch_text.stroke-23"),sQuery(id+"F24.wireOp",EDGE,"E33.sketch_text.stroke-24")])]});
            var Q11;
            Q11=makeQuery(id+"F25.opExtrude","SWEPT_BODY",BODY,{"disambiguationData":[OSD([sQuery(id+"F24.wireOp",EDGE,"E34.bottom"),sQuery(id+"F24.wireOp",EDGE,"E34.top"),sQuery(id+"F24.wireOp",EDGE,"E34.left"),sQuery(id+"F24.wireOp",EDGE,"E34.right")])]});
            var Q12;
            Q12=makeQuery(id+"F25.opExtrude","SWEPT_BODY",BODY,{"disambiguationData":[OSD([sQuery(id+"F24.wireOp",EDGE,"E36.1.0.0"),sQuery(id+"F24.wireOp",EDGE,"E36.1.0.1"),sQuery(id+"F24.wireOp",EDGE,"E36.1.0.2"),sQuery(id+"F24.wireOp",EDGE,"E36.1.0.3")])]});
            var Q13;
            Q13=makeQuery(id+"F25.opExtrude","SWEPT_BODY",BODY,{"disambiguationData":[OSD([sQuery(id+"F24.wireOp",EDGE,"E36.2.0.0"),sQuery(id+"F24.wireOp",EDGE,"E36.2.0.1"),sQuery(id+"F24.wireOp",EDGE,"E36.2.0.2"),sQuery(id+"F24.wireOp",EDGE,"E36.2.0.3")])]});
            var Q14;
            Q14=makeQuery(id+"F25.opExtrude","SWEPT_BODY",BODY,{"disambiguationData":[OSD([sQuery(id+"F24.wireOp",EDGE,"E36.3.0.0"),sQuery(id+"F24.wireOp",EDGE,"E36.3.0.1"),sQuery(id+"F24.wireOp",EDGE,"E36.3.0.2"),sQuery(id+"F24.wireOp",EDGE,"E36.3.0.3")])]});
            var Q15;
            Q15=makeQuery(id+"F25.opExtrude","SWEPT_BODY",BODY,{"disambiguationData":[OSD([sQuery(id+"F24.wireOp",EDGE,"E36.4.0.0"),sQuery(id+"F24.wireOp",EDGE,"E36.4.0.1"),sQuery(id+"F24.wireOp",EDGE,"E36.4.0.2"),sQuery(id+"F24.wireOp",EDGE,"E36.4.0.3")])]});
            var Q16;
            Q16=makeQuery(id+"F25.opExtrude","SWEPT_BODY",BODY,{"disambiguationData":[OSD([sQuery(id+"F24.wireOp",EDGE,"E36.5.0.0"),sQuery(id+"F24.wireOp",EDGE,"E36.5.0.1"),sQuery(id+"F24.wireOp",EDGE,"E36.5.0.2"),sQuery(id+"F24.wireOp",EDGE,"E36.5.0.3")])]});
            var Q17;
            Q17=makeQuery(id+"F25.opExtrude","SWEPT_BODY",BODY,{"disambiguationData":[OSD([sQuery(id+"F24.wireOp",EDGE,"E36.6.0.0"),sQuery(id+"F24.wireOp",EDGE,"E36.6.0.1"),sQuery(id+"F24.wireOp",EDGE,"E36.6.0.2"),sQuery(id+"F24.wireOp",EDGE,"E36.6.0.3")])]});
            var Q18;
            Q18=makeQuery(id+"F25.opExtrude","SWEPT_BODY",BODY,{"disambiguationData":[OSD([sQuery(id+"F24.wireOp",EDGE,"E36.7.0.0"),sQuery(id+"F24.wireOp",EDGE,"E36.7.0.1"),sQuery(id+"F24.wireOp",EDGE,"E36.7.0.2"),sQuery(id+"F24.wireOp",EDGE,"E36.7.0.3")])]});
            var Q19;
            Q19=makeQuery(id+"F25.opExtrude","SWEPT_BODY",BODY,{"disambiguationData":[OSD([sQuery(id+"F24.wireOp",EDGE,"E36.8.0.0"),sQuery(id+"F24.wireOp",EDGE,"E36.8.0.1"),sQuery(id+"F24.wireOp",EDGE,"E36.8.0.2"),sQuery(id+"F24.wireOp",EDGE,"E36.8.0.3")])]});
            var Q20;
            Q20=makeQuery(id+"F25.opExtrude","SWEPT_BODY",BODY,{"disambiguationData":[OSD([sQuery(id+"F24.wireOp",EDGE,"E36.9.0.0"),sQuery(id+"F24.wireOp",EDGE,"E36.9.0.1"),sQuery(id+"F24.wireOp",EDGE,"E36.9.0.2"),sQuery(id+"F24.wireOp",EDGE,"E36.9.0.3")])]});
            var Q21;
            Q21=sQuery(id+"F14.wireOp",EDGE,"E13");
            circularPattern(context, id + "F26", {"entities" : qUnion([Q0, Q1, Q2, Q3, Q4, Q5, Q6, Q7, Q8, Q9, Q10, Q11, Q12, Q13, Q14, Q15, Q16, Q17, Q18, Q19, Q20]), "axis" : qUnion([Q21]), "angle" : 90 * degree, "instanceCount" : 2, "oppositeDirection" : true});
        }
        {
            var Q0;
            Q0=makeQuery(id+"F25.opExtrude","SWEPT_BODY",BODY,{"disambiguationData":[OSD([sQuery(id+"F24.wireOp",EDGE,"E24.sketch_text.stroke-0"),sQuery(id+"F24.wireOp",EDGE,"E24.sketch_text.stroke-1"),sQuery(id+"F24.wireOp",EDGE,"E24.sketch_text.stroke-2"),sQuery(id+"F24.wireOp",EDGE,"E24.sketch_text.stroke-3"),sQuery(id+"F24.wireOp",EDGE,"E24.sketch_text.stroke-4"),sQuery(id+"F24.wireOp",EDGE,"E24.sketch_text.stroke-5"),sQuery(id+"F24.wireOp",EDGE,"E24.sketch_text.stroke-6"),sQuery(id+"F24.wireOp",EDGE,"E24.sketch_text.stroke-7"),sQuery(id+"F24.wireOp",EDGE,"E24.sketch_text.stroke-8")])]});
            var Q1;
            Q1=makeQuery(id+"F25.opExtrude","SWEPT_BODY",BODY,{"disambiguationData":[OSD([sQuery(id+"F24.wireOp",EDGE,"E25.sketch_text.stroke-0"),sQuery(id+"F24.wireOp",EDGE,"E25.sketch_text.stroke-1"),sQuery(id+"F24.wireOp",EDGE,"E25.sketch_text.stroke-2"),sQuery(id+"F24.wireOp",EDGE,"E25.sketch_text.stroke-3"),sQuery(id+"F24.wireOp",EDGE,"E25.sketch_text.stroke-4"),sQuery(id+"F24.wireOp",EDGE,"E25.sketch_text.stroke-5"),sQuery(id+"F24.wireOp",EDGE,"E25.sketch_text.stroke-6"),sQuery(id+"F24.wireOp",EDGE,"E25.sketch_text.stroke-7"),sQuery(id+"F24.wireOp",EDGE,"E25.sketch_text.stroke-8"),sQuery(id+"F24.wireOp",EDGE,"E25.sketch_text.stroke-9"),sQuery(id+"F24.wireOp",EDGE,"E25.sketch_text.stroke-10"),sQuery(id+"F24.wireOp",EDGE,"E25.sketch_text.stroke-11"),sQuery(id+"F24.wireOp",EDGE,"E25.sketch_text.stroke-12"),sQuery(id+"F24.wireOp",EDGE,"E25.sketch_text.stroke-13"),sQuery(id+"F24.wireOp",EDGE,"E25.sketch_text.stroke-14"),sQuery(id+"F24.wireOp",EDGE,"E25.sketch_text.stroke-15"),sQuery(id+"F24.wireOp",EDGE,"E25.sketch_text.stroke-16"),sQuery(id+"F24.wireOp",EDGE,"E25.sketch_text.stroke-17"),sQuery(id+"F24.wireOp",EDGE,"E25.sketch_text.stroke-18"),sQuery(id+"F24.wireOp",EDGE,"E25.sketch_text.stroke-19")])]});
            var Q2;
            Q2=makeQuery(id+"F25.opExtrude","SWEPT_BODY",BODY,{"disambiguationData":[OSD([sQuery(id+"F24.wireOp",EDGE,"E26.sketch_text.stroke-0"),sQuery(id+"F24.wireOp",EDGE,"E26.sketch_text.stroke-1"),sQuery(id+"F24.wireOp",EDGE,"E26.sketch_text.stroke-2"),sQuery(id+"F24.wireOp",EDGE,"E26.sketch_text.stroke-3"),sQuery(id+"F24.wireOp",EDGE,"E26.sketch_text.stroke-4"),sQuery(id+"F24.wireOp",EDGE,"E26.sketch_text.stroke-5"),sQuery(id+"F24.wireOp",EDGE,"E26.sketch_text.stroke-6"),sQuery(id+"F24.wireOp",EDGE,"E26.sketch_text.stroke-7"),sQuery(id+"F24.wireOp",EDGE,"E26.sketch_text.stroke-8"),sQuery(id+"F24.wireOp",EDGE,"E26.sketch_text.stroke-9"),sQuery(id+"F24.wireOp",EDGE,"E26.sketch_text.stroke-10"),sQuery(id+"F24.wireOp",EDGE,"E26.sketch_text.stroke-11"),sQuery(id+"F24.wireOp",EDGE,"E26.sketch_text.stroke-12"),sQuery(id+"F24.wireOp",EDGE,"E26.sketch_text.stroke-13"),sQuery(id+"F24.wireOp",EDGE,"E26.sketch_text.stroke-14"),sQuery(id+"F24.wireOp",EDGE,"E26.sketch_text.stroke-15"),sQuery(id+"F24.wireOp",EDGE,"E26.sketch_text.stroke-16"),sQuery(id+"F24.wireOp",EDGE,"E26.sketch_text.stroke-17"),sQuery(id+"F24.wireOp",EDGE,"E26.sketch_text.stroke-18"),sQuery(id+"F24.wireOp",EDGE,"E26.sketch_text.stroke-19"),sQuery(id+"F24.wireOp",EDGE,"E26.sketch_text.stroke-20"),sQuery(id+"F24.wireOp",EDGE,"E26.sketch_text.stroke-21"),sQuery(id+"F24.wireOp",EDGE,"E26.sketch_text.stroke-22"),sQuery(id+"F24.wireOp",EDGE,"E26.sketch_text.stroke-23"),sQuery(id+"F24.wireOp",EDGE,"E26.sketch_text.stroke-24"),sQuery(id+"F24.wireOp",EDGE,"E26.sketch_text.stroke-25"),sQuery(id+"F24.wireOp",EDGE,"E26.sketch_text.stroke-26"),sQuery(id+"F24.wireOp",EDGE,"E26.sketch_text.stroke-27")])]});
            var Q3;
            Q3=makeQuery(id+"F25.opExtrude","SWEPT_BODY",BODY,{"disambiguationData":[OSD([sQuery(id+"F24.wireOp",EDGE,"E27.sketch_text.stroke-0"),sQuery(id+"F24.wireOp",EDGE,"E27.sketch_text.stroke-1"),sQuery(id+"F24.wireOp",EDGE,"E27.sketch_text.stroke-2"),sQuery(id+"F24.wireOp",EDGE,"E27.sketch_text.stroke-3"),sQuery(id+"F24.wireOp",EDGE,"E27.sketch_text.stroke-4"),sQuery(id+"F24.wireOp",EDGE,"E27.sketch_text.stroke-5"),sQuery(id+"F24.wireOp",EDGE,"E27.sketch_text.stroke-6"),sQuery(id+"F24.wireOp",EDGE,"E27.sketch_text.stroke-7"),sQuery(id+"F24.wireOp",EDGE,"E27.sketch_text.stroke-8"),sQuery(id+"F24.wireOp",EDGE,"E27.sketch_text.stroke-9"),sQuery(id+"F24.wireOp",EDGE,"E27.sketch_text.stroke-10"),sQuery(id+"F24.wireOp",EDGE,"E27.sketch_text.stroke-11"),sQuery(id+"F24.wireOp",EDGE,"E27.sketch_text.stroke-12"),sQuery(id+"F24.wireOp",EDGE,"E27.sketch_text.stroke-13"),sQuery(id+"F24.wireOp",EDGE,"E27.sketch_text.stroke-14"),sQuery(id+"F24.wireOp",EDGE,"E27.sketch_text.stroke-15"),sQuery(id+"F24.wireOp",EDGE,"E27.sketch_text.stroke-16")])]});
            var Q4;
            Q4=makeQuery(id+"F25.opExtrude","SWEPT_BODY",BODY,{"disambiguationData":[OSD([sQuery(id+"F24.wireOp",EDGE,"E28.sketch_text.stroke-0"),sQuery(id+"F24.wireOp",EDGE,"E28.sketch_text.stroke-1"),sQuery(id+"F24.wireOp",EDGE,"E28.sketch_text.stroke-2"),sQuery(id+"F24.wireOp",EDGE,"E28.sketch_text.stroke-3"),sQuery(id+"F24.wireOp",EDGE,"E28.sketch_text.stroke-4"),sQuery(id+"F24.wireOp",EDGE,"E28.sketch_text.stroke-5"),sQuery(id+"F24.wireOp",EDGE,"E28.sketch_text.stroke-6"),sQuery(id+"F24.wireOp",EDGE,"E28.sketch_text.stroke-7"),sQuery(id+"F24.wireOp",EDGE,"E28.sketch_text.stroke-8"),sQuery(id+"F24.wireOp",EDGE,"E28.sketch_text.stroke-9"),sQuery(id+"F24.wireOp",EDGE,"E28.sketch_text.stroke-10"),sQuery(id+"F24.wireOp",EDGE,"E28.sketch_text.stroke-11"),sQuery(id+"F24.wireOp",EDGE,"E28.sketch_text.stroke-12"),sQuery(id+"F24.wireOp",EDGE,"E28.sketch_text.stroke-13"),sQuery(id+"F24.wireOp",EDGE,"E28.sketch_text.stroke-14"),sQuery(id+"F24.wireOp",EDGE,"E28.sketch_text.stroke-15"),sQuery(id+"F24.wireOp",EDGE,"E28.sketch_text.stroke-16"),sQuery(id+"F24.wireOp",EDGE,"E28.sketch_text.stroke-17"),sQuery(id+"F24.wireOp",EDGE,"E28.sketch_text.stroke-18")])]});
            var Q5;
            Q5=makeQuery(id+"F25.opExtrude","SWEPT_BODY",BODY,{"disambiguationData":[OSD([sQuery(id+"F24.wireOp",EDGE,"E29.sketch_text.stroke-0"),sQuery(id+"F24.wireOp",EDGE,"E29.sketch_text.stroke-1"),sQuery(id+"F24.wireOp",EDGE,"E29.sketch_text.stroke-2"),sQuery(id+"F24.wireOp",EDGE,"E29.sketch_text.stroke-3"),sQuery(id+"F24.wireOp",EDGE,"E29.sketch_text.stroke-4"),sQuery(id+"F24.wireOp",EDGE,"E29.sketch_text.stroke-5"),sQuery(id+"F24.wireOp",EDGE,"E29.sketch_text.stroke-6"),sQuery(id+"F24.wireOp",EDGE,"E29.sketch_text.stroke-7"),sQuery(id+"F24.wireOp",EDGE,"E29.sketch_text.stroke-8"),sQuery(id+"F24.wireOp",EDGE,"E29.sketch_text.stroke-9"),sQuery(id+"F24.wireOp",EDGE,"E29.sketch_text.stroke-10"),sQuery(id+"F24.wireOp",EDGE,"E29.sketch_text.stroke-11"),sQuery(id+"F24.wireOp",EDGE,"E29.sketch_text.stroke-12"),sQuery(id+"F24.wireOp",EDGE,"E29.sketch_text.stroke-13"),sQuery(id+"F24.wireOp",EDGE,"E29.sketch_text.stroke-14"),sQuery(id+"F24.wireOp",EDGE,"E29.sketch_text.stroke-15"),sQuery(id+"F24.wireOp",EDGE,"E29.sketch_text.stroke-16"),sQuery(id+"F24.wireOp",EDGE,"E29.sketch_text.stroke-17"),sQuery(id+"F24.wireOp",EDGE,"E29.sketch_text.stroke-18"),sQuery(id+"F24.wireOp",EDGE,"E29.sketch_text.stroke-19"),sQuery(id+"F24.wireOp",EDGE,"E29.sketch_text.stroke-20"),sQuery(id+"F24.wireOp",EDGE,"E29.sketch_text.stroke-21"),sQuery(id+"F24.wireOp",EDGE,"E29.sketch_text.stroke-22"),sQuery(id+"F24.wireOp",EDGE,"E29.sketch_text.stroke-23"),sQuery(id+"F24.wireOp",EDGE,"E29.sketch_text.stroke-24")])]});
            var Q6;
            Q6=makeQuery(id+"F25.opExtrude","SWEPT_BODY",BODY,{"disambiguationData":[OSD([sQuery(id+"F24.wireOp",EDGE,"E30.sketch_text.stroke-0"),sQuery(id+"F24.wireOp",EDGE,"E30.sketch_text.stroke-1"),sQuery(id+"F24.wireOp",EDGE,"E30.sketch_text.stroke-2"),sQuery(id+"F24.wireOp",EDGE,"E30.sketch_text.stroke-3"),sQuery(id+"F24.wireOp",EDGE,"E30.sketch_text.stroke-4"),sQuery(id+"F24.wireOp",EDGE,"E30.sketch_text.stroke-5"),sQuery(id+"F24.wireOp",EDGE,"E30.sketch_text.stroke-6")])]});
            var Q7;
            Q7=makeQuery(id+"F25.opExtrude","SWEPT_BODY",BODY,{"disambiguationData":[OSD([sQuery(id+"F24.wireOp",EDGE,"E31.sketch_text.stroke-0"),sQuery(id+"F24.wireOp",EDGE,"E31.sketch_text.stroke-1"),sQuery(id+"F24.wireOp",EDGE,"E31.sketch_text.stroke-2"),sQuery(id+"F24.wireOp",EDGE,"E31.sketch_text.stroke-3"),sQuery(id+"F24.wireOp",EDGE,"E31.sketch_text.stroke-4"),sQuery(id+"F24.wireOp",EDGE,"E31.sketch_text.stroke-5"),sQuery(id+"F24.wireOp",EDGE,"E31.sketch_text.stroke-6"),sQuery(id+"F24.wireOp",EDGE,"E31.sketch_text.stroke-7"),sQuery(id+"F24.wireOp",EDGE,"E31.sketch_text.stroke-8"),sQuery(id+"F24.wireOp",EDGE,"E31.sketch_text.stroke-9"),sQuery(id+"F24.wireOp",EDGE,"E31.sketch_text.stroke-10"),sQuery(id+"F24.wireOp",EDGE,"E31.sketch_text.stroke-11"),sQuery(id+"F24.wireOp",EDGE,"E31.sketch_text.stroke-12"),sQuery(id+"F24.wireOp",EDGE,"E31.sketch_text.stroke-13"),sQuery(id+"F24.wireOp",EDGE,"E31.sketch_text.stroke-14"),sQuery(id+"F24.wireOp",EDGE,"E31.sketch_text.stroke-15"),sQuery(id+"F24.wireOp",EDGE,"E31.sketch_text.stroke-16"),sQuery(id+"F24.wireOp",EDGE,"E31.sketch_text.stroke-17"),sQuery(id+"F24.wireOp",EDGE,"E31.sketch_text.stroke-18"),sQuery(id+"F24.wireOp",EDGE,"E31.sketch_text.stroke-19"),sQuery(id+"F24.wireOp",EDGE,"E31.sketch_text.stroke-20"),sQuery(id+"F24.wireOp",EDGE,"E31.sketch_text.stroke-21"),sQuery(id+"F24.wireOp",EDGE,"E31.sketch_text.stroke-22"),sQuery(id+"F24.wireOp",EDGE,"E31.sketch_text.stroke-23"),sQuery(id+"F24.wireOp",EDGE,"E31.sketch_text.stroke-24"),sQuery(id+"F24.wireOp",EDGE,"E31.sketch_text.stroke-25"),sQuery(id+"F24.wireOp",EDGE,"E31.sketch_text.stroke-26"),sQuery(id+"F24.wireOp",EDGE,"E31.sketch_text.stroke-27"),sQuery(id+"F24.wireOp",EDGE,"E31.sketch_text.stroke-28"),sQuery(id+"F24.wireOp",EDGE,"E31.sketch_text.stroke-29"),sQuery(id+"F24.wireOp",EDGE,"E31.sketch_text.stroke-30")])]});
            var Q8;
            Q8=makeQuery(id+"F25.opExtrude","SWEPT_BODY",BODY,{"disambiguationData":[OSD([sQuery(id+"F24.wireOp",EDGE,"E32.sketch_text.stroke-0"),sQuery(id+"F24.wireOp",EDGE,"E32.sketch_text.stroke-1"),sQuery(id+"F24.wireOp",EDGE,"E32.sketch_text.stroke-2"),sQuery(id+"F24.wireOp",EDGE,"E32.sketch_text.stroke-3"),sQuery(id+"F24.wireOp",EDGE,"E32.sketch_text.stroke-4"),sQuery(id+"F24.wireOp",EDGE,"E32.sketch_text.stroke-5"),sQuery(id+"F24.wireOp",EDGE,"E32.sketch_text.stroke-6"),sQuery(id+"F24.wireOp",EDGE,"E32.sketch_text.stroke-7"),sQuery(id+"F24.wireOp",EDGE,"E32.sketch_text.stroke-8"),sQuery(id+"F24.wireOp",EDGE,"E32.sketch_text.stroke-9"),sQuery(id+"F24.wireOp",EDGE,"E32.sketch_text.stroke-10"),sQuery(id+"F24.wireOp",EDGE,"E32.sketch_text.stroke-11"),sQuery(id+"F24.wireOp",EDGE,"E32.sketch_text.stroke-12"),sQuery(id+"F24.wireOp",EDGE,"E32.sketch_text.stroke-13"),sQuery(id+"F24.wireOp",EDGE,"E32.sketch_text.stroke-14"),sQuery(id+"F24.wireOp",EDGE,"E32.sketch_text.stroke-15"),sQuery(id+"F24.wireOp",EDGE,"E32.sketch_text.stroke-16"),sQuery(id+"F24.wireOp",EDGE,"E32.sketch_text.stroke-17"),sQuery(id+"F24.wireOp",EDGE,"E32.sketch_text.stroke-18"),sQuery(id+"F24.wireOp",EDGE,"E32.sketch_text.stroke-19"),sQuery(id+"F24.wireOp",EDGE,"E32.sketch_text.stroke-20"),sQuery(id+"F24.wireOp",EDGE,"E32.sketch_text.stroke-21"),sQuery(id+"F24.wireOp",EDGE,"E32.sketch_text.stroke-22"),sQuery(id+"F24.wireOp",EDGE,"E32.sketch_text.stroke-23"),sQuery(id+"F24.wireOp",EDGE,"E32.sketch_text.stroke-24"),sQuery(id+"F24.wireOp",EDGE,"E32.sketch_text.stroke-25")])]});
            var Q9;
            Q9=makeQuery(id+"F25.opExtrude","SWEPT_BODY",BODY,{"disambiguationData":[OSD([sQuery(id+"F24.wireOp",EDGE,"E33.sketch_text.stroke-0"),sQuery(id+"F24.wireOp",EDGE,"E33.sketch_text.stroke-1"),sQuery(id+"F24.wireOp",EDGE,"E33.sketch_text.stroke-2"),sQuery(id+"F24.wireOp",EDGE,"E33.sketch_text.stroke-3"),sQuery(id+"F24.wireOp",EDGE,"E33.sketch_text.stroke-4"),sQuery(id+"F24.wireOp",EDGE,"E33.sketch_text.stroke-5"),sQuery(id+"F24.wireOp",EDGE,"E33.sketch_text.stroke-6"),sQuery(id+"F24.wireOp",EDGE,"E33.sketch_text.stroke-7"),sQuery(id+"F24.wireOp",EDGE,"E33.sketch_text.stroke-8")])]});
            var Q10;
            Q10=makeQuery(id+"F25.opExtrude","SWEPT_BODY",BODY,{"disambiguationData":[OSD([sQuery(id+"F24.wireOp",EDGE,"E33.sketch_text.stroke-9"),sQuery(id+"F24.wireOp",EDGE,"E33.sketch_text.stroke-10"),sQuery(id+"F24.wireOp",EDGE,"E33.sketch_text.stroke-11"),sQuery(id+"F24.wireOp",EDGE,"E33.sketch_text.stroke-12"),sQuery(id+"F24.wireOp",EDGE,"E33.sketch_text.stroke-13"),sQuery(id+"F24.wireOp",EDGE,"E33.sketch_text.stroke-14"),sQuery(id+"F24.wireOp",EDGE,"E33.sketch_text.stroke-15"),sQuery(id+"F24.wireOp",EDGE,"E33.sketch_text.stroke-16"),sQuery(id+"F24.wireOp",EDGE,"E33.sketch_text.stroke-17"),sQuery(id+"F24.wireOp",EDGE,"E33.sketch_text.stroke-18"),sQuery(id+"F24.wireOp",EDGE,"E33.sketch_text.stroke-19"),sQuery(id+"F24.wireOp",EDGE,"E33.sketch_text.stroke-20"),sQuery(id+"F24.wireOp",EDGE,"E33.sketch_text.stroke-21"),sQuery(id+"F24.wireOp",EDGE,"E33.sketch_text.stroke-22"),sQuery(id+"F24.wireOp",EDGE,"E33.sketch_text.stroke-23"),sQuery(id+"F24.wireOp",EDGE,"E33.sketch_text.stroke-24")])]});
            var Q11;
            Q11=makeQuery(id+"F25.opExtrude","SWEPT_BODY",BODY,{"disambiguationData":[OSD([sQuery(id+"F24.wireOp",EDGE,"E34.bottom"),sQuery(id+"F24.wireOp",EDGE,"E34.top"),sQuery(id+"F24.wireOp",EDGE,"E34.left"),sQuery(id+"F24.wireOp",EDGE,"E34.right")])]});
            var Q12;
            Q12=makeQuery(id+"F25.opExtrude","SWEPT_BODY",BODY,{"disambiguationData":[OSD([sQuery(id+"F24.wireOp",EDGE,"E36.1.0.0"),sQuery(id+"F24.wireOp",EDGE,"E36.1.0.1"),sQuery(id+"F24.wireOp",EDGE,"E36.1.0.2"),sQuery(id+"F24.wireOp",EDGE,"E36.1.0.3")])]});
            var Q13;
            Q13=makeQuery(id+"F25.opExtrude","SWEPT_BODY",BODY,{"disambiguationData":[OSD([sQuery(id+"F24.wireOp",EDGE,"E36.2.0.0"),sQuery(id+"F24.wireOp",EDGE,"E36.2.0.1"),sQuery(id+"F24.wireOp",EDGE,"E36.2.0.2"),sQuery(id+"F24.wireOp",EDGE,"E36.2.0.3")])]});
            var Q14;
            Q14=makeQuery(id+"F25.opExtrude","SWEPT_BODY",BODY,{"disambiguationData":[OSD([sQuery(id+"F24.wireOp",EDGE,"E36.3.0.0"),sQuery(id+"F24.wireOp",EDGE,"E36.3.0.1"),sQuery(id+"F24.wireOp",EDGE,"E36.3.0.2"),sQuery(id+"F24.wireOp",EDGE,"E36.3.0.3")])]});
            var Q15;
            Q15=makeQuery(id+"F25.opExtrude","SWEPT_BODY",BODY,{"disambiguationData":[OSD([sQuery(id+"F24.wireOp",EDGE,"E36.4.0.0"),sQuery(id+"F24.wireOp",EDGE,"E36.4.0.1"),sQuery(id+"F24.wireOp",EDGE,"E36.4.0.2"),sQuery(id+"F24.wireOp",EDGE,"E36.4.0.3")])]});
            var Q16;
            Q16=makeQuery(id+"F25.opExtrude","SWEPT_BODY",BODY,{"disambiguationData":[OSD([sQuery(id+"F24.wireOp",EDGE,"E36.5.0.0"),sQuery(id+"F24.wireOp",EDGE,"E36.5.0.1"),sQuery(id+"F24.wireOp",EDGE,"E36.5.0.2"),sQuery(id+"F24.wireOp",EDGE,"E36.5.0.3")])]});
            var Q17;
            Q17=makeQuery(id+"F25.opExtrude","SWEPT_BODY",BODY,{"disambiguationData":[OSD([sQuery(id+"F24.wireOp",EDGE,"E36.6.0.0"),sQuery(id+"F24.wireOp",EDGE,"E36.6.0.1"),sQuery(id+"F24.wireOp",EDGE,"E36.6.0.2"),sQuery(id+"F24.wireOp",EDGE,"E36.6.0.3")])]});
            var Q18;
            Q18=makeQuery(id+"F25.opExtrude","SWEPT_BODY",BODY,{"disambiguationData":[OSD([sQuery(id+"F24.wireOp",EDGE,"E36.7.0.0"),sQuery(id+"F24.wireOp",EDGE,"E36.7.0.1"),sQuery(id+"F24.wireOp",EDGE,"E36.7.0.2"),sQuery(id+"F24.wireOp",EDGE,"E36.7.0.3")])]});
            var Q19;
            Q19=makeQuery(id+"F25.opExtrude","SWEPT_BODY",BODY,{"disambiguationData":[OSD([sQuery(id+"F24.wireOp",EDGE,"E36.8.0.0"),sQuery(id+"F24.wireOp",EDGE,"E36.8.0.1"),sQuery(id+"F24.wireOp",EDGE,"E36.8.0.2"),sQuery(id+"F24.wireOp",EDGE,"E36.8.0.3")])]});
            var Q20;
            Q20=makeQuery(id+"F25.opExtrude","SWEPT_BODY",BODY,{"disambiguationData":[OSD([sQuery(id+"F24.wireOp",EDGE,"E36.9.0.0"),sQuery(id+"F24.wireOp",EDGE,"E36.9.0.1"),sQuery(id+"F24.wireOp",EDGE,"E36.9.0.2"),sQuery(id+"F24.wireOp",EDGE,"E36.9.0.3")])]});
            var Q21;
            Q21=sQuery(id+"F12.wireOp",EDGE,"E11");
            circularPattern(context, id + "F27", {"entities" : qUnion([Q0, Q1, Q2, Q3, Q4, Q5, Q6, Q7, Q8, Q9, Q10, Q11, Q12, Q13, Q14, Q15, Q16, Q17, Q18, Q19, Q20]), "axis" : qUnion([Q21]), "angle" : 90 * degree, "instanceCount" : 2});
        }
        {
            var Q0;
            Q0=makeQuery(id+"F19.opBoolean","MERGE",FACE,{"derivedFrom":[makeQuery(id+"F1.opExtrude","SWEPT_FACE",FACE,{"disambiguationData":[OSD([sQuery(id+"F0.wireOp",EDGE,"E1.right")])]}),makeQuery(id+"F15.opBoolean","MERGE",FACE,{"derivedFrom":[makeQuery(id+"F5.opExtrude","SWEPT_FACE",FACE,{"disambiguationData":[OSD([sQuery(id+"F4.wireOp",EDGE,"E4.9.0.2")])]}),makeQuery(id+"F7.opExtrude","SWEPT_FACE",FACE,{"disambiguationData":[OSD([sQuery(id+"F6.wireOp",EDGE,"E6.9.0.0")])]}),makeQuery(id+"F9.opExtrude","SWEPT_FACE",FACE,{"disambiguationData":[OSD([sQuery(id+"F8.wireOp",EDGE,"E8.9.0.2")])]}),makeQuery(id+"F11.opExtrude","SWEPT_FACE",FACE,{"disambiguationData":[OSD([sQuery(id+"F10.wireOp",EDGE,"E10.9.0.2")])]})]})]});
            var sketch = newSketch(context, id + "F28", { "sketchPlane" : qUnion([Q0])});
            skText(sketch, "E37", { "text": "X", "fontName": "OpenSans-Regular.ttf"});
            const initialGuessF28  = {"E37": [-0.00663, -0.00824, 1, 0, 0.01666]};
            skSetInitialGuess(sketch, initialGuessF28);
            skSolve(sketch);
        }
        {
            var Q0;
            Q0 = qSketchRegion(id + "F28", true);
            extrude(context, id + "F29", {"entities" : qUnion([Q0]), "depth" : 1.52 * mm});
        }
        {
            var Q0;
            Q0=makeQuery(id+"F19.opBoolean","MERGE",FACE,{"derivedFrom":[makeQuery(id+"F1.opExtrude","SWEPT_FACE",FACE,{"disambiguationData":[OSD([sQuery(id+"F0.wireOp",EDGE,"E0.bottom")])]}),makeQuery(id+"F18.opPattern","COPY",FACE,{"derivedFrom":makeQuery(id+"F15.opBoolean","MERGE",FACE,{"derivedFrom":[makeQuery(id+"F5.opExtrude","SWEPT_FACE",FACE,{"disambiguationData":[OSD([sQuery(id+"F4.wireOp",EDGE,"E4.9.0.2")])]}),makeQuery(id+"F7.opExtrude","SWEPT_FACE",FACE,{"disambiguationData":[OSD([sQuery(id+"F6.wireOp",EDGE,"E6.9.0.0")])]}),makeQuery(id+"F9.opExtrude","SWEPT_FACE",FACE,{"disambiguationData":[OSD([sQuery(id+"F8.wireOp",EDGE,"E8.9.0.2")])]}),makeQuery(id+"F11.opExtrude","SWEPT_FACE",FACE,{"disambiguationData":[OSD([sQuery(id+"F10.wireOp",EDGE,"E10.9.0.2")])]})]}),"instanceName":"1"})]});
            var sketch = newSketch(context, id + "F30", { "sketchPlane" : qUnion([Q0])});
            skText(sketch, "E38", { "text": "Y", "fontName": "OpenSans-Regular.ttf"});
            const initialGuessF30  = {"E38": [-0.00601, -0.0077, 1, 0, 0.01546]};
            skSetInitialGuess(sketch, initialGuessF30);
            skSolve(sketch);
        }
        {
            var Q0;
            Q0 = qSketchRegion(id + "F30", true);
            extrude(context, id + "F31", {"entities" : qUnion([Q0]), "depth" : 1.52 * mm});
        }
        {
            var Q0;
            Q0=makeQuery(id+"F19.opBoolean","MERGE",FACE,{"derivedFrom":[makeQuery(id+"F3.opExtrude","CAP_FACE",FACE,{"disambiguationData":[OSD([sQuery(id+"F2.wireOp",EDGE,"E2.bottom"),sQuery(id+"F2.wireOp",EDGE,"E2.top"),sQuery(id+"F2.wireOp",EDGE,"E2.left"),sQuery(id+"F2.wireOp",EDGE,"E2.right")])],"isStart":false}),makeQuery(id+"F16.opPattern","COPY",FACE,{"derivedFrom":makeQuery(id+"F15.opBoolean","MERGE",FACE,{"derivedFrom":[makeQuery(id+"F5.opExtrude","SWEPT_FACE",FACE,{"disambiguationData":[OSD([sQuery(id+"F4.wireOp",EDGE,"E4.9.0.2")])]}),makeQuery(id+"F7.opExtrude","SWEPT_FACE",FACE,{"disambiguationData":[OSD([sQuery(id+"F6.wireOp",EDGE,"E6.9.0.0")])]}),makeQuery(id+"F9.opExtrude","SWEPT_FACE",FACE,{"disambiguationData":[OSD([sQuery(id+"F8.wireOp",EDGE,"E8.9.0.2")])]}),makeQuery(id+"F11.opExtrude","SWEPT_FACE",FACE,{"disambiguationData":[OSD([sQuery(id+"F10.wireOp",EDGE,"E10.9.0.2")])]})]}),"instanceName":"1"})]});
            var sketch = newSketch(context, id + "F32", { "sketchPlane" : qUnion([Q0])});
            skText(sketch, "E39", { "text": "Z\n", "fontName": "OpenSans-Regular.ttf"});
            const initialGuessF32  = {"E39": [-0.00536, -0.00728, 1, 0, 0.01455]};
            skSetInitialGuess(sketch, initialGuessF32);
            skSolve(sketch);
        }
        {
            var Q0;
            Q0 = qSketchRegion(id + "F32", true);
            extrude(context, id + "F33", {"entities" : qUnion([Q0]), "depth" : 1.52 * mm});
        }
        {
            var Q0;
            Q0=makeQuery(id+"F33.opExtrude","SWEPT_BODY",BODY,{"disambiguationData":[OSD([sQuery(id+"F32.wireOp",EDGE,"E39.sketch_text.stroke-0"),sQuery(id+"F32.wireOp",EDGE,"E39.sketch_text.stroke-1"),sQuery(id+"F32.wireOp",EDGE,"E39.sketch_text.stroke-2"),sQuery(id+"F32.wireOp",EDGE,"E39.sketch_text.stroke-3"),sQuery(id+"F32.wireOp",EDGE,"E39.sketch_text.stroke-4"),sQuery(id+"F32.wireOp",EDGE,"E39.sketch_text.stroke-5"),sQuery(id+"F32.wireOp",EDGE,"E39.sketch_text.stroke-6"),sQuery(id+"F32.wireOp",EDGE,"E39.sketch_text.stroke-7"),sQuery(id+"F32.wireOp",EDGE,"E39.sketch_text.stroke-8"),sQuery(id+"F32.wireOp",EDGE,"E39.sketch_text.stroke-9")])]});
            var Q1;
            Q1=qCreatedBy(makeId("Front.planeOp"),FACE);
            mirror(context, id + "F34", {"operationType" : NewBodyOperationType.ADD, "entities" : qUnion([Q0]), "mirrorPlane" : qUnion([Q1])});
        }
        {
            var Q0;
            Q0=makeQuery(id+"F31.opExtrude","SWEPT_BODY",BODY,{"disambiguationData":[OSD([sQuery(id+"F30.wireOp",EDGE,"E38.sketch_text.stroke-0"),sQuery(id+"F30.wireOp",EDGE,"E38.sketch_text.stroke-1"),sQuery(id+"F30.wireOp",EDGE,"E38.sketch_text.stroke-2"),sQuery(id+"F30.wireOp",EDGE,"E38.sketch_text.stroke-3"),sQuery(id+"F30.wireOp",EDGE,"E38.sketch_text.stroke-4"),sQuery(id+"F30.wireOp",EDGE,"E38.sketch_text.stroke-5"),sQuery(id+"F30.wireOp",EDGE,"E38.sketch_text.stroke-6"),sQuery(id+"F30.wireOp",EDGE,"E38.sketch_text.stroke-7"),sQuery(id+"F30.wireOp",EDGE,"E38.sketch_text.stroke-8")])]});
            var Q1;
            Q1=qCreatedBy(makeId("Top.planeOp"),FACE);
            mirror(context, id + "F35", {"operationType" : NewBodyOperationType.ADD, "entities" : qUnion([Q0]), "mirrorPlane" : qUnion([Q1])});
        }
        {
            var Q0;
            Q0=makeQuery(id+"F29.opExtrude","SWEPT_BODY",BODY,{"disambiguationData":[OSD([sQuery(id+"F28.wireOp",EDGE,"E37.sketch_text.stroke-0"),sQuery(id+"F28.wireOp",EDGE,"E37.sketch_text.stroke-1"),sQuery(id+"F28.wireOp",EDGE,"E37.sketch_text.stroke-2"),sQuery(id+"F28.wireOp",EDGE,"E37.sketch_text.stroke-3"),sQuery(id+"F28.wireOp",EDGE,"E37.sketch_text.stroke-4"),sQuery(id+"F28.wireOp",EDGE,"E37.sketch_text.stroke-5"),sQuery(id+"F28.wireOp",EDGE,"E37.sketch_text.stroke-6"),sQuery(id+"F28.wireOp",EDGE,"E37.sketch_text.stroke-7"),sQuery(id+"F28.wireOp",EDGE,"E37.sketch_text.stroke-8"),sQuery(id+"F28.wireOp",EDGE,"E37.sketch_text.stroke-9"),sQuery(id+"F28.wireOp",EDGE,"E37.sketch_text.stroke-10"),sQuery(id+"F28.wireOp",EDGE,"E37.sketch_text.stroke-11")])]});
            var Q1;
            Q1=qCreatedBy(makeId("Right.planeOp"),FACE);
            mirror(context, id + "F36", {"operationType" : NewBodyOperationType.ADD, "entities" : qUnion([Q0]), "mirrorPlane" : qUnion([Q1])});
        }
        {
            var Q0;
            Q0=makeQuery(id+"F21.opExtrude","SWEPT_BODY",BODY,{"disambiguationData":[OSD([sQuery(id+"F20.wireOp",EDGE,"E14.sketch_text.stroke-0"),sQuery(id+"F20.wireOp",EDGE,"E14.sketch_text.stroke-1"),sQuery(id+"F20.wireOp",EDGE,"E14.sketch_text.stroke-2"),sQuery(id+"F20.wireOp",EDGE,"E14.sketch_text.stroke-3"),sQuery(id+"F20.wireOp",EDGE,"E14.sketch_text.stroke-4"),sQuery(id+"F20.wireOp",EDGE,"E14.sketch_text.stroke-5"),sQuery(id+"F20.wireOp",EDGE,"E14.sketch_text.stroke-6"),sQuery(id+"F20.wireOp",EDGE,"E14.sketch_text.stroke-7"),sQuery(id+"F20.wireOp",EDGE,"E14.sketch_text.stroke-8")])]});
            var Q1;
            Q1=makeQuery(id+"F21.opExtrude","SWEPT_BODY",BODY,{"disambiguationData":[OSD([sQuery(id+"F20.wireOp",EDGE,"E15.sketch_text.stroke-0"),sQuery(id+"F20.wireOp",EDGE,"E15.sketch_text.stroke-1"),sQuery(id+"F20.wireOp",EDGE,"E15.sketch_text.stroke-2"),sQuery(id+"F20.wireOp",EDGE,"E15.sketch_text.stroke-3"),sQuery(id+"F20.wireOp",EDGE,"E15.sketch_text.stroke-4"),sQuery(id+"F20.wireOp",EDGE,"E15.sketch_text.stroke-5"),sQuery(id+"F20.wireOp",EDGE,"E15.sketch_text.stroke-6"),sQuery(id+"F20.wireOp",EDGE,"E15.sketch_text.stroke-7"),sQuery(id+"F20.wireOp",EDGE,"E15.sketch_text.stroke-8"),sQuery(id+"F20.wireOp",EDGE,"E15.sketch_text.stroke-9"),sQuery(id+"F20.wireOp",EDGE,"E15.sketch_text.stroke-10"),sQuery(id+"F20.wireOp",EDGE,"E15.sketch_text.stroke-11"),sQuery(id+"F20.wireOp",EDGE,"E15.sketch_text.stroke-12"),sQuery(id+"F20.wireOp",EDGE,"E15.sketch_text.stroke-13"),sQuery(id+"F20.wireOp",EDGE,"E15.sketch_text.stroke-14"),sQuery(id+"F20.wireOp",EDGE,"E15.sketch_text.stroke-15"),sQuery(id+"F20.wireOp",EDGE,"E15.sketch_text.stroke-16"),sQuery(id+"F20.wireOp",EDGE,"E15.sketch_text.stroke-17"),sQuery(id+"F20.wireOp",EDGE,"E15.sketch_text.stroke-18"),sQuery(id+"F20.wireOp",EDGE,"E15.sketch_text.stroke-19")])]});
            var Q2;
            Q2=makeQuery(id+"F21.opExtrude","SWEPT_BODY",BODY,{"disambiguationData":[OSD([sQuery(id+"F20.wireOp",EDGE,"E16.sketch_text.stroke-0"),sQuery(id+"F20.wireOp",EDGE,"E16.sketch_text.stroke-1"),sQuery(id+"F20.wireOp",EDGE,"E16.sketch_text.stroke-2"),sQuery(id+"F20.wireOp",EDGE,"E16.sketch_text.stroke-3"),sQuery(id+"F20.wireOp",EDGE,"E16.sketch_text.stroke-4"),sQuery(id+"F20.wireOp",EDGE,"E16.sketch_text.stroke-5"),sQuery(id+"F20.wireOp",EDGE,"E16.sketch_text.stroke-6"),sQuery(id+"F20.wireOp",EDGE,"E16.sketch_text.stroke-7"),sQuery(id+"F20.wireOp",EDGE,"E16.sketch_text.stroke-8"),sQuery(id+"F20.wireOp",EDGE,"E16.sketch_text.stroke-9"),sQuery(id+"F20.wireOp",EDGE,"E16.sketch_text.stroke-10"),sQuery(id+"F20.wireOp",EDGE,"E16.sketch_text.stroke-11"),sQuery(id+"F20.wireOp",EDGE,"E16.sketch_text.stroke-12"),sQuery(id+"F20.wireOp",EDGE,"E16.sketch_text.stroke-13"),sQuery(id+"F20.wireOp",EDGE,"E16.sketch_text.stroke-14"),sQuery(id+"F20.wireOp",EDGE,"E16.sketch_text.stroke-15"),sQuery(id+"F20.wireOp",EDGE,"E16.sketch_text.stroke-16"),sQuery(id+"F20.wireOp",EDGE,"E16.sketch_text.stroke-17"),sQuery(id+"F20.wireOp",EDGE,"E16.sketch_text.stroke-18"),sQuery(id+"F20.wireOp",EDGE,"E16.sketch_text.stroke-19"),sQuery(id+"F20.wireOp",EDGE,"E16.sketch_text.stroke-20"),sQuery(id+"F20.wireOp",EDGE,"E16.sketch_text.stroke-21"),sQuery(id+"F20.wireOp",EDGE,"E16.sketch_text.stroke-22"),sQuery(id+"F20.wireOp",EDGE,"E16.sketch_text.stroke-23"),sQuery(id+"F20.wireOp",EDGE,"E16.sketch_text.stroke-24"),sQuery(id+"F20.wireOp",EDGE,"E16.sketch_text.stroke-25"),sQuery(id+"F20.wireOp",EDGE,"E16.sketch_text.stroke-26"),sQuery(id+"F20.wireOp",EDGE,"E16.sketch_text.stroke-27")])]});
            var Q3;
            Q3=makeQuery(id+"F21.opExtrude","SWEPT_BODY",BODY,{"disambiguationData":[OSD([sQuery(id+"F20.wireOp",EDGE,"E17.sketch_text.stroke-0"),sQuery(id+"F20.wireOp",EDGE,"E17.sketch_text.stroke-1"),sQuery(id+"F20.wireOp",EDGE,"E17.sketch_text.stroke-2"),sQuery(id+"F20.wireOp",EDGE,"E17.sketch_text.stroke-3"),sQuery(id+"F20.wireOp",EDGE,"E17.sketch_text.stroke-4"),sQuery(id+"F20.wireOp",EDGE,"E17.sketch_text.stroke-5"),sQuery(id+"F20.wireOp",EDGE,"E17.sketch_text.stroke-6"),sQuery(id+"F20.wireOp",EDGE,"E17.sketch_text.stroke-7"),sQuery(id+"F20.wireOp",EDGE,"E17.sketch_text.stroke-8"),sQuery(id+"F20.wireOp",EDGE,"E17.sketch_text.stroke-9"),sQuery(id+"F20.wireOp",EDGE,"E17.sketch_text.stroke-10"),sQuery(id+"F20.wireOp",EDGE,"E17.sketch_text.stroke-11"),sQuery(id+"F20.wireOp",EDGE,"E17.sketch_text.stroke-12"),sQuery(id+"F20.wireOp",EDGE,"E17.sketch_text.stroke-13"),sQuery(id+"F20.wireOp",EDGE,"E17.sketch_text.stroke-14"),sQuery(id+"F20.wireOp",EDGE,"E17.sketch_text.stroke-15"),sQuery(id+"F20.wireOp",EDGE,"E17.sketch_text.stroke-16")])]});
            var Q4;
            Q4=makeQuery(id+"F21.opExtrude","SWEPT_BODY",BODY,{"disambiguationData":[OSD([sQuery(id+"F20.wireOp",EDGE,"E18.sketch_text.stroke-0"),sQuery(id+"F20.wireOp",EDGE,"E18.sketch_text.stroke-1"),sQuery(id+"F20.wireOp",EDGE,"E18.sketch_text.stroke-2"),sQuery(id+"F20.wireOp",EDGE,"E18.sketch_text.stroke-3"),sQuery(id+"F20.wireOp",EDGE,"E18.sketch_text.stroke-4"),sQuery(id+"F20.wireOp",EDGE,"E18.sketch_text.stroke-5"),sQuery(id+"F20.wireOp",EDGE,"E18.sketch_text.stroke-6"),sQuery(id+"F20.wireOp",EDGE,"E18.sketch_text.stroke-7"),sQuery(id+"F20.wireOp",EDGE,"E18.sketch_text.stroke-8"),sQuery(id+"F20.wireOp",EDGE,"E18.sketch_text.stroke-9"),sQuery(id+"F20.wireOp",EDGE,"E18.sketch_text.stroke-10"),sQuery(id+"F20.wireOp",EDGE,"E18.sketch_text.stroke-11"),sQuery(id+"F20.wireOp",EDGE,"E18.sketch_text.stroke-12"),sQuery(id+"F20.wireOp",EDGE,"E18.sketch_text.stroke-13"),sQuery(id+"F20.wireOp",EDGE,"E18.sketch_text.stroke-14"),sQuery(id+"F20.wireOp",EDGE,"E18.sketch_text.stroke-15"),sQuery(id+"F20.wireOp",EDGE,"E18.sketch_text.stroke-16"),sQuery(id+"F20.wireOp",EDGE,"E18.sketch_text.stroke-17"),sQuery(id+"F20.wireOp",EDGE,"E18.sketch_text.stroke-18")])]});
            var Q5;
            Q5=makeQuery(id+"F21.opExtrude","SWEPT_BODY",BODY,{"disambiguationData":[OSD([sQuery(id+"F20.wireOp",EDGE,"E19.sketch_text.stroke-0"),sQuery(id+"F20.wireOp",EDGE,"E19.sketch_text.stroke-1"),sQuery(id+"F20.wireOp",EDGE,"E19.sketch_text.stroke-2"),sQuery(id+"F20.wireOp",EDGE,"E19.sketch_text.stroke-3"),sQuery(id+"F20.wireOp",EDGE,"E19.sketch_text.stroke-4"),sQuery(id+"F20.wireOp",EDGE,"E19.sketch_text.stroke-5"),sQuery(id+"F20.wireOp",EDGE,"E19.sketch_text.stroke-6"),sQuery(id+"F20.wireOp",EDGE,"E19.sketch_text.stroke-7"),sQuery(id+"F20.wireOp",EDGE,"E19.sketch_text.stroke-8"),sQuery(id+"F20.wireOp",EDGE,"E19.sketch_text.stroke-9"),sQuery(id+"F20.wireOp",EDGE,"E19.sketch_text.stroke-10"),sQuery(id+"F20.wireOp",EDGE,"E19.sketch_text.stroke-11"),sQuery(id+"F20.wireOp",EDGE,"E19.sketch_text.stroke-12"),sQuery(id+"F20.wireOp",EDGE,"E19.sketch_text.stroke-13"),sQuery(id+"F20.wireOp",EDGE,"E19.sketch_text.stroke-14"),sQuery(id+"F20.wireOp",EDGE,"E19.sketch_text.stroke-15"),sQuery(id+"F20.wireOp",EDGE,"E19.sketch_text.stroke-16"),sQuery(id+"F20.wireOp",EDGE,"E19.sketch_text.stroke-17"),sQuery(id+"F20.wireOp",EDGE,"E19.sketch_text.stroke-18"),sQuery(id+"F20.wireOp",EDGE,"E19.sketch_text.stroke-19"),sQuery(id+"F20.wireOp",EDGE,"E19.sketch_text.stroke-20"),sQuery(id+"F20.wireOp",EDGE,"E19.sketch_text.stroke-21"),sQuery(id+"F20.wireOp",EDGE,"E19.sketch_text.stroke-22"),sQuery(id+"F20.wireOp",EDGE,"E19.sketch_text.stroke-23"),sQuery(id+"F20.wireOp",EDGE,"E19.sketch_text.stroke-24")])]});
            var Q6;
            Q6=makeQuery(id+"F21.opExtrude","SWEPT_BODY",BODY,{"disambiguationData":[OSD([sQuery(id+"F20.wireOp",EDGE,"E20.sketch_text.stroke-0"),sQuery(id+"F20.wireOp",EDGE,"E20.sketch_text.stroke-1"),sQuery(id+"F20.wireOp",EDGE,"E20.sketch_text.stroke-2"),sQuery(id+"F20.wireOp",EDGE,"E20.sketch_text.stroke-3"),sQuery(id+"F20.wireOp",EDGE,"E20.sketch_text.stroke-4"),sQuery(id+"F20.wireOp",EDGE,"E20.sketch_text.stroke-5"),sQuery(id+"F20.wireOp",EDGE,"E20.sketch_text.stroke-6")])]});
            var Q7;
            Q7=makeQuery(id+"F21.opExtrude","SWEPT_BODY",BODY,{"disambiguationData":[OSD([sQuery(id+"F20.wireOp",EDGE,"E21.sketch_text.stroke-0"),sQuery(id+"F20.wireOp",EDGE,"E21.sketch_text.stroke-1"),sQuery(id+"F20.wireOp",EDGE,"E21.sketch_text.stroke-2"),sQuery(id+"F20.wireOp",EDGE,"E21.sketch_text.stroke-3"),sQuery(id+"F20.wireOp",EDGE,"E21.sketch_text.stroke-4"),sQuery(id+"F20.wireOp",EDGE,"E21.sketch_text.stroke-5"),sQuery(id+"F20.wireOp",EDGE,"E21.sketch_text.stroke-6"),sQuery(id+"F20.wireOp",EDGE,"E21.sketch_text.stroke-7"),sQuery(id+"F20.wireOp",EDGE,"E21.sketch_text.stroke-8"),sQuery(id+"F20.wireOp",EDGE,"E21.sketch_text.stroke-9"),sQuery(id+"F20.wireOp",EDGE,"E21.sketch_text.stroke-10"),sQuery(id+"F20.wireOp",EDGE,"E21.sketch_text.stroke-11"),sQuery(id+"F20.wireOp",EDGE,"E21.sketch_text.stroke-12"),sQuery(id+"F20.wireOp",EDGE,"E21.sketch_text.stroke-13"),sQuery(id+"F20.wireOp",EDGE,"E21.sketch_text.stroke-14"),sQuery(id+"F20.wireOp",EDGE,"E21.sketch_text.stroke-15"),sQuery(id+"F20.wireOp",EDGE,"E21.sketch_text.stroke-16"),sQuery(id+"F20.wireOp",EDGE,"E21.sketch_text.stroke-17"),sQuery(id+"F20.wireOp",EDGE,"E21.sketch_text.stroke-18"),sQuery(id+"F20.wireOp",EDGE,"E21.sketch_text.stroke-19"),sQuery(id+"F20.wireOp",EDGE,"E21.sketch_text.stroke-20"),sQuery(id+"F20.wireOp",EDGE,"E21.sketch_text.stroke-21"),sQuery(id+"F20.wireOp",EDGE,"E21.sketch_text.stroke-22"),sQuery(id+"F20.wireOp",EDGE,"E21.sketch_text.stroke-23"),sQuery(id+"F20.wireOp",EDGE,"E21.sketch_text.stroke-24"),sQuery(id+"F20.wireOp",EDGE,"E21.sketch_text.stroke-25"),sQuery(id+"F20.wireOp",EDGE,"E21.sketch_text.stroke-26"),sQuery(id+"F20.wireOp",EDGE,"E21.sketch_text.stroke-27"),sQuery(id+"F20.wireOp",EDGE,"E21.sketch_text.stroke-28"),sQuery(id+"F20.wireOp",EDGE,"E21.sketch_text.stroke-29"),sQuery(id+"F20.wireOp",EDGE,"E21.sketch_text.stroke-30")])]});
            var Q8;
            Q8=makeQuery(id+"F21.opExtrude","SWEPT_BODY",BODY,{"disambiguationData":[OSD([sQuery(id+"F20.wireOp",EDGE,"E22.sketch_text.stroke-0"),sQuery(id+"F20.wireOp",EDGE,"E22.sketch_text.stroke-1"),sQuery(id+"F20.wireOp",EDGE,"E22.sketch_text.stroke-2"),sQuery(id+"F20.wireOp",EDGE,"E22.sketch_text.stroke-3"),sQuery(id+"F20.wireOp",EDGE,"E22.sketch_text.stroke-4"),sQuery(id+"F20.wireOp",EDGE,"E22.sketch_text.stroke-5"),sQuery(id+"F20.wireOp",EDGE,"E22.sketch_text.stroke-6"),sQuery(id+"F20.wireOp",EDGE,"E22.sketch_text.stroke-7"),sQuery(id+"F20.wireOp",EDGE,"E22.sketch_text.stroke-8"),sQuery(id+"F20.wireOp",EDGE,"E22.sketch_text.stroke-9"),sQuery(id+"F20.wireOp",EDGE,"E22.sketch_text.stroke-10"),sQuery(id+"F20.wireOp",EDGE,"E22.sketch_text.stroke-11"),sQuery(id+"F20.wireOp",EDGE,"E22.sketch_text.stroke-12"),sQuery(id+"F20.wireOp",EDGE,"E22.sketch_text.stroke-13"),sQuery(id+"F20.wireOp",EDGE,"E22.sketch_text.stroke-14"),sQuery(id+"F20.wireOp",EDGE,"E22.sketch_text.stroke-15"),sQuery(id+"F20.wireOp",EDGE,"E22.sketch_text.stroke-16"),sQuery(id+"F20.wireOp",EDGE,"E22.sketch_text.stroke-17"),sQuery(id+"F20.wireOp",EDGE,"E22.sketch_text.stroke-18"),sQuery(id+"F20.wireOp",EDGE,"E22.sketch_text.stroke-19"),sQuery(id+"F20.wireOp",EDGE,"E22.sketch_text.stroke-20"),sQuery(id+"F20.wireOp",EDGE,"E22.sketch_text.stroke-21"),sQuery(id+"F20.wireOp",EDGE,"E22.sketch_text.stroke-22"),sQuery(id+"F20.wireOp",EDGE,"E22.sketch_text.stroke-23"),sQuery(id+"F20.wireOp",EDGE,"E22.sketch_text.stroke-24"),sQuery(id+"F20.wireOp",EDGE,"E22.sketch_text.stroke-25")])]});
            var Q9;
            Q9=makeQuery(id+"F21.opExtrude","SWEPT_BODY",BODY,{"disambiguationData":[OSD([sQuery(id+"F20.wireOp",EDGE,"E23.sketch_text.stroke-0"),sQuery(id+"F20.wireOp",EDGE,"E23.sketch_text.stroke-1"),sQuery(id+"F20.wireOp",EDGE,"E23.sketch_text.stroke-2"),sQuery(id+"F20.wireOp",EDGE,"E23.sketch_text.stroke-3"),sQuery(id+"F20.wireOp",EDGE,"E23.sketch_text.stroke-4"),sQuery(id+"F20.wireOp",EDGE,"E23.sketch_text.stroke-5"),sQuery(id+"F20.wireOp",EDGE,"E23.sketch_text.stroke-6"),sQuery(id+"F20.wireOp",EDGE,"E23.sketch_text.stroke-7"),sQuery(id+"F20.wireOp",EDGE,"E23.sketch_text.stroke-8")])]});
            var Q10;
            Q10=makeQuery(id+"F21.opExtrude","SWEPT_BODY",BODY,{"disambiguationData":[OSD([sQuery(id+"F20.wireOp",EDGE,"E23.sketch_text.stroke-9"),sQuery(id+"F20.wireOp",EDGE,"E23.sketch_text.stroke-10"),sQuery(id+"F20.wireOp",EDGE,"E23.sketch_text.stroke-11"),sQuery(id+"F20.wireOp",EDGE,"E23.sketch_text.stroke-12"),sQuery(id+"F20.wireOp",EDGE,"E23.sketch_text.stroke-13"),sQuery(id+"F20.wireOp",EDGE,"E23.sketch_text.stroke-14"),sQuery(id+"F20.wireOp",EDGE,"E23.sketch_text.stroke-15"),sQuery(id+"F20.wireOp",EDGE,"E23.sketch_text.stroke-16"),sQuery(id+"F20.wireOp",EDGE,"E23.sketch_text.stroke-17"),sQuery(id+"F20.wireOp",EDGE,"E23.sketch_text.stroke-18"),sQuery(id+"F20.wireOp",EDGE,"E23.sketch_text.stroke-19"),sQuery(id+"F20.wireOp",EDGE,"E23.sketch_text.stroke-20"),sQuery(id+"F20.wireOp",EDGE,"E23.sketch_text.stroke-21"),sQuery(id+"F20.wireOp",EDGE,"E23.sketch_text.stroke-22"),sQuery(id+"F20.wireOp",EDGE,"E23.sketch_text.stroke-23"),sQuery(id+"F20.wireOp",EDGE,"E23.sketch_text.stroke-24")])]});
            var Q11;
            Q11=makeQuery(id+"F25.opExtrude","SWEPT_BODY",BODY,{"disambiguationData":[OSD([sQuery(id+"F24.wireOp",EDGE,"E24.sketch_text.stroke-0"),sQuery(id+"F24.wireOp",EDGE,"E24.sketch_text.stroke-1"),sQuery(id+"F24.wireOp",EDGE,"E24.sketch_text.stroke-2"),sQuery(id+"F24.wireOp",EDGE,"E24.sketch_text.stroke-3"),sQuery(id+"F24.wireOp",EDGE,"E24.sketch_text.stroke-4"),sQuery(id+"F24.wireOp",EDGE,"E24.sketch_text.stroke-5"),sQuery(id+"F24.wireOp",EDGE,"E24.sketch_text.stroke-6"),sQuery(id+"F24.wireOp",EDGE,"E24.sketch_text.stroke-7"),sQuery(id+"F24.wireOp",EDGE,"E24.sketch_text.stroke-8")])]});
            var Q12;
            Q12=makeQuery(id+"F25.opExtrude","SWEPT_BODY",BODY,{"disambiguationData":[OSD([sQuery(id+"F24.wireOp",EDGE,"E25.sketch_text.stroke-0"),sQuery(id+"F24.wireOp",EDGE,"E25.sketch_text.stroke-1"),sQuery(id+"F24.wireOp",EDGE,"E25.sketch_text.stroke-2"),sQuery(id+"F24.wireOp",EDGE,"E25.sketch_text.stroke-3"),sQuery(id+"F24.wireOp",EDGE,"E25.sketch_text.stroke-4"),sQuery(id+"F24.wireOp",EDGE,"E25.sketch_text.stroke-5"),sQuery(id+"F24.wireOp",EDGE,"E25.sketch_text.stroke-6"),sQuery(id+"F24.wireOp",EDGE,"E25.sketch_text.stroke-7"),sQuery(id+"F24.wireOp",EDGE,"E25.sketch_text.stroke-8"),sQuery(id+"F24.wireOp",EDGE,"E25.sketch_text.stroke-9"),sQuery(id+"F24.wireOp",EDGE,"E25.sketch_text.stroke-10"),sQuery(id+"F24.wireOp",EDGE,"E25.sketch_text.stroke-11"),sQuery(id+"F24.wireOp",EDGE,"E25.sketch_text.stroke-12"),sQuery(id+"F24.wireOp",EDGE,"E25.sketch_text.stroke-13"),sQuery(id+"F24.wireOp",EDGE,"E25.sketch_text.stroke-14"),sQuery(id+"F24.wireOp",EDGE,"E25.sketch_text.stroke-15"),sQuery(id+"F24.wireOp",EDGE,"E25.sketch_text.stroke-16"),sQuery(id+"F24.wireOp",EDGE,"E25.sketch_text.stroke-17"),sQuery(id+"F24.wireOp",EDGE,"E25.sketch_text.stroke-18"),sQuery(id+"F24.wireOp",EDGE,"E25.sketch_text.stroke-19")])]});
            var Q13;
            Q13=makeQuery(id+"F25.opExtrude","SWEPT_BODY",BODY,{"disambiguationData":[OSD([sQuery(id+"F24.wireOp",EDGE,"E26.sketch_text.stroke-0"),sQuery(id+"F24.wireOp",EDGE,"E26.sketch_text.stroke-1"),sQuery(id+"F24.wireOp",EDGE,"E26.sketch_text.stroke-2"),sQuery(id+"F24.wireOp",EDGE,"E26.sketch_text.stroke-3"),sQuery(id+"F24.wireOp",EDGE,"E26.sketch_text.stroke-4"),sQuery(id+"F24.wireOp",EDGE,"E26.sketch_text.stroke-5"),sQuery(id+"F24.wireOp",EDGE,"E26.sketch_text.stroke-6"),sQuery(id+"F24.wireOp",EDGE,"E26.sketch_text.stroke-7"),sQuery(id+"F24.wireOp",EDGE,"E26.sketch_text.stroke-8"),sQuery(id+"F24.wireOp",EDGE,"E26.sketch_text.stroke-9"),sQuery(id+"F24.wireOp",EDGE,"E26.sketch_text.stroke-10"),sQuery(id+"F24.wireOp",EDGE,"E26.sketch_text.stroke-11"),sQuery(id+"F24.wireOp",EDGE,"E26.sketch_text.stroke-12"),sQuery(id+"F24.wireOp",EDGE,"E26.sketch_text.stroke-13"),sQuery(id+"F24.wireOp",EDGE,"E26.sketch_text.stroke-14"),sQuery(id+"F24.wireOp",EDGE,"E26.sketch_text.stroke-15"),sQuery(id+"F24.wireOp",EDGE,"E26.sketch_text.stroke-16"),sQuery(id+"F24.wireOp",EDGE,"E26.sketch_text.stroke-17"),sQuery(id+"F24.wireOp",EDGE,"E26.sketch_text.stroke-18"),sQuery(id+"F24.wireOp",EDGE,"E26.sketch_text.stroke-19"),sQuery(id+"F24.wireOp",EDGE,"E26.sketch_text.stroke-20"),sQuery(id+"F24.wireOp",EDGE,"E26.sketch_text.stroke-21"),sQuery(id+"F24.wireOp",EDGE,"E26.sketch_text.stroke-22"),sQuery(id+"F24.wireOp",EDGE,"E26.sketch_text.stroke-23"),sQuery(id+"F24.wireOp",EDGE,"E26.sketch_text.stroke-24"),sQuery(id+"F24.wireOp",EDGE,"E26.sketch_text.stroke-25"),sQuery(id+"F24.wireOp",EDGE,"E26.sketch_text.stroke-26"),sQuery(id+"F24.wireOp",EDGE,"E26.sketch_text.stroke-27")])]});
            var Q14;
            Q14=makeQuery(id+"F25.opExtrude","SWEPT_BODY",BODY,{"disambiguationData":[OSD([sQuery(id+"F24.wireOp",EDGE,"E30.sketch_text.stroke-0"),sQuery(id+"F24.wireOp",EDGE,"E30.sketch_text.stroke-1"),sQuery(id+"F24.wireOp",EDGE,"E30.sketch_text.stroke-2"),sQuery(id+"F24.wireOp",EDGE,"E30.sketch_text.stroke-3"),sQuery(id+"F24.wireOp",EDGE,"E30.sketch_text.stroke-4"),sQuery(id+"F24.wireOp",EDGE,"E30.sketch_text.stroke-5"),sQuery(id+"F24.wireOp",EDGE,"E30.sketch_text.stroke-6")])]});
            var Q15;
            Q15=makeQuery(id+"F25.opExtrude","SWEPT_BODY",BODY,{"disambiguationData":[OSD([sQuery(id+"F24.wireOp",EDGE,"E29.sketch_text.stroke-0"),sQuery(id+"F24.wireOp",EDGE,"E29.sketch_text.stroke-1"),sQuery(id+"F24.wireOp",EDGE,"E29.sketch_text.stroke-2"),sQuery(id+"F24.wireOp",EDGE,"E29.sketch_text.stroke-3"),sQuery(id+"F24.wireOp",EDGE,"E29.sketch_text.stroke-4"),sQuery(id+"F24.wireOp",EDGE,"E29.sketch_text.stroke-5"),sQuery(id+"F24.wireOp",EDGE,"E29.sketch_text.stroke-6"),sQuery(id+"F24.wireOp",EDGE,"E29.sketch_text.stroke-7"),sQuery(id+"F24.wireOp",EDGE,"E29.sketch_text.stroke-8"),sQuery(id+"F24.wireOp",EDGE,"E29.sketch_text.stroke-9"),sQuery(id+"F24.wireOp",EDGE,"E29.sketch_text.stroke-10"),sQuery(id+"F24.wireOp",EDGE,"E29.sketch_text.stroke-11"),sQuery(id+"F24.wireOp",EDGE,"E29.sketch_text.stroke-12"),sQuery(id+"F24.wireOp",EDGE,"E29.sketch_text.stroke-13"),sQuery(id+"F24.wireOp",EDGE,"E29.sketch_text.stroke-14"),sQuery(id+"F24.wireOp",EDGE,"E29.sketch_text.stroke-15"),sQuery(id+"F24.wireOp",EDGE,"E29.sketch_text.stroke-16"),sQuery(id+"F24.wireOp",EDGE,"E29.sketch_text.stroke-17"),sQuery(id+"F24.wireOp",EDGE,"E29.sketch_text.stroke-18"),sQuery(id+"F24.wireOp",EDGE,"E29.sketch_text.stroke-19"),sQuery(id+"F24.wireOp",EDGE,"E29.sketch_text.stroke-20"),sQuery(id+"F24.wireOp",EDGE,"E29.sketch_text.stroke-21"),sQuery(id+"F24.wireOp",EDGE,"E29.sketch_text.stroke-22"),sQuery(id+"F24.wireOp",EDGE,"E29.sketch_text.stroke-23"),sQuery(id+"F24.wireOp",EDGE,"E29.sketch_text.stroke-24")])]});
            var Q16;
            Q16=makeQuery(id+"F25.opExtrude","SWEPT_BODY",BODY,{"disambiguationData":[OSD([sQuery(id+"F24.wireOp",EDGE,"E28.sketch_text.stroke-0"),sQuery(id+"F24.wireOp",EDGE,"E28.sketch_text.stroke-1"),sQuery(id+"F24.wireOp",EDGE,"E28.sketch_text.stroke-2"),sQuery(id+"F24.wireOp",EDGE,"E28.sketch_text.stroke-3"),sQuery(id+"F24.wireOp",EDGE,"E28.sketch_text.stroke-4"),sQuery(id+"F24.wireOp",EDGE,"E28.sketch_text.stroke-5"),sQuery(id+"F24.wireOp",EDGE,"E28.sketch_text.stroke-6"),sQuery(id+"F24.wireOp",EDGE,"E28.sketch_text.stroke-7"),sQuery(id+"F24.wireOp",EDGE,"E28.sketch_text.stroke-8"),sQuery(id+"F24.wireOp",EDGE,"E28.sketch_text.stroke-9"),sQuery(id+"F24.wireOp",EDGE,"E28.sketch_text.stroke-10"),sQuery(id+"F24.wireOp",EDGE,"E28.sketch_text.stroke-11"),sQuery(id+"F24.wireOp",EDGE,"E28.sketch_text.stroke-12"),sQuery(id+"F24.wireOp",EDGE,"E28.sketch_text.stroke-13"),sQuery(id+"F24.wireOp",EDGE,"E28.sketch_text.stroke-14"),sQuery(id+"F24.wireOp",EDGE,"E28.sketch_text.stroke-15"),sQuery(id+"F24.wireOp",EDGE,"E28.sketch_text.stroke-16"),sQuery(id+"F24.wireOp",EDGE,"E28.sketch_text.stroke-17"),sQuery(id+"F24.wireOp",EDGE,"E28.sketch_text.stroke-18")])]});
            var Q17;
            Q17=makeQuery(id+"F25.opExtrude","SWEPT_BODY",BODY,{"disambiguationData":[OSD([sQuery(id+"F24.wireOp",EDGE,"E27.sketch_text.stroke-0"),sQuery(id+"F24.wireOp",EDGE,"E27.sketch_text.stroke-1"),sQuery(id+"F24.wireOp",EDGE,"E27.sketch_text.stroke-2"),sQuery(id+"F24.wireOp",EDGE,"E27.sketch_text.stroke-3"),sQuery(id+"F24.wireOp",EDGE,"E27.sketch_text.stroke-4"),sQuery(id+"F24.wireOp",EDGE,"E27.sketch_text.stroke-5"),sQuery(id+"F24.wireOp",EDGE,"E27.sketch_text.stroke-6"),sQuery(id+"F24.wireOp",EDGE,"E27.sketch_text.stroke-7"),sQuery(id+"F24.wireOp",EDGE,"E27.sketch_text.stroke-8"),sQuery(id+"F24.wireOp",EDGE,"E27.sketch_text.stroke-9"),sQuery(id+"F24.wireOp",EDGE,"E27.sketch_text.stroke-10"),sQuery(id+"F24.wireOp",EDGE,"E27.sketch_text.stroke-11"),sQuery(id+"F24.wireOp",EDGE,"E27.sketch_text.stroke-12"),sQuery(id+"F24.wireOp",EDGE,"E27.sketch_text.stroke-13"),sQuery(id+"F24.wireOp",EDGE,"E27.sketch_text.stroke-14"),sQuery(id+"F24.wireOp",EDGE,"E27.sketch_text.stroke-15"),sQuery(id+"F24.wireOp",EDGE,"E27.sketch_text.stroke-16")])]});
            var Q18;
            Q18=makeQuery(id+"F25.opExtrude","SWEPT_BODY",BODY,{"disambiguationData":[OSD([sQuery(id+"F24.wireOp",EDGE,"E31.sketch_text.stroke-0"),sQuery(id+"F24.wireOp",EDGE,"E31.sketch_text.stroke-1"),sQuery(id+"F24.wireOp",EDGE,"E31.sketch_text.stroke-2"),sQuery(id+"F24.wireOp",EDGE,"E31.sketch_text.stroke-3"),sQuery(id+"F24.wireOp",EDGE,"E31.sketch_text.stroke-4"),sQuery(id+"F24.wireOp",EDGE,"E31.sketch_text.stroke-5"),sQuery(id+"F24.wireOp",EDGE,"E31.sketch_text.stroke-6"),sQuery(id+"F24.wireOp",EDGE,"E31.sketch_text.stroke-7"),sQuery(id+"F24.wireOp",EDGE,"E31.sketch_text.stroke-8"),sQuery(id+"F24.wireOp",EDGE,"E31.sketch_text.stroke-9"),sQuery(id+"F24.wireOp",EDGE,"E31.sketch_text.stroke-10"),sQuery(id+"F24.wireOp",EDGE,"E31.sketch_text.stroke-11"),sQuery(id+"F24.wireOp",EDGE,"E31.sketch_text.stroke-12"),sQuery(id+"F24.wireOp",EDGE,"E31.sketch_text.stroke-13"),sQuery(id+"F24.wireOp",EDGE,"E31.sketch_text.stroke-14"),sQuery(id+"F24.wireOp",EDGE,"E31.sketch_text.stroke-15"),sQuery(id+"F24.wireOp",EDGE,"E31.sketch_text.stroke-16"),sQuery(id+"F24.wireOp",EDGE,"E31.sketch_text.stroke-17"),sQuery(id+"F24.wireOp",EDGE,"E31.sketch_text.stroke-18"),sQuery(id+"F24.wireOp",EDGE,"E31.sketch_text.stroke-19"),sQuery(id+"F24.wireOp",EDGE,"E31.sketch_text.stroke-20"),sQuery(id+"F24.wireOp",EDGE,"E31.sketch_text.stroke-21"),sQuery(id+"F24.wireOp",EDGE,"E31.sketch_text.stroke-22"),sQuery(id+"F24.wireOp",EDGE,"E31.sketch_text.stroke-23"),sQuery(id+"F24.wireOp",EDGE,"E31.sketch_text.stroke-24"),sQuery(id+"F24.wireOp",EDGE,"E31.sketch_text.stroke-25"),sQuery(id+"F24.wireOp",EDGE,"E31.sketch_text.stroke-26"),sQuery(id+"F24.wireOp",EDGE,"E31.sketch_text.stroke-27"),sQuery(id+"F24.wireOp",EDGE,"E31.sketch_text.stroke-28"),sQuery(id+"F24.wireOp",EDGE,"E31.sketch_text.stroke-29"),sQuery(id+"F24.wireOp",EDGE,"E31.sketch_text.stroke-30")])]});
            var Q19;
            Q19=makeQuery(id+"F25.opExtrude","SWEPT_BODY",BODY,{"disambiguationData":[OSD([sQuery(id+"F24.wireOp",EDGE,"E32.sketch_text.stroke-0"),sQuery(id+"F24.wireOp",EDGE,"E32.sketch_text.stroke-1"),sQuery(id+"F24.wireOp",EDGE,"E32.sketch_text.stroke-2"),sQuery(id+"F24.wireOp",EDGE,"E32.sketch_text.stroke-3"),sQuery(id+"F24.wireOp",EDGE,"E32.sketch_text.stroke-4"),sQuery(id+"F24.wireOp",EDGE,"E32.sketch_text.stroke-5"),sQuery(id+"F24.wireOp",EDGE,"E32.sketch_text.stroke-6"),sQuery(id+"F24.wireOp",EDGE,"E32.sketch_text.stroke-7"),sQuery(id+"F24.wireOp",EDGE,"E32.sketch_text.stroke-8"),sQuery(id+"F24.wireOp",EDGE,"E32.sketch_text.stroke-9"),sQuery(id+"F24.wireOp",EDGE,"E32.sketch_text.stroke-10"),sQuery(id+"F24.wireOp",EDGE,"E32.sketch_text.stroke-11"),sQuery(id+"F24.wireOp",EDGE,"E32.sketch_text.stroke-12"),sQuery(id+"F24.wireOp",EDGE,"E32.sketch_text.stroke-13"),sQuery(id+"F24.wireOp",EDGE,"E32.sketch_text.stroke-14"),sQuery(id+"F24.wireOp",EDGE,"E32.sketch_text.stroke-15"),sQuery(id+"F24.wireOp",EDGE,"E32.sketch_text.stroke-16"),sQuery(id+"F24.wireOp",EDGE,"E32.sketch_text.stroke-17"),sQuery(id+"F24.wireOp",EDGE,"E32.sketch_text.stroke-18"),sQuery(id+"F24.wireOp",EDGE,"E32.sketch_text.stroke-19"),sQuery(id+"F24.wireOp",EDGE,"E32.sketch_text.stroke-20"),sQuery(id+"F24.wireOp",EDGE,"E32.sketch_text.stroke-21"),sQuery(id+"F24.wireOp",EDGE,"E32.sketch_text.stroke-22"),sQuery(id+"F24.wireOp",EDGE,"E32.sketch_text.stroke-23"),sQuery(id+"F24.wireOp",EDGE,"E32.sketch_text.stroke-24"),sQuery(id+"F24.wireOp",EDGE,"E32.sketch_text.stroke-25")])]});
            var Q20;
            Q20=makeQuery(id+"F25.opExtrude","SWEPT_BODY",BODY,{"disambiguationData":[OSD([sQuery(id+"F24.wireOp",EDGE,"E33.sketch_text.stroke-0"),sQuery(id+"F24.wireOp",EDGE,"E33.sketch_text.stroke-1"),sQuery(id+"F24.wireOp",EDGE,"E33.sketch_text.stroke-2"),sQuery(id+"F24.wireOp",EDGE,"E33.sketch_text.stroke-3"),sQuery(id+"F24.wireOp",EDGE,"E33.sketch_text.stroke-4"),sQuery(id+"F24.wireOp",EDGE,"E33.sketch_text.stroke-5"),sQuery(id+"F24.wireOp",EDGE,"E33.sketch_text.stroke-6"),sQuery(id+"F24.wireOp",EDGE,"E33.sketch_text.stroke-7"),sQuery(id+"F24.wireOp",EDGE,"E33.sketch_text.stroke-8")])]});
            var Q21;
            Q21=makeQuery(id+"F25.opExtrude","SWEPT_BODY",BODY,{"disambiguationData":[OSD([sQuery(id+"F24.wireOp",EDGE,"E33.sketch_text.stroke-9"),sQuery(id+"F24.wireOp",EDGE,"E33.sketch_text.stroke-10"),sQuery(id+"F24.wireOp",EDGE,"E33.sketch_text.stroke-11"),sQuery(id+"F24.wireOp",EDGE,"E33.sketch_text.stroke-12"),sQuery(id+"F24.wireOp",EDGE,"E33.sketch_text.stroke-13"),sQuery(id+"F24.wireOp",EDGE,"E33.sketch_text.stroke-14"),sQuery(id+"F24.wireOp",EDGE,"E33.sketch_text.stroke-15"),sQuery(id+"F24.wireOp",EDGE,"E33.sketch_text.stroke-16"),sQuery(id+"F24.wireOp",EDGE,"E33.sketch_text.stroke-17"),sQuery(id+"F24.wireOp",EDGE,"E33.sketch_text.stroke-18"),sQuery(id+"F24.wireOp",EDGE,"E33.sketch_text.stroke-19"),sQuery(id+"F24.wireOp",EDGE,"E33.sketch_text.stroke-20"),sQuery(id+"F24.wireOp",EDGE,"E33.sketch_text.stroke-21"),sQuery(id+"F24.wireOp",EDGE,"E33.sketch_text.stroke-22"),sQuery(id+"F24.wireOp",EDGE,"E33.sketch_text.stroke-23"),sQuery(id+"F24.wireOp",EDGE,"E33.sketch_text.stroke-24")])]});
            var Q22;
            Q22=makeQuery(id+"F25.opExtrude","SWEPT_BODY",BODY,{"disambiguationData":[OSD([sQuery(id+"F24.wireOp",EDGE,"E34.bottom"),sQuery(id+"F24.wireOp",EDGE,"E34.top"),sQuery(id+"F24.wireOp",EDGE,"E34.left"),sQuery(id+"F24.wireOp",EDGE,"E34.right")])]});
            var Q23;
            Q23=makeQuery(id+"F25.opExtrude","SWEPT_BODY",BODY,{"disambiguationData":[OSD([sQuery(id+"F24.wireOp",EDGE,"E36.1.0.0"),sQuery(id+"F24.wireOp",EDGE,"E36.1.0.1"),sQuery(id+"F24.wireOp",EDGE,"E36.1.0.2"),sQuery(id+"F24.wireOp",EDGE,"E36.1.0.3")])]});
            var Q24;
            Q24=makeQuery(id+"F25.opExtrude","SWEPT_BODY",BODY,{"disambiguationData":[OSD([sQuery(id+"F24.wireOp",EDGE,"E36.2.0.0"),sQuery(id+"F24.wireOp",EDGE,"E36.2.0.1"),sQuery(id+"F24.wireOp",EDGE,"E36.2.0.2"),sQuery(id+"F24.wireOp",EDGE,"E36.2.0.3")])]});
            var Q25;
            Q25=makeQuery(id+"F25.opExtrude","SWEPT_BODY",BODY,{"disambiguationData":[OSD([sQuery(id+"F24.wireOp",EDGE,"E36.3.0.0"),sQuery(id+"F24.wireOp",EDGE,"E36.3.0.1"),sQuery(id+"F24.wireOp",EDGE,"E36.3.0.2"),sQuery(id+"F24.wireOp",EDGE,"E36.3.0.3")])]});
            var Q26;
            Q26=makeQuery(id+"F25.opExtrude","SWEPT_BODY",BODY,{"disambiguationData":[OSD([sQuery(id+"F24.wireOp",EDGE,"E36.4.0.0"),sQuery(id+"F24.wireOp",EDGE,"E36.4.0.1"),sQuery(id+"F24.wireOp",EDGE,"E36.4.0.2"),sQuery(id+"F24.wireOp",EDGE,"E36.4.0.3")])]});
            var Q27;
            Q27=makeQuery(id+"F25.opExtrude","SWEPT_BODY",BODY,{"disambiguationData":[OSD([sQuery(id+"F24.wireOp",EDGE,"E36.5.0.0"),sQuery(id+"F24.wireOp",EDGE,"E36.5.0.1"),sQuery(id+"F24.wireOp",EDGE,"E36.5.0.2"),sQuery(id+"F24.wireOp",EDGE,"E36.5.0.3")])]});
            var Q28;
            Q28=makeQuery(id+"F25.opExtrude","SWEPT_BODY",BODY,{"disambiguationData":[OSD([sQuery(id+"F24.wireOp",EDGE,"E36.6.0.0"),sQuery(id+"F24.wireOp",EDGE,"E36.6.0.1"),sQuery(id+"F24.wireOp",EDGE,"E36.6.0.2"),sQuery(id+"F24.wireOp",EDGE,"E36.6.0.3")])]});
            var Q29;
            Q29=makeQuery(id+"F25.opExtrude","SWEPT_BODY",BODY,{"disambiguationData":[OSD([sQuery(id+"F24.wireOp",EDGE,"E36.7.0.0"),sQuery(id+"F24.wireOp",EDGE,"E36.7.0.1"),sQuery(id+"F24.wireOp",EDGE,"E36.7.0.2"),sQuery(id+"F24.wireOp",EDGE,"E36.7.0.3")])]});
            var Q30;
            Q30=makeQuery(id+"F25.opExtrude","SWEPT_BODY",BODY,{"disambiguationData":[OSD([sQuery(id+"F24.wireOp",EDGE,"E36.8.0.0"),sQuery(id+"F24.wireOp",EDGE,"E36.8.0.1"),sQuery(id+"F24.wireOp",EDGE,"E36.8.0.2"),sQuery(id+"F24.wireOp",EDGE,"E36.8.0.3")])]});
            var Q31;
            Q31=makeQuery(id+"F25.opExtrude","SWEPT_BODY",BODY,{"disambiguationData":[OSD([sQuery(id+"F24.wireOp",EDGE,"E36.9.0.0"),sQuery(id+"F24.wireOp",EDGE,"E36.9.0.1"),sQuery(id+"F24.wireOp",EDGE,"E36.9.0.2"),sQuery(id+"F24.wireOp",EDGE,"E36.9.0.3")])]});
            var Q32;
            Q32=sQuery(id+"F13.wireOp",EDGE,"E12");
            circularPattern(context, id + "F37", {"entities" : qUnion([Q0, Q1, Q2, Q3, Q4, Q5, Q6, Q7, Q8, Q9, Q10, Q11, Q12, Q13, Q14, Q15, Q16, Q17, Q18, Q19, Q20, Q21, Q22, Q23, Q24, Q25, Q26, Q27, Q28, Q29, Q30, Q31]), "axis" : qUnion([Q32]), "angle" : 360 * degree, "instanceCount" : 4, "equalSpace" : true});
        }
        {
            var Q0;
            Q0=makeQuery(id+"F27.opPattern","COPY",BODY,{"derivedFrom":makeQuery(id+"F25.opExtrude","SWEPT_BODY",BODY,{"disambiguationData":[OSD([sQuery(id+"F24.wireOp",EDGE,"E25.sketch_text.stroke-0"),sQuery(id+"F24.wireOp",EDGE,"E25.sketch_text.stroke-1"),sQuery(id+"F24.wireOp",EDGE,"E25.sketch_text.stroke-2"),sQuery(id+"F24.wireOp",EDGE,"E25.sketch_text.stroke-3"),sQuery(id+"F24.wireOp",EDGE,"E25.sketch_text.stroke-4"),sQuery(id+"F24.wireOp",EDGE,"E25.sketch_text.stroke-5"),sQuery(id+"F24.wireOp",EDGE,"E25.sketch_text.stroke-6"),sQuery(id+"F24.wireOp",EDGE,"E25.sketch_text.stroke-7"),sQuery(id+"F24.wireOp",EDGE,"E25.sketch_text.stroke-8"),sQuery(id+"F24.wireOp",EDGE,"E25.sketch_text.stroke-9"),sQuery(id+"F24.wireOp",EDGE,"E25.sketch_text.stroke-10"),sQuery(id+"F24.wireOp",EDGE,"E25.sketch_text.stroke-11"),sQuery(id+"F24.wireOp",EDGE,"E25.sketch_text.stroke-12"),sQuery(id+"F24.wireOp",EDGE,"E25.sketch_text.stroke-13"),sQuery(id+"F24.wireOp",EDGE,"E25.sketch_text.stroke-14"),sQuery(id+"F24.wireOp",EDGE,"E25.sketch_text.stroke-15"),sQuery(id+"F24.wireOp",EDGE,"E25.sketch_text.stroke-16"),sQuery(id+"F24.wireOp",EDGE,"E25.sketch_text.stroke-17"),sQuery(id+"F24.wireOp",EDGE,"E25.sketch_text.stroke-18"),sQuery(id+"F24.wireOp",EDGE,"E25.sketch_text.stroke-19")])]}),"instanceName":"1"});
            var Q1;
            Q1=makeQuery(id+"F27.opPattern","COPY",BODY,{"derivedFrom":makeQuery(id+"F25.opExtrude","SWEPT_BODY",BODY,{"disambiguationData":[OSD([sQuery(id+"F24.wireOp",EDGE,"E24.sketch_text.stroke-0"),sQuery(id+"F24.wireOp",EDGE,"E24.sketch_text.stroke-1"),sQuery(id+"F24.wireOp",EDGE,"E24.sketch_text.stroke-2"),sQuery(id+"F24.wireOp",EDGE,"E24.sketch_text.stroke-3"),sQuery(id+"F24.wireOp",EDGE,"E24.sketch_text.stroke-4"),sQuery(id+"F24.wireOp",EDGE,"E24.sketch_text.stroke-5"),sQuery(id+"F24.wireOp",EDGE,"E24.sketch_text.stroke-6"),sQuery(id+"F24.wireOp",EDGE,"E24.sketch_text.stroke-7"),sQuery(id+"F24.wireOp",EDGE,"E24.sketch_text.stroke-8")])]}),"instanceName":"1"});
            var Q2;
            Q2=makeQuery(id+"F27.opPattern","COPY",BODY,{"derivedFrom":makeQuery(id+"F25.opExtrude","SWEPT_BODY",BODY,{"disambiguationData":[OSD([sQuery(id+"F24.wireOp",EDGE,"E26.sketch_text.stroke-0"),sQuery(id+"F24.wireOp",EDGE,"E26.sketch_text.stroke-1"),sQuery(id+"F24.wireOp",EDGE,"E26.sketch_text.stroke-2"),sQuery(id+"F24.wireOp",EDGE,"E26.sketch_text.stroke-3"),sQuery(id+"F24.wireOp",EDGE,"E26.sketch_text.stroke-4"),sQuery(id+"F24.wireOp",EDGE,"E26.sketch_text.stroke-5"),sQuery(id+"F24.wireOp",EDGE,"E26.sketch_text.stroke-6"),sQuery(id+"F24.wireOp",EDGE,"E26.sketch_text.stroke-7"),sQuery(id+"F24.wireOp",EDGE,"E26.sketch_text.stroke-8"),sQuery(id+"F24.wireOp",EDGE,"E26.sketch_text.stroke-9"),sQuery(id+"F24.wireOp",EDGE,"E26.sketch_text.stroke-10"),sQuery(id+"F24.wireOp",EDGE,"E26.sketch_text.stroke-11"),sQuery(id+"F24.wireOp",EDGE,"E26.sketch_text.stroke-12"),sQuery(id+"F24.wireOp",EDGE,"E26.sketch_text.stroke-13"),sQuery(id+"F24.wireOp",EDGE,"E26.sketch_text.stroke-14"),sQuery(id+"F24.wireOp",EDGE,"E26.sketch_text.stroke-15"),sQuery(id+"F24.wireOp",EDGE,"E26.sketch_text.stroke-16"),sQuery(id+"F24.wireOp",EDGE,"E26.sketch_text.stroke-17"),sQuery(id+"F24.wireOp",EDGE,"E26.sketch_text.stroke-18"),sQuery(id+"F24.wireOp",EDGE,"E26.sketch_text.stroke-19"),sQuery(id+"F24.wireOp",EDGE,"E26.sketch_text.stroke-20"),sQuery(id+"F24.wireOp",EDGE,"E26.sketch_text.stroke-21"),sQuery(id+"F24.wireOp",EDGE,"E26.sketch_text.stroke-22"),sQuery(id+"F24.wireOp",EDGE,"E26.sketch_text.stroke-23"),sQuery(id+"F24.wireOp",EDGE,"E26.sketch_text.stroke-24"),sQuery(id+"F24.wireOp",EDGE,"E26.sketch_text.stroke-25"),sQuery(id+"F24.wireOp",EDGE,"E26.sketch_text.stroke-26"),sQuery(id+"F24.wireOp",EDGE,"E26.sketch_text.stroke-27")])]}),"instanceName":"1"});
            var Q3;
            Q3=makeQuery(id+"F27.opPattern","COPY",BODY,{"derivedFrom":makeQuery(id+"F25.opExtrude","SWEPT_BODY",BODY,{"disambiguationData":[OSD([sQuery(id+"F24.wireOp",EDGE,"E27.sketch_text.stroke-0"),sQuery(id+"F24.wireOp",EDGE,"E27.sketch_text.stroke-1"),sQuery(id+"F24.wireOp",EDGE,"E27.sketch_text.stroke-2"),sQuery(id+"F24.wireOp",EDGE,"E27.sketch_text.stroke-3"),sQuery(id+"F24.wireOp",EDGE,"E27.sketch_text.stroke-4"),sQuery(id+"F24.wireOp",EDGE,"E27.sketch_text.stroke-5"),sQuery(id+"F24.wireOp",EDGE,"E27.sketch_text.stroke-6"),sQuery(id+"F24.wireOp",EDGE,"E27.sketch_text.stroke-7"),sQuery(id+"F24.wireOp",EDGE,"E27.sketch_text.stroke-8"),sQuery(id+"F24.wireOp",EDGE,"E27.sketch_text.stroke-9"),sQuery(id+"F24.wireOp",EDGE,"E27.sketch_text.stroke-10"),sQuery(id+"F24.wireOp",EDGE,"E27.sketch_text.stroke-11"),sQuery(id+"F24.wireOp",EDGE,"E27.sketch_text.stroke-12"),sQuery(id+"F24.wireOp",EDGE,"E27.sketch_text.stroke-13"),sQuery(id+"F24.wireOp",EDGE,"E27.sketch_text.stroke-14"),sQuery(id+"F24.wireOp",EDGE,"E27.sketch_text.stroke-15"),sQuery(id+"F24.wireOp",EDGE,"E27.sketch_text.stroke-16")])]}),"instanceName":"1"});
            var Q4;
            Q4=makeQuery(id+"F27.opPattern","COPY",BODY,{"derivedFrom":makeQuery(id+"F25.opExtrude","SWEPT_BODY",BODY,{"disambiguationData":[OSD([sQuery(id+"F24.wireOp",EDGE,"E28.sketch_text.stroke-0"),sQuery(id+"F24.wireOp",EDGE,"E28.sketch_text.stroke-1"),sQuery(id+"F24.wireOp",EDGE,"E28.sketch_text.stroke-2"),sQuery(id+"F24.wireOp",EDGE,"E28.sketch_text.stroke-3"),sQuery(id+"F24.wireOp",EDGE,"E28.sketch_text.stroke-4"),sQuery(id+"F24.wireOp",EDGE,"E28.sketch_text.stroke-5"),sQuery(id+"F24.wireOp",EDGE,"E28.sketch_text.stroke-6"),sQuery(id+"F24.wireOp",EDGE,"E28.sketch_text.stroke-7"),sQuery(id+"F24.wireOp",EDGE,"E28.sketch_text.stroke-8"),sQuery(id+"F24.wireOp",EDGE,"E28.sketch_text.stroke-9"),sQuery(id+"F24.wireOp",EDGE,"E28.sketch_text.stroke-10"),sQuery(id+"F24.wireOp",EDGE,"E28.sketch_text.stroke-11"),sQuery(id+"F24.wireOp",EDGE,"E28.sketch_text.stroke-12"),sQuery(id+"F24.wireOp",EDGE,"E28.sketch_text.stroke-13"),sQuery(id+"F24.wireOp",EDGE,"E28.sketch_text.stroke-14"),sQuery(id+"F24.wireOp",EDGE,"E28.sketch_text.stroke-15"),sQuery(id+"F24.wireOp",EDGE,"E28.sketch_text.stroke-16"),sQuery(id+"F24.wireOp",EDGE,"E28.sketch_text.stroke-17"),sQuery(id+"F24.wireOp",EDGE,"E28.sketch_text.stroke-18")])]}),"instanceName":"1"});
            var Q5;
            Q5=makeQuery(id+"F27.opPattern","COPY",BODY,{"derivedFrom":makeQuery(id+"F25.opExtrude","SWEPT_BODY",BODY,{"disambiguationData":[OSD([sQuery(id+"F24.wireOp",EDGE,"E29.sketch_text.stroke-0"),sQuery(id+"F24.wireOp",EDGE,"E29.sketch_text.stroke-1"),sQuery(id+"F24.wireOp",EDGE,"E29.sketch_text.stroke-2"),sQuery(id+"F24.wireOp",EDGE,"E29.sketch_text.stroke-3"),sQuery(id+"F24.wireOp",EDGE,"E29.sketch_text.stroke-4"),sQuery(id+"F24.wireOp",EDGE,"E29.sketch_text.stroke-5"),sQuery(id+"F24.wireOp",EDGE,"E29.sketch_text.stroke-6"),sQuery(id+"F24.wireOp",EDGE,"E29.sketch_text.stroke-7"),sQuery(id+"F24.wireOp",EDGE,"E29.sketch_text.stroke-8"),sQuery(id+"F24.wireOp",EDGE,"E29.sketch_text.stroke-9"),sQuery(id+"F24.wireOp",EDGE,"E29.sketch_text.stroke-10"),sQuery(id+"F24.wireOp",EDGE,"E29.sketch_text.stroke-11"),sQuery(id+"F24.wireOp",EDGE,"E29.sketch_text.stroke-12"),sQuery(id+"F24.wireOp",EDGE,"E29.sketch_text.stroke-13"),sQuery(id+"F24.wireOp",EDGE,"E29.sketch_text.stroke-14"),sQuery(id+"F24.wireOp",EDGE,"E29.sketch_text.stroke-15"),sQuery(id+"F24.wireOp",EDGE,"E29.sketch_text.stroke-16"),sQuery(id+"F24.wireOp",EDGE,"E29.sketch_text.stroke-17"),sQuery(id+"F24.wireOp",EDGE,"E29.sketch_text.stroke-18"),sQuery(id+"F24.wireOp",EDGE,"E29.sketch_text.stroke-19"),sQuery(id+"F24.wireOp",EDGE,"E29.sketch_text.stroke-20"),sQuery(id+"F24.wireOp",EDGE,"E29.sketch_text.stroke-21"),sQuery(id+"F24.wireOp",EDGE,"E29.sketch_text.stroke-22"),sQuery(id+"F24.wireOp",EDGE,"E29.sketch_text.stroke-23"),sQuery(id+"F24.wireOp",EDGE,"E29.sketch_text.stroke-24")])]}),"instanceName":"1"});
            var Q6;
            Q6=makeQuery(id+"F27.opPattern","COPY",BODY,{"derivedFrom":makeQuery(id+"F25.opExtrude","SWEPT_BODY",BODY,{"disambiguationData":[OSD([sQuery(id+"F24.wireOp",EDGE,"E30.sketch_text.stroke-0"),sQuery(id+"F24.wireOp",EDGE,"E30.sketch_text.stroke-1"),sQuery(id+"F24.wireOp",EDGE,"E30.sketch_text.stroke-2"),sQuery(id+"F24.wireOp",EDGE,"E30.sketch_text.stroke-3"),sQuery(id+"F24.wireOp",EDGE,"E30.sketch_text.stroke-4"),sQuery(id+"F24.wireOp",EDGE,"E30.sketch_text.stroke-5"),sQuery(id+"F24.wireOp",EDGE,"E30.sketch_text.stroke-6")])]}),"instanceName":"1"});
            var Q7;
            Q7=makeQuery(id+"F27.opPattern","COPY",BODY,{"derivedFrom":makeQuery(id+"F25.opExtrude","SWEPT_BODY",BODY,{"disambiguationData":[OSD([sQuery(id+"F24.wireOp",EDGE,"E31.sketch_text.stroke-0"),sQuery(id+"F24.wireOp",EDGE,"E31.sketch_text.stroke-1"),sQuery(id+"F24.wireOp",EDGE,"E31.sketch_text.stroke-2"),sQuery(id+"F24.wireOp",EDGE,"E31.sketch_text.stroke-3"),sQuery(id+"F24.wireOp",EDGE,"E31.sketch_text.stroke-4"),sQuery(id+"F24.wireOp",EDGE,"E31.sketch_text.stroke-5"),sQuery(id+"F24.wireOp",EDGE,"E31.sketch_text.stroke-6"),sQuery(id+"F24.wireOp",EDGE,"E31.sketch_text.stroke-7"),sQuery(id+"F24.wireOp",EDGE,"E31.sketch_text.stroke-8"),sQuery(id+"F24.wireOp",EDGE,"E31.sketch_text.stroke-9"),sQuery(id+"F24.wireOp",EDGE,"E31.sketch_text.stroke-10"),sQuery(id+"F24.wireOp",EDGE,"E31.sketch_text.stroke-11"),sQuery(id+"F24.wireOp",EDGE,"E31.sketch_text.stroke-12"),sQuery(id+"F24.wireOp",EDGE,"E31.sketch_text.stroke-13"),sQuery(id+"F24.wireOp",EDGE,"E31.sketch_text.stroke-14"),sQuery(id+"F24.wireOp",EDGE,"E31.sketch_text.stroke-15"),sQuery(id+"F24.wireOp",EDGE,"E31.sketch_text.stroke-16"),sQuery(id+"F24.wireOp",EDGE,"E31.sketch_text.stroke-17"),sQuery(id+"F24.wireOp",EDGE,"E31.sketch_text.stroke-18"),sQuery(id+"F24.wireOp",EDGE,"E31.sketch_text.stroke-19"),sQuery(id+"F24.wireOp",EDGE,"E31.sketch_text.stroke-20"),sQuery(id+"F24.wireOp",EDGE,"E31.sketch_text.stroke-21"),sQuery(id+"F24.wireOp",EDGE,"E31.sketch_text.stroke-22"),sQuery(id+"F24.wireOp",EDGE,"E31.sketch_text.stroke-23"),sQuery(id+"F24.wireOp",EDGE,"E31.sketch_text.stroke-24"),sQuery(id+"F24.wireOp",EDGE,"E31.sketch_text.stroke-25"),sQuery(id+"F24.wireOp",EDGE,"E31.sketch_text.stroke-26"),sQuery(id+"F24.wireOp",EDGE,"E31.sketch_text.stroke-27"),sQuery(id+"F24.wireOp",EDGE,"E31.sketch_text.stroke-28"),sQuery(id+"F24.wireOp",EDGE,"E31.sketch_text.stroke-29"),sQuery(id+"F24.wireOp",EDGE,"E31.sketch_text.stroke-30")])]}),"instanceName":"1"});
            var Q8;
            Q8=makeQuery(id+"F27.opPattern","COPY",BODY,{"derivedFrom":makeQuery(id+"F25.opExtrude","SWEPT_BODY",BODY,{"disambiguationData":[OSD([sQuery(id+"F24.wireOp",EDGE,"E32.sketch_text.stroke-0"),sQuery(id+"F24.wireOp",EDGE,"E32.sketch_text.stroke-1"),sQuery(id+"F24.wireOp",EDGE,"E32.sketch_text.stroke-2"),sQuery(id+"F24.wireOp",EDGE,"E32.sketch_text.stroke-3"),sQuery(id+"F24.wireOp",EDGE,"E32.sketch_text.stroke-4"),sQuery(id+"F24.wireOp",EDGE,"E32.sketch_text.stroke-5"),sQuery(id+"F24.wireOp",EDGE,"E32.sketch_text.stroke-6"),sQuery(id+"F24.wireOp",EDGE,"E32.sketch_text.stroke-7"),sQuery(id+"F24.wireOp",EDGE,"E32.sketch_text.stroke-8"),sQuery(id+"F24.wireOp",EDGE,"E32.sketch_text.stroke-9"),sQuery(id+"F24.wireOp",EDGE,"E32.sketch_text.stroke-10"),sQuery(id+"F24.wireOp",EDGE,"E32.sketch_text.stroke-11"),sQuery(id+"F24.wireOp",EDGE,"E32.sketch_text.stroke-12"),sQuery(id+"F24.wireOp",EDGE,"E32.sketch_text.stroke-13"),sQuery(id+"F24.wireOp",EDGE,"E32.sketch_text.stroke-14"),sQuery(id+"F24.wireOp",EDGE,"E32.sketch_text.stroke-15"),sQuery(id+"F24.wireOp",EDGE,"E32.sketch_text.stroke-16"),sQuery(id+"F24.wireOp",EDGE,"E32.sketch_text.stroke-17"),sQuery(id+"F24.wireOp",EDGE,"E32.sketch_text.stroke-18"),sQuery(id+"F24.wireOp",EDGE,"E32.sketch_text.stroke-19"),sQuery(id+"F24.wireOp",EDGE,"E32.sketch_text.stroke-20"),sQuery(id+"F24.wireOp",EDGE,"E32.sketch_text.stroke-21"),sQuery(id+"F24.wireOp",EDGE,"E32.sketch_text.stroke-22"),sQuery(id+"F24.wireOp",EDGE,"E32.sketch_text.stroke-23"),sQuery(id+"F24.wireOp",EDGE,"E32.sketch_text.stroke-24"),sQuery(id+"F24.wireOp",EDGE,"E32.sketch_text.stroke-25")])]}),"instanceName":"1"});
            var Q9;
            Q9=makeQuery(id+"F27.opPattern","COPY",BODY,{"derivedFrom":makeQuery(id+"F25.opExtrude","SWEPT_BODY",BODY,{"disambiguationData":[OSD([sQuery(id+"F24.wireOp",EDGE,"E33.sketch_text.stroke-0"),sQuery(id+"F24.wireOp",EDGE,"E33.sketch_text.stroke-1"),sQuery(id+"F24.wireOp",EDGE,"E33.sketch_text.stroke-2"),sQuery(id+"F24.wireOp",EDGE,"E33.sketch_text.stroke-3"),sQuery(id+"F24.wireOp",EDGE,"E33.sketch_text.stroke-4"),sQuery(id+"F24.wireOp",EDGE,"E33.sketch_text.stroke-5"),sQuery(id+"F24.wireOp",EDGE,"E33.sketch_text.stroke-6"),sQuery(id+"F24.wireOp",EDGE,"E33.sketch_text.stroke-7"),sQuery(id+"F24.wireOp",EDGE,"E33.sketch_text.stroke-8")])]}),"instanceName":"1"});
            var Q10;
            Q10=makeQuery(id+"F27.opPattern","COPY",BODY,{"derivedFrom":makeQuery(id+"F25.opExtrude","SWEPT_BODY",BODY,{"disambiguationData":[OSD([sQuery(id+"F24.wireOp",EDGE,"E33.sketch_text.stroke-9"),sQuery(id+"F24.wireOp",EDGE,"E33.sketch_text.stroke-10"),sQuery(id+"F24.wireOp",EDGE,"E33.sketch_text.stroke-11"),sQuery(id+"F24.wireOp",EDGE,"E33.sketch_text.stroke-12"),sQuery(id+"F24.wireOp",EDGE,"E33.sketch_text.stroke-13"),sQuery(id+"F24.wireOp",EDGE,"E33.sketch_text.stroke-14"),sQuery(id+"F24.wireOp",EDGE,"E33.sketch_text.stroke-15"),sQuery(id+"F24.wireOp",EDGE,"E33.sketch_text.stroke-16"),sQuery(id+"F24.wireOp",EDGE,"E33.sketch_text.stroke-17"),sQuery(id+"F24.wireOp",EDGE,"E33.sketch_text.stroke-18"),sQuery(id+"F24.wireOp",EDGE,"E33.sketch_text.stroke-19"),sQuery(id+"F24.wireOp",EDGE,"E33.sketch_text.stroke-20"),sQuery(id+"F24.wireOp",EDGE,"E33.sketch_text.stroke-21"),sQuery(id+"F24.wireOp",EDGE,"E33.sketch_text.stroke-22"),sQuery(id+"F24.wireOp",EDGE,"E33.sketch_text.stroke-23"),sQuery(id+"F24.wireOp",EDGE,"E33.sketch_text.stroke-24")])]}),"instanceName":"1"});
            var Q11;
            Q11=makeQuery(id+"F27.opPattern","COPY",BODY,{"derivedFrom":makeQuery(id+"F25.opExtrude","SWEPT_BODY",BODY,{"disambiguationData":[OSD([sQuery(id+"F24.wireOp",EDGE,"E34.bottom"),sQuery(id+"F24.wireOp",EDGE,"E34.top"),sQuery(id+"F24.wireOp",EDGE,"E34.left"),sQuery(id+"F24.wireOp",EDGE,"E34.right")])]}),"instanceName":"1"});
            var Q12;
            Q12=makeQuery(id+"F27.opPattern","COPY",BODY,{"derivedFrom":makeQuery(id+"F25.opExtrude","SWEPT_BODY",BODY,{"disambiguationData":[OSD([sQuery(id+"F24.wireOp",EDGE,"E36.1.0.0"),sQuery(id+"F24.wireOp",EDGE,"E36.1.0.1"),sQuery(id+"F24.wireOp",EDGE,"E36.1.0.2"),sQuery(id+"F24.wireOp",EDGE,"E36.1.0.3")])]}),"instanceName":"1"});
            var Q13;
            Q13=makeQuery(id+"F27.opPattern","COPY",BODY,{"derivedFrom":makeQuery(id+"F25.opExtrude","SWEPT_BODY",BODY,{"disambiguationData":[OSD([sQuery(id+"F24.wireOp",EDGE,"E36.2.0.0"),sQuery(id+"F24.wireOp",EDGE,"E36.2.0.1"),sQuery(id+"F24.wireOp",EDGE,"E36.2.0.2"),sQuery(id+"F24.wireOp",EDGE,"E36.2.0.3")])]}),"instanceName":"1"});
            var Q14;
            Q14=makeQuery(id+"F27.opPattern","COPY",BODY,{"derivedFrom":makeQuery(id+"F25.opExtrude","SWEPT_BODY",BODY,{"disambiguationData":[OSD([sQuery(id+"F24.wireOp",EDGE,"E36.3.0.0"),sQuery(id+"F24.wireOp",EDGE,"E36.3.0.1"),sQuery(id+"F24.wireOp",EDGE,"E36.3.0.2"),sQuery(id+"F24.wireOp",EDGE,"E36.3.0.3")])]}),"instanceName":"1"});
            var Q15;
            Q15=makeQuery(id+"F27.opPattern","COPY",BODY,{"derivedFrom":makeQuery(id+"F25.opExtrude","SWEPT_BODY",BODY,{"disambiguationData":[OSD([sQuery(id+"F24.wireOp",EDGE,"E36.4.0.0"),sQuery(id+"F24.wireOp",EDGE,"E36.4.0.1"),sQuery(id+"F24.wireOp",EDGE,"E36.4.0.2"),sQuery(id+"F24.wireOp",EDGE,"E36.4.0.3")])]}),"instanceName":"1"});
            var Q16;
            Q16=makeQuery(id+"F27.opPattern","COPY",BODY,{"derivedFrom":makeQuery(id+"F25.opExtrude","SWEPT_BODY",BODY,{"disambiguationData":[OSD([sQuery(id+"F24.wireOp",EDGE,"E36.5.0.0"),sQuery(id+"F24.wireOp",EDGE,"E36.5.0.1"),sQuery(id+"F24.wireOp",EDGE,"E36.5.0.2"),sQuery(id+"F24.wireOp",EDGE,"E36.5.0.3")])]}),"instanceName":"1"});
            var Q17;
            Q17=makeQuery(id+"F27.opPattern","COPY",BODY,{"derivedFrom":makeQuery(id+"F25.opExtrude","SWEPT_BODY",BODY,{"disambiguationData":[OSD([sQuery(id+"F24.wireOp",EDGE,"E36.6.0.0"),sQuery(id+"F24.wireOp",EDGE,"E36.6.0.1"),sQuery(id+"F24.wireOp",EDGE,"E36.6.0.2"),sQuery(id+"F24.wireOp",EDGE,"E36.6.0.3")])]}),"instanceName":"1"});
            var Q18;
            Q18=makeQuery(id+"F27.opPattern","COPY",BODY,{"derivedFrom":makeQuery(id+"F25.opExtrude","SWEPT_BODY",BODY,{"disambiguationData":[OSD([sQuery(id+"F24.wireOp",EDGE,"E36.7.0.0"),sQuery(id+"F24.wireOp",EDGE,"E36.7.0.1"),sQuery(id+"F24.wireOp",EDGE,"E36.7.0.2"),sQuery(id+"F24.wireOp",EDGE,"E36.7.0.3")])]}),"instanceName":"1"});
            var Q19;
            Q19=makeQuery(id+"F27.opPattern","COPY",BODY,{"derivedFrom":makeQuery(id+"F25.opExtrude","SWEPT_BODY",BODY,{"disambiguationData":[OSD([sQuery(id+"F24.wireOp",EDGE,"E36.8.0.0"),sQuery(id+"F24.wireOp",EDGE,"E36.8.0.1"),sQuery(id+"F24.wireOp",EDGE,"E36.8.0.2"),sQuery(id+"F24.wireOp",EDGE,"E36.8.0.3")])]}),"instanceName":"1"});
            var Q20;
            Q20=makeQuery(id+"F27.opPattern","COPY",BODY,{"derivedFrom":makeQuery(id+"F25.opExtrude","SWEPT_BODY",BODY,{"disambiguationData":[OSD([sQuery(id+"F24.wireOp",EDGE,"E36.9.0.0"),sQuery(id+"F24.wireOp",EDGE,"E36.9.0.1"),sQuery(id+"F24.wireOp",EDGE,"E36.9.0.2"),sQuery(id+"F24.wireOp",EDGE,"E36.9.0.3")])]}),"instanceName":"1"});
            var Q21;
            Q21=makeQuery(id+"F23.opPattern","COPY",BODY,{"derivedFrom":makeQuery(id+"F21.opExtrude","SWEPT_BODY",BODY,{"disambiguationData":[OSD([sQuery(id+"F20.wireOp",EDGE,"E15.sketch_text.stroke-0"),sQuery(id+"F20.wireOp",EDGE,"E15.sketch_text.stroke-1"),sQuery(id+"F20.wireOp",EDGE,"E15.sketch_text.stroke-2"),sQuery(id+"F20.wireOp",EDGE,"E15.sketch_text.stroke-3"),sQuery(id+"F20.wireOp",EDGE,"E15.sketch_text.stroke-4"),sQuery(id+"F20.wireOp",EDGE,"E15.sketch_text.stroke-5"),sQuery(id+"F20.wireOp",EDGE,"E15.sketch_text.stroke-6"),sQuery(id+"F20.wireOp",EDGE,"E15.sketch_text.stroke-7"),sQuery(id+"F20.wireOp",EDGE,"E15.sketch_text.stroke-8"),sQuery(id+"F20.wireOp",EDGE,"E15.sketch_text.stroke-9"),sQuery(id+"F20.wireOp",EDGE,"E15.sketch_text.stroke-10"),sQuery(id+"F20.wireOp",EDGE,"E15.sketch_text.stroke-11"),sQuery(id+"F20.wireOp",EDGE,"E15.sketch_text.stroke-12"),sQuery(id+"F20.wireOp",EDGE,"E15.sketch_text.stroke-13"),sQuery(id+"F20.wireOp",EDGE,"E15.sketch_text.stroke-14"),sQuery(id+"F20.wireOp",EDGE,"E15.sketch_text.stroke-15"),sQuery(id+"F20.wireOp",EDGE,"E15.sketch_text.stroke-16"),sQuery(id+"F20.wireOp",EDGE,"E15.sketch_text.stroke-17"),sQuery(id+"F20.wireOp",EDGE,"E15.sketch_text.stroke-18"),sQuery(id+"F20.wireOp",EDGE,"E15.sketch_text.stroke-19")])]}),"instanceName":"1"});
            var Q22;
            Q22=makeQuery(id+"F23.opPattern","COPY",BODY,{"derivedFrom":makeQuery(id+"F21.opExtrude","SWEPT_BODY",BODY,{"disambiguationData":[OSD([sQuery(id+"F20.wireOp",EDGE,"E16.sketch_text.stroke-0"),sQuery(id+"F20.wireOp",EDGE,"E16.sketch_text.stroke-1"),sQuery(id+"F20.wireOp",EDGE,"E16.sketch_text.stroke-2"),sQuery(id+"F20.wireOp",EDGE,"E16.sketch_text.stroke-3"),sQuery(id+"F20.wireOp",EDGE,"E16.sketch_text.stroke-4"),sQuery(id+"F20.wireOp",EDGE,"E16.sketch_text.stroke-5"),sQuery(id+"F20.wireOp",EDGE,"E16.sketch_text.stroke-6"),sQuery(id+"F20.wireOp",EDGE,"E16.sketch_text.stroke-7"),sQuery(id+"F20.wireOp",EDGE,"E16.sketch_text.stroke-8"),sQuery(id+"F20.wireOp",EDGE,"E16.sketch_text.stroke-9"),sQuery(id+"F20.wireOp",EDGE,"E16.sketch_text.stroke-10"),sQuery(id+"F20.wireOp",EDGE,"E16.sketch_text.stroke-11"),sQuery(id+"F20.wireOp",EDGE,"E16.sketch_text.stroke-12"),sQuery(id+"F20.wireOp",EDGE,"E16.sketch_text.stroke-13"),sQuery(id+"F20.wireOp",EDGE,"E16.sketch_text.stroke-14"),sQuery(id+"F20.wireOp",EDGE,"E16.sketch_text.stroke-15"),sQuery(id+"F20.wireOp",EDGE,"E16.sketch_text.stroke-16"),sQuery(id+"F20.wireOp",EDGE,"E16.sketch_text.stroke-17"),sQuery(id+"F20.wireOp",EDGE,"E16.sketch_text.stroke-18"),sQuery(id+"F20.wireOp",EDGE,"E16.sketch_text.stroke-19"),sQuery(id+"F20.wireOp",EDGE,"E16.sketch_text.stroke-20"),sQuery(id+"F20.wireOp",EDGE,"E16.sketch_text.stroke-21"),sQuery(id+"F20.wireOp",EDGE,"E16.sketch_text.stroke-22"),sQuery(id+"F20.wireOp",EDGE,"E16.sketch_text.stroke-23"),sQuery(id+"F20.wireOp",EDGE,"E16.sketch_text.stroke-24"),sQuery(id+"F20.wireOp",EDGE,"E16.sketch_text.stroke-25"),sQuery(id+"F20.wireOp",EDGE,"E16.sketch_text.stroke-26"),sQuery(id+"F20.wireOp",EDGE,"E16.sketch_text.stroke-27")])]}),"instanceName":"1"});
            var Q23;
            Q23=makeQuery(id+"F23.opPattern","COPY",BODY,{"derivedFrom":makeQuery(id+"F21.opExtrude","SWEPT_BODY",BODY,{"disambiguationData":[OSD([sQuery(id+"F20.wireOp",EDGE,"E17.sketch_text.stroke-0"),sQuery(id+"F20.wireOp",EDGE,"E17.sketch_text.stroke-1"),sQuery(id+"F20.wireOp",EDGE,"E17.sketch_text.stroke-2"),sQuery(id+"F20.wireOp",EDGE,"E17.sketch_text.stroke-3"),sQuery(id+"F20.wireOp",EDGE,"E17.sketch_text.stroke-4"),sQuery(id+"F20.wireOp",EDGE,"E17.sketch_text.stroke-5"),sQuery(id+"F20.wireOp",EDGE,"E17.sketch_text.stroke-6"),sQuery(id+"F20.wireOp",EDGE,"E17.sketch_text.stroke-7"),sQuery(id+"F20.wireOp",EDGE,"E17.sketch_text.stroke-8"),sQuery(id+"F20.wireOp",EDGE,"E17.sketch_text.stroke-9"),sQuery(id+"F20.wireOp",EDGE,"E17.sketch_text.stroke-10"),sQuery(id+"F20.wireOp",EDGE,"E17.sketch_text.stroke-11"),sQuery(id+"F20.wireOp",EDGE,"E17.sketch_text.stroke-12"),sQuery(id+"F20.wireOp",EDGE,"E17.sketch_text.stroke-13"),sQuery(id+"F20.wireOp",EDGE,"E17.sketch_text.stroke-14"),sQuery(id+"F20.wireOp",EDGE,"E17.sketch_text.stroke-15"),sQuery(id+"F20.wireOp",EDGE,"E17.sketch_text.stroke-16")])]}),"instanceName":"1"});
            var Q24;
            Q24=makeQuery(id+"F23.opPattern","COPY",BODY,{"derivedFrom":makeQuery(id+"F21.opExtrude","SWEPT_BODY",BODY,{"disambiguationData":[OSD([sQuery(id+"F20.wireOp",EDGE,"E18.sketch_text.stroke-0"),sQuery(id+"F20.wireOp",EDGE,"E18.sketch_text.stroke-1"),sQuery(id+"F20.wireOp",EDGE,"E18.sketch_text.stroke-2"),sQuery(id+"F20.wireOp",EDGE,"E18.sketch_text.stroke-3"),sQuery(id+"F20.wireOp",EDGE,"E18.sketch_text.stroke-4"),sQuery(id+"F20.wireOp",EDGE,"E18.sketch_text.stroke-5"),sQuery(id+"F20.wireOp",EDGE,"E18.sketch_text.stroke-6"),sQuery(id+"F20.wireOp",EDGE,"E18.sketch_text.stroke-7"),sQuery(id+"F20.wireOp",EDGE,"E18.sketch_text.stroke-8"),sQuery(id+"F20.wireOp",EDGE,"E18.sketch_text.stroke-9"),sQuery(id+"F20.wireOp",EDGE,"E18.sketch_text.stroke-10"),sQuery(id+"F20.wireOp",EDGE,"E18.sketch_text.stroke-11"),sQuery(id+"F20.wireOp",EDGE,"E18.sketch_text.stroke-12"),sQuery(id+"F20.wireOp",EDGE,"E18.sketch_text.stroke-13"),sQuery(id+"F20.wireOp",EDGE,"E18.sketch_text.stroke-14"),sQuery(id+"F20.wireOp",EDGE,"E18.sketch_text.stroke-15"),sQuery(id+"F20.wireOp",EDGE,"E18.sketch_text.stroke-16"),sQuery(id+"F20.wireOp",EDGE,"E18.sketch_text.stroke-17"),sQuery(id+"F20.wireOp",EDGE,"E18.sketch_text.stroke-18")])]}),"instanceName":"1"});
            var Q25;
            Q25=makeQuery(id+"F23.opPattern","COPY",BODY,{"derivedFrom":makeQuery(id+"F21.opExtrude","SWEPT_BODY",BODY,{"disambiguationData":[OSD([sQuery(id+"F20.wireOp",EDGE,"E19.sketch_text.stroke-0"),sQuery(id+"F20.wireOp",EDGE,"E19.sketch_text.stroke-1"),sQuery(id+"F20.wireOp",EDGE,"E19.sketch_text.stroke-2"),sQuery(id+"F20.wireOp",EDGE,"E19.sketch_text.stroke-3"),sQuery(id+"F20.wireOp",EDGE,"E19.sketch_text.stroke-4"),sQuery(id+"F20.wireOp",EDGE,"E19.sketch_text.stroke-5"),sQuery(id+"F20.wireOp",EDGE,"E19.sketch_text.stroke-6"),sQuery(id+"F20.wireOp",EDGE,"E19.sketch_text.stroke-7"),sQuery(id+"F20.wireOp",EDGE,"E19.sketch_text.stroke-8"),sQuery(id+"F20.wireOp",EDGE,"E19.sketch_text.stroke-9"),sQuery(id+"F20.wireOp",EDGE,"E19.sketch_text.stroke-10"),sQuery(id+"F20.wireOp",EDGE,"E19.sketch_text.stroke-11"),sQuery(id+"F20.wireOp",EDGE,"E19.sketch_text.stroke-12"),sQuery(id+"F20.wireOp",EDGE,"E19.sketch_text.stroke-13"),sQuery(id+"F20.wireOp",EDGE,"E19.sketch_text.stroke-14"),sQuery(id+"F20.wireOp",EDGE,"E19.sketch_text.stroke-15"),sQuery(id+"F20.wireOp",EDGE,"E19.sketch_text.stroke-16"),sQuery(id+"F20.wireOp",EDGE,"E19.sketch_text.stroke-17"),sQuery(id+"F20.wireOp",EDGE,"E19.sketch_text.stroke-18"),sQuery(id+"F20.wireOp",EDGE,"E19.sketch_text.stroke-19"),sQuery(id+"F20.wireOp",EDGE,"E19.sketch_text.stroke-20"),sQuery(id+"F20.wireOp",EDGE,"E19.sketch_text.stroke-21"),sQuery(id+"F20.wireOp",EDGE,"E19.sketch_text.stroke-22"),sQuery(id+"F20.wireOp",EDGE,"E19.sketch_text.stroke-23"),sQuery(id+"F20.wireOp",EDGE,"E19.sketch_text.stroke-24")])]}),"instanceName":"1"});
            var Q26;
            Q26=makeQuery(id+"F23.opPattern","COPY",BODY,{"derivedFrom":makeQuery(id+"F21.opExtrude","SWEPT_BODY",BODY,{"disambiguationData":[OSD([sQuery(id+"F20.wireOp",EDGE,"E20.sketch_text.stroke-0"),sQuery(id+"F20.wireOp",EDGE,"E20.sketch_text.stroke-1"),sQuery(id+"F20.wireOp",EDGE,"E20.sketch_text.stroke-2"),sQuery(id+"F20.wireOp",EDGE,"E20.sketch_text.stroke-3"),sQuery(id+"F20.wireOp",EDGE,"E20.sketch_text.stroke-4"),sQuery(id+"F20.wireOp",EDGE,"E20.sketch_text.stroke-5"),sQuery(id+"F20.wireOp",EDGE,"E20.sketch_text.stroke-6")])]}),"instanceName":"1"});
            var Q27;
            Q27=makeQuery(id+"F23.opPattern","COPY",BODY,{"derivedFrom":makeQuery(id+"F21.opExtrude","SWEPT_BODY",BODY,{"disambiguationData":[OSD([sQuery(id+"F20.wireOp",EDGE,"E21.sketch_text.stroke-0"),sQuery(id+"F20.wireOp",EDGE,"E21.sketch_text.stroke-1"),sQuery(id+"F20.wireOp",EDGE,"E21.sketch_text.stroke-2"),sQuery(id+"F20.wireOp",EDGE,"E21.sketch_text.stroke-3"),sQuery(id+"F20.wireOp",EDGE,"E21.sketch_text.stroke-4"),sQuery(id+"F20.wireOp",EDGE,"E21.sketch_text.stroke-5"),sQuery(id+"F20.wireOp",EDGE,"E21.sketch_text.stroke-6"),sQuery(id+"F20.wireOp",EDGE,"E21.sketch_text.stroke-7"),sQuery(id+"F20.wireOp",EDGE,"E21.sketch_text.stroke-8"),sQuery(id+"F20.wireOp",EDGE,"E21.sketch_text.stroke-9"),sQuery(id+"F20.wireOp",EDGE,"E21.sketch_text.stroke-10"),sQuery(id+"F20.wireOp",EDGE,"E21.sketch_text.stroke-11"),sQuery(id+"F20.wireOp",EDGE,"E21.sketch_text.stroke-12"),sQuery(id+"F20.wireOp",EDGE,"E21.sketch_text.stroke-13"),sQuery(id+"F20.wireOp",EDGE,"E21.sketch_text.stroke-14"),sQuery(id+"F20.wireOp",EDGE,"E21.sketch_text.stroke-15"),sQuery(id+"F20.wireOp",EDGE,"E21.sketch_text.stroke-16"),sQuery(id+"F20.wireOp",EDGE,"E21.sketch_text.stroke-17"),sQuery(id+"F20.wireOp",EDGE,"E21.sketch_text.stroke-18"),sQuery(id+"F20.wireOp",EDGE,"E21.sketch_text.stroke-19"),sQuery(id+"F20.wireOp",EDGE,"E21.sketch_text.stroke-20"),sQuery(id+"F20.wireOp",EDGE,"E21.sketch_text.stroke-21"),sQuery(id+"F20.wireOp",EDGE,"E21.sketch_text.stroke-22"),sQuery(id+"F20.wireOp",EDGE,"E21.sketch_text.stroke-23"),sQuery(id+"F20.wireOp",EDGE,"E21.sketch_text.stroke-24"),sQuery(id+"F20.wireOp",EDGE,"E21.sketch_text.stroke-25"),sQuery(id+"F20.wireOp",EDGE,"E21.sketch_text.stroke-26"),sQuery(id+"F20.wireOp",EDGE,"E21.sketch_text.stroke-27"),sQuery(id+"F20.wireOp",EDGE,"E21.sketch_text.stroke-28"),sQuery(id+"F20.wireOp",EDGE,"E21.sketch_text.stroke-29"),sQuery(id+"F20.wireOp",EDGE,"E21.sketch_text.stroke-30")])]}),"instanceName":"1"});
            var Q28;
            Q28=makeQuery(id+"F23.opPattern","COPY",BODY,{"derivedFrom":makeQuery(id+"F21.opExtrude","SWEPT_BODY",BODY,{"disambiguationData":[OSD([sQuery(id+"F20.wireOp",EDGE,"E22.sketch_text.stroke-0"),sQuery(id+"F20.wireOp",EDGE,"E22.sketch_text.stroke-1"),sQuery(id+"F20.wireOp",EDGE,"E22.sketch_text.stroke-2"),sQuery(id+"F20.wireOp",EDGE,"E22.sketch_text.stroke-3"),sQuery(id+"F20.wireOp",EDGE,"E22.sketch_text.stroke-4"),sQuery(id+"F20.wireOp",EDGE,"E22.sketch_text.stroke-5"),sQuery(id+"F20.wireOp",EDGE,"E22.sketch_text.stroke-6"),sQuery(id+"F20.wireOp",EDGE,"E22.sketch_text.stroke-7"),sQuery(id+"F20.wireOp",EDGE,"E22.sketch_text.stroke-8"),sQuery(id+"F20.wireOp",EDGE,"E22.sketch_text.stroke-9"),sQuery(id+"F20.wireOp",EDGE,"E22.sketch_text.stroke-10"),sQuery(id+"F20.wireOp",EDGE,"E22.sketch_text.stroke-11"),sQuery(id+"F20.wireOp",EDGE,"E22.sketch_text.stroke-12"),sQuery(id+"F20.wireOp",EDGE,"E22.sketch_text.stroke-13"),sQuery(id+"F20.wireOp",EDGE,"E22.sketch_text.stroke-14"),sQuery(id+"F20.wireOp",EDGE,"E22.sketch_text.stroke-15"),sQuery(id+"F20.wireOp",EDGE,"E22.sketch_text.stroke-16"),sQuery(id+"F20.wireOp",EDGE,"E22.sketch_text.stroke-17"),sQuery(id+"F20.wireOp",EDGE,"E22.sketch_text.stroke-18"),sQuery(id+"F20.wireOp",EDGE,"E22.sketch_text.stroke-19"),sQuery(id+"F20.wireOp",EDGE,"E22.sketch_text.stroke-20"),sQuery(id+"F20.wireOp",EDGE,"E22.sketch_text.stroke-21"),sQuery(id+"F20.wireOp",EDGE,"E22.sketch_text.stroke-22"),sQuery(id+"F20.wireOp",EDGE,"E22.sketch_text.stroke-23"),sQuery(id+"F20.wireOp",EDGE,"E22.sketch_text.stroke-24"),sQuery(id+"F20.wireOp",EDGE,"E22.sketch_text.stroke-25")])]}),"instanceName":"1"});
            var Q29;
            Q29=makeQuery(id+"F23.opPattern","COPY",BODY,{"derivedFrom":makeQuery(id+"F21.opExtrude","SWEPT_BODY",BODY,{"disambiguationData":[OSD([sQuery(id+"F20.wireOp",EDGE,"E23.sketch_text.stroke-0"),sQuery(id+"F20.wireOp",EDGE,"E23.sketch_text.stroke-1"),sQuery(id+"F20.wireOp",EDGE,"E23.sketch_text.stroke-2"),sQuery(id+"F20.wireOp",EDGE,"E23.sketch_text.stroke-3"),sQuery(id+"F20.wireOp",EDGE,"E23.sketch_text.stroke-4"),sQuery(id+"F20.wireOp",EDGE,"E23.sketch_text.stroke-5"),sQuery(id+"F20.wireOp",EDGE,"E23.sketch_text.stroke-6"),sQuery(id+"F20.wireOp",EDGE,"E23.sketch_text.stroke-7"),sQuery(id+"F20.wireOp",EDGE,"E23.sketch_text.stroke-8")])]}),"instanceName":"1"});
            var Q30;
            Q30=makeQuery(id+"F23.opPattern","COPY",BODY,{"derivedFrom":makeQuery(id+"F21.opExtrude","SWEPT_BODY",BODY,{"disambiguationData":[OSD([sQuery(id+"F20.wireOp",EDGE,"E23.sketch_text.stroke-9"),sQuery(id+"F20.wireOp",EDGE,"E23.sketch_text.stroke-10"),sQuery(id+"F20.wireOp",EDGE,"E23.sketch_text.stroke-11"),sQuery(id+"F20.wireOp",EDGE,"E23.sketch_text.stroke-12"),sQuery(id+"F20.wireOp",EDGE,"E23.sketch_text.stroke-13"),sQuery(id+"F20.wireOp",EDGE,"E23.sketch_text.stroke-14"),sQuery(id+"F20.wireOp",EDGE,"E23.sketch_text.stroke-15"),sQuery(id+"F20.wireOp",EDGE,"E23.sketch_text.stroke-16"),sQuery(id+"F20.wireOp",EDGE,"E23.sketch_text.stroke-17"),sQuery(id+"F20.wireOp",EDGE,"E23.sketch_text.stroke-18"),sQuery(id+"F20.wireOp",EDGE,"E23.sketch_text.stroke-19"),sQuery(id+"F20.wireOp",EDGE,"E23.sketch_text.stroke-20"),sQuery(id+"F20.wireOp",EDGE,"E23.sketch_text.stroke-21"),sQuery(id+"F20.wireOp",EDGE,"E23.sketch_text.stroke-22"),sQuery(id+"F20.wireOp",EDGE,"E23.sketch_text.stroke-23"),sQuery(id+"F20.wireOp",EDGE,"E23.sketch_text.stroke-24")])]}),"instanceName":"1"});
            var Q31;
            Q31=makeQuery(id+"F23.opPattern","COPY",BODY,{"derivedFrom":makeQuery(id+"F21.opExtrude","SWEPT_BODY",BODY,{"disambiguationData":[OSD([sQuery(id+"F20.wireOp",EDGE,"E14.sketch_text.stroke-0"),sQuery(id+"F20.wireOp",EDGE,"E14.sketch_text.stroke-1"),sQuery(id+"F20.wireOp",EDGE,"E14.sketch_text.stroke-2"),sQuery(id+"F20.wireOp",EDGE,"E14.sketch_text.stroke-3"),sQuery(id+"F20.wireOp",EDGE,"E14.sketch_text.stroke-4"),sQuery(id+"F20.wireOp",EDGE,"E14.sketch_text.stroke-5"),sQuery(id+"F20.wireOp",EDGE,"E14.sketch_text.stroke-6"),sQuery(id+"F20.wireOp",EDGE,"E14.sketch_text.stroke-7"),sQuery(id+"F20.wireOp",EDGE,"E14.sketch_text.stroke-8")])]}),"instanceName":"1"});
            var Q32;
            Q32=sQuery(id+"F14.wireOp",EDGE,"E13");
            circularPattern(context, id + "F38", {"entities" : qUnion([Q0, Q1, Q2, Q3, Q4, Q5, Q6, Q7, Q8, Q9, Q10, Q11, Q12, Q13, Q14, Q15, Q16, Q17, Q18, Q19, Q20, Q21, Q22, Q23, Q24, Q25, Q26, Q27, Q28, Q29, Q30, Q31]), "axis" : qUnion([Q32]), "angle" : 360 * degree, "instanceCount" : 4, "equalSpace" : true});
        }
        {
            var Q0;
            Q0=makeQuery(id+"F22.opPattern","COPY",BODY,{"derivedFrom":makeQuery(id+"F21.opExtrude","SWEPT_BODY",BODY,{"disambiguationData":[OSD([sQuery(id+"F20.wireOp",EDGE,"E14.sketch_text.stroke-0"),sQuery(id+"F20.wireOp",EDGE,"E14.sketch_text.stroke-1"),sQuery(id+"F20.wireOp",EDGE,"E14.sketch_text.stroke-2"),sQuery(id+"F20.wireOp",EDGE,"E14.sketch_text.stroke-3"),sQuery(id+"F20.wireOp",EDGE,"E14.sketch_text.stroke-4"),sQuery(id+"F20.wireOp",EDGE,"E14.sketch_text.stroke-5"),sQuery(id+"F20.wireOp",EDGE,"E14.sketch_text.stroke-6"),sQuery(id+"F20.wireOp",EDGE,"E14.sketch_text.stroke-7"),sQuery(id+"F20.wireOp",EDGE,"E14.sketch_text.stroke-8")])]}),"instanceName":"1"});
            var Q1;
            Q1=makeQuery(id+"F22.opPattern","COPY",BODY,{"derivedFrom":makeQuery(id+"F21.opExtrude","SWEPT_BODY",BODY,{"disambiguationData":[OSD([sQuery(id+"F20.wireOp",EDGE,"E15.sketch_text.stroke-0"),sQuery(id+"F20.wireOp",EDGE,"E15.sketch_text.stroke-1"),sQuery(id+"F20.wireOp",EDGE,"E15.sketch_text.stroke-2"),sQuery(id+"F20.wireOp",EDGE,"E15.sketch_text.stroke-3"),sQuery(id+"F20.wireOp",EDGE,"E15.sketch_text.stroke-4"),sQuery(id+"F20.wireOp",EDGE,"E15.sketch_text.stroke-5"),sQuery(id+"F20.wireOp",EDGE,"E15.sketch_text.stroke-6"),sQuery(id+"F20.wireOp",EDGE,"E15.sketch_text.stroke-7"),sQuery(id+"F20.wireOp",EDGE,"E15.sketch_text.stroke-8"),sQuery(id+"F20.wireOp",EDGE,"E15.sketch_text.stroke-9"),sQuery(id+"F20.wireOp",EDGE,"E15.sketch_text.stroke-10"),sQuery(id+"F20.wireOp",EDGE,"E15.sketch_text.stroke-11"),sQuery(id+"F20.wireOp",EDGE,"E15.sketch_text.stroke-12"),sQuery(id+"F20.wireOp",EDGE,"E15.sketch_text.stroke-13"),sQuery(id+"F20.wireOp",EDGE,"E15.sketch_text.stroke-14"),sQuery(id+"F20.wireOp",EDGE,"E15.sketch_text.stroke-15"),sQuery(id+"F20.wireOp",EDGE,"E15.sketch_text.stroke-16"),sQuery(id+"F20.wireOp",EDGE,"E15.sketch_text.stroke-17"),sQuery(id+"F20.wireOp",EDGE,"E15.sketch_text.stroke-18"),sQuery(id+"F20.wireOp",EDGE,"E15.sketch_text.stroke-19")])]}),"instanceName":"1"});
            var Q2;
            Q2=makeQuery(id+"F22.opPattern","COPY",BODY,{"derivedFrom":makeQuery(id+"F21.opExtrude","SWEPT_BODY",BODY,{"disambiguationData":[OSD([sQuery(id+"F20.wireOp",EDGE,"E16.sketch_text.stroke-0"),sQuery(id+"F20.wireOp",EDGE,"E16.sketch_text.stroke-1"),sQuery(id+"F20.wireOp",EDGE,"E16.sketch_text.stroke-2"),sQuery(id+"F20.wireOp",EDGE,"E16.sketch_text.stroke-3"),sQuery(id+"F20.wireOp",EDGE,"E16.sketch_text.stroke-4"),sQuery(id+"F20.wireOp",EDGE,"E16.sketch_text.stroke-5"),sQuery(id+"F20.wireOp",EDGE,"E16.sketch_text.stroke-6"),sQuery(id+"F20.wireOp",EDGE,"E16.sketch_text.stroke-7"),sQuery(id+"F20.wireOp",EDGE,"E16.sketch_text.stroke-8"),sQuery(id+"F20.wireOp",EDGE,"E16.sketch_text.stroke-9"),sQuery(id+"F20.wireOp",EDGE,"E16.sketch_text.stroke-10"),sQuery(id+"F20.wireOp",EDGE,"E16.sketch_text.stroke-11"),sQuery(id+"F20.wireOp",EDGE,"E16.sketch_text.stroke-12"),sQuery(id+"F20.wireOp",EDGE,"E16.sketch_text.stroke-13"),sQuery(id+"F20.wireOp",EDGE,"E16.sketch_text.stroke-14"),sQuery(id+"F20.wireOp",EDGE,"E16.sketch_text.stroke-15"),sQuery(id+"F20.wireOp",EDGE,"E16.sketch_text.stroke-16"),sQuery(id+"F20.wireOp",EDGE,"E16.sketch_text.stroke-17"),sQuery(id+"F20.wireOp",EDGE,"E16.sketch_text.stroke-18"),sQuery(id+"F20.wireOp",EDGE,"E16.sketch_text.stroke-19"),sQuery(id+"F20.wireOp",EDGE,"E16.sketch_text.stroke-20"),sQuery(id+"F20.wireOp",EDGE,"E16.sketch_text.stroke-21"),sQuery(id+"F20.wireOp",EDGE,"E16.sketch_text.stroke-22"),sQuery(id+"F20.wireOp",EDGE,"E16.sketch_text.stroke-23"),sQuery(id+"F20.wireOp",EDGE,"E16.sketch_text.stroke-24"),sQuery(id+"F20.wireOp",EDGE,"E16.sketch_text.stroke-25"),sQuery(id+"F20.wireOp",EDGE,"E16.sketch_text.stroke-26"),sQuery(id+"F20.wireOp",EDGE,"E16.sketch_text.stroke-27")])]}),"instanceName":"1"});
            var Q3;
            Q3=makeQuery(id+"F22.opPattern","COPY",BODY,{"derivedFrom":makeQuery(id+"F21.opExtrude","SWEPT_BODY",BODY,{"disambiguationData":[OSD([sQuery(id+"F20.wireOp",EDGE,"E17.sketch_text.stroke-0"),sQuery(id+"F20.wireOp",EDGE,"E17.sketch_text.stroke-1"),sQuery(id+"F20.wireOp",EDGE,"E17.sketch_text.stroke-2"),sQuery(id+"F20.wireOp",EDGE,"E17.sketch_text.stroke-3"),sQuery(id+"F20.wireOp",EDGE,"E17.sketch_text.stroke-4"),sQuery(id+"F20.wireOp",EDGE,"E17.sketch_text.stroke-5"),sQuery(id+"F20.wireOp",EDGE,"E17.sketch_text.stroke-6"),sQuery(id+"F20.wireOp",EDGE,"E17.sketch_text.stroke-7"),sQuery(id+"F20.wireOp",EDGE,"E17.sketch_text.stroke-8"),sQuery(id+"F20.wireOp",EDGE,"E17.sketch_text.stroke-9"),sQuery(id+"F20.wireOp",EDGE,"E17.sketch_text.stroke-10"),sQuery(id+"F20.wireOp",EDGE,"E17.sketch_text.stroke-11"),sQuery(id+"F20.wireOp",EDGE,"E17.sketch_text.stroke-12"),sQuery(id+"F20.wireOp",EDGE,"E17.sketch_text.stroke-13"),sQuery(id+"F20.wireOp",EDGE,"E17.sketch_text.stroke-14"),sQuery(id+"F20.wireOp",EDGE,"E17.sketch_text.stroke-15"),sQuery(id+"F20.wireOp",EDGE,"E17.sketch_text.stroke-16")])]}),"instanceName":"1"});
            var Q4;
            Q4=makeQuery(id+"F22.opPattern","COPY",BODY,{"derivedFrom":makeQuery(id+"F21.opExtrude","SWEPT_BODY",BODY,{"disambiguationData":[OSD([sQuery(id+"F20.wireOp",EDGE,"E18.sketch_text.stroke-0"),sQuery(id+"F20.wireOp",EDGE,"E18.sketch_text.stroke-1"),sQuery(id+"F20.wireOp",EDGE,"E18.sketch_text.stroke-2"),sQuery(id+"F20.wireOp",EDGE,"E18.sketch_text.stroke-3"),sQuery(id+"F20.wireOp",EDGE,"E18.sketch_text.stroke-4"),sQuery(id+"F20.wireOp",EDGE,"E18.sketch_text.stroke-5"),sQuery(id+"F20.wireOp",EDGE,"E18.sketch_text.stroke-6"),sQuery(id+"F20.wireOp",EDGE,"E18.sketch_text.stroke-7"),sQuery(id+"F20.wireOp",EDGE,"E18.sketch_text.stroke-8"),sQuery(id+"F20.wireOp",EDGE,"E18.sketch_text.stroke-9"),sQuery(id+"F20.wireOp",EDGE,"E18.sketch_text.stroke-10"),sQuery(id+"F20.wireOp",EDGE,"E18.sketch_text.stroke-11"),sQuery(id+"F20.wireOp",EDGE,"E18.sketch_text.stroke-12"),sQuery(id+"F20.wireOp",EDGE,"E18.sketch_text.stroke-13"),sQuery(id+"F20.wireOp",EDGE,"E18.sketch_text.stroke-14"),sQuery(id+"F20.wireOp",EDGE,"E18.sketch_text.stroke-15"),sQuery(id+"F20.wireOp",EDGE,"E18.sketch_text.stroke-16"),sQuery(id+"F20.wireOp",EDGE,"E18.sketch_text.stroke-17"),sQuery(id+"F20.wireOp",EDGE,"E18.sketch_text.stroke-18")])]}),"instanceName":"1"});
            var Q5;
            Q5=makeQuery(id+"F22.opPattern","COPY",BODY,{"derivedFrom":makeQuery(id+"F21.opExtrude","SWEPT_BODY",BODY,{"disambiguationData":[OSD([sQuery(id+"F20.wireOp",EDGE,"E19.sketch_text.stroke-0"),sQuery(id+"F20.wireOp",EDGE,"E19.sketch_text.stroke-1"),sQuery(id+"F20.wireOp",EDGE,"E19.sketch_text.stroke-2"),sQuery(id+"F20.wireOp",EDGE,"E19.sketch_text.stroke-3"),sQuery(id+"F20.wireOp",EDGE,"E19.sketch_text.stroke-4"),sQuery(id+"F20.wireOp",EDGE,"E19.sketch_text.stroke-5"),sQuery(id+"F20.wireOp",EDGE,"E19.sketch_text.stroke-6"),sQuery(id+"F20.wireOp",EDGE,"E19.sketch_text.stroke-7"),sQuery(id+"F20.wireOp",EDGE,"E19.sketch_text.stroke-8"),sQuery(id+"F20.wireOp",EDGE,"E19.sketch_text.stroke-9"),sQuery(id+"F20.wireOp",EDGE,"E19.sketch_text.stroke-10"),sQuery(id+"F20.wireOp",EDGE,"E19.sketch_text.stroke-11"),sQuery(id+"F20.wireOp",EDGE,"E19.sketch_text.stroke-12"),sQuery(id+"F20.wireOp",EDGE,"E19.sketch_text.stroke-13"),sQuery(id+"F20.wireOp",EDGE,"E19.sketch_text.stroke-14"),sQuery(id+"F20.wireOp",EDGE,"E19.sketch_text.stroke-15"),sQuery(id+"F20.wireOp",EDGE,"E19.sketch_text.stroke-16"),sQuery(id+"F20.wireOp",EDGE,"E19.sketch_text.stroke-17"),sQuery(id+"F20.wireOp",EDGE,"E19.sketch_text.stroke-18"),sQuery(id+"F20.wireOp",EDGE,"E19.sketch_text.stroke-19"),sQuery(id+"F20.wireOp",EDGE,"E19.sketch_text.stroke-20"),sQuery(id+"F20.wireOp",EDGE,"E19.sketch_text.stroke-21"),sQuery(id+"F20.wireOp",EDGE,"E19.sketch_text.stroke-22"),sQuery(id+"F20.wireOp",EDGE,"E19.sketch_text.stroke-23"),sQuery(id+"F20.wireOp",EDGE,"E19.sketch_text.stroke-24")])]}),"instanceName":"1"});
            var Q6;
            Q6=makeQuery(id+"F22.opPattern","COPY",BODY,{"derivedFrom":makeQuery(id+"F21.opExtrude","SWEPT_BODY",BODY,{"disambiguationData":[OSD([sQuery(id+"F20.wireOp",EDGE,"E20.sketch_text.stroke-0"),sQuery(id+"F20.wireOp",EDGE,"E20.sketch_text.stroke-1"),sQuery(id+"F20.wireOp",EDGE,"E20.sketch_text.stroke-2"),sQuery(id+"F20.wireOp",EDGE,"E20.sketch_text.stroke-3"),sQuery(id+"F20.wireOp",EDGE,"E20.sketch_text.stroke-4"),sQuery(id+"F20.wireOp",EDGE,"E20.sketch_text.stroke-5"),sQuery(id+"F20.wireOp",EDGE,"E20.sketch_text.stroke-6")])]}),"instanceName":"1"});
            var Q7;
            Q7=makeQuery(id+"F22.opPattern","COPY",BODY,{"derivedFrom":makeQuery(id+"F21.opExtrude","SWEPT_BODY",BODY,{"disambiguationData":[OSD([sQuery(id+"F20.wireOp",EDGE,"E21.sketch_text.stroke-0"),sQuery(id+"F20.wireOp",EDGE,"E21.sketch_text.stroke-1"),sQuery(id+"F20.wireOp",EDGE,"E21.sketch_text.stroke-2"),sQuery(id+"F20.wireOp",EDGE,"E21.sketch_text.stroke-3"),sQuery(id+"F20.wireOp",EDGE,"E21.sketch_text.stroke-4"),sQuery(id+"F20.wireOp",EDGE,"E21.sketch_text.stroke-5"),sQuery(id+"F20.wireOp",EDGE,"E21.sketch_text.stroke-6"),sQuery(id+"F20.wireOp",EDGE,"E21.sketch_text.stroke-7"),sQuery(id+"F20.wireOp",EDGE,"E21.sketch_text.stroke-8"),sQuery(id+"F20.wireOp",EDGE,"E21.sketch_text.stroke-9"),sQuery(id+"F20.wireOp",EDGE,"E21.sketch_text.stroke-10"),sQuery(id+"F20.wireOp",EDGE,"E21.sketch_text.stroke-11"),sQuery(id+"F20.wireOp",EDGE,"E21.sketch_text.stroke-12"),sQuery(id+"F20.wireOp",EDGE,"E21.sketch_text.stroke-13"),sQuery(id+"F20.wireOp",EDGE,"E21.sketch_text.stroke-14"),sQuery(id+"F20.wireOp",EDGE,"E21.sketch_text.stroke-15"),sQuery(id+"F20.wireOp",EDGE,"E21.sketch_text.stroke-16"),sQuery(id+"F20.wireOp",EDGE,"E21.sketch_text.stroke-17"),sQuery(id+"F20.wireOp",EDGE,"E21.sketch_text.stroke-18"),sQuery(id+"F20.wireOp",EDGE,"E21.sketch_text.stroke-19"),sQuery(id+"F20.wireOp",EDGE,"E21.sketch_text.stroke-20"),sQuery(id+"F20.wireOp",EDGE,"E21.sketch_text.stroke-21"),sQuery(id+"F20.wireOp",EDGE,"E21.sketch_text.stroke-22"),sQuery(id+"F20.wireOp",EDGE,"E21.sketch_text.stroke-23"),sQuery(id+"F20.wireOp",EDGE,"E21.sketch_text.stroke-24"),sQuery(id+"F20.wireOp",EDGE,"E21.sketch_text.stroke-25"),sQuery(id+"F20.wireOp",EDGE,"E21.sketch_text.stroke-26"),sQuery(id+"F20.wireOp",EDGE,"E21.sketch_text.stroke-27"),sQuery(id+"F20.wireOp",EDGE,"E21.sketch_text.stroke-28"),sQuery(id+"F20.wireOp",EDGE,"E21.sketch_text.stroke-29"),sQuery(id+"F20.wireOp",EDGE,"E21.sketch_text.stroke-30")])]}),"instanceName":"1"});
            var Q8;
            Q8=makeQuery(id+"F22.opPattern","COPY",BODY,{"derivedFrom":makeQuery(id+"F21.opExtrude","SWEPT_BODY",BODY,{"disambiguationData":[OSD([sQuery(id+"F20.wireOp",EDGE,"E22.sketch_text.stroke-0"),sQuery(id+"F20.wireOp",EDGE,"E22.sketch_text.stroke-1"),sQuery(id+"F20.wireOp",EDGE,"E22.sketch_text.stroke-2"),sQuery(id+"F20.wireOp",EDGE,"E22.sketch_text.stroke-3"),sQuery(id+"F20.wireOp",EDGE,"E22.sketch_text.stroke-4"),sQuery(id+"F20.wireOp",EDGE,"E22.sketch_text.stroke-5"),sQuery(id+"F20.wireOp",EDGE,"E22.sketch_text.stroke-6"),sQuery(id+"F20.wireOp",EDGE,"E22.sketch_text.stroke-7"),sQuery(id+"F20.wireOp",EDGE,"E22.sketch_text.stroke-8"),sQuery(id+"F20.wireOp",EDGE,"E22.sketch_text.stroke-9"),sQuery(id+"F20.wireOp",EDGE,"E22.sketch_text.stroke-10"),sQuery(id+"F20.wireOp",EDGE,"E22.sketch_text.stroke-11"),sQuery(id+"F20.wireOp",EDGE,"E22.sketch_text.stroke-12"),sQuery(id+"F20.wireOp",EDGE,"E22.sketch_text.stroke-13"),sQuery(id+"F20.wireOp",EDGE,"E22.sketch_text.stroke-14"),sQuery(id+"F20.wireOp",EDGE,"E22.sketch_text.stroke-15"),sQuery(id+"F20.wireOp",EDGE,"E22.sketch_text.stroke-16"),sQuery(id+"F20.wireOp",EDGE,"E22.sketch_text.stroke-17"),sQuery(id+"F20.wireOp",EDGE,"E22.sketch_text.stroke-18"),sQuery(id+"F20.wireOp",EDGE,"E22.sketch_text.stroke-19"),sQuery(id+"F20.wireOp",EDGE,"E22.sketch_text.stroke-20"),sQuery(id+"F20.wireOp",EDGE,"E22.sketch_text.stroke-21"),sQuery(id+"F20.wireOp",EDGE,"E22.sketch_text.stroke-22"),sQuery(id+"F20.wireOp",EDGE,"E22.sketch_text.stroke-23"),sQuery(id+"F20.wireOp",EDGE,"E22.sketch_text.stroke-24"),sQuery(id+"F20.wireOp",EDGE,"E22.sketch_text.stroke-25")])]}),"instanceName":"1"});
            var Q9;
            Q9=makeQuery(id+"F22.opPattern","COPY",BODY,{"derivedFrom":makeQuery(id+"F21.opExtrude","SWEPT_BODY",BODY,{"disambiguationData":[OSD([sQuery(id+"F20.wireOp",EDGE,"E23.sketch_text.stroke-0"),sQuery(id+"F20.wireOp",EDGE,"E23.sketch_text.stroke-1"),sQuery(id+"F20.wireOp",EDGE,"E23.sketch_text.stroke-2"),sQuery(id+"F20.wireOp",EDGE,"E23.sketch_text.stroke-3"),sQuery(id+"F20.wireOp",EDGE,"E23.sketch_text.stroke-4"),sQuery(id+"F20.wireOp",EDGE,"E23.sketch_text.stroke-5"),sQuery(id+"F20.wireOp",EDGE,"E23.sketch_text.stroke-6"),sQuery(id+"F20.wireOp",EDGE,"E23.sketch_text.stroke-7"),sQuery(id+"F20.wireOp",EDGE,"E23.sketch_text.stroke-8")])]}),"instanceName":"1"});
            var Q10;
            Q10=makeQuery(id+"F22.opPattern","COPY",BODY,{"derivedFrom":makeQuery(id+"F21.opExtrude","SWEPT_BODY",BODY,{"disambiguationData":[OSD([sQuery(id+"F20.wireOp",EDGE,"E23.sketch_text.stroke-9"),sQuery(id+"F20.wireOp",EDGE,"E23.sketch_text.stroke-10"),sQuery(id+"F20.wireOp",EDGE,"E23.sketch_text.stroke-11"),sQuery(id+"F20.wireOp",EDGE,"E23.sketch_text.stroke-12"),sQuery(id+"F20.wireOp",EDGE,"E23.sketch_text.stroke-13"),sQuery(id+"F20.wireOp",EDGE,"E23.sketch_text.stroke-14"),sQuery(id+"F20.wireOp",EDGE,"E23.sketch_text.stroke-15"),sQuery(id+"F20.wireOp",EDGE,"E23.sketch_text.stroke-16"),sQuery(id+"F20.wireOp",EDGE,"E23.sketch_text.stroke-17"),sQuery(id+"F20.wireOp",EDGE,"E23.sketch_text.stroke-18"),sQuery(id+"F20.wireOp",EDGE,"E23.sketch_text.stroke-19"),sQuery(id+"F20.wireOp",EDGE,"E23.sketch_text.stroke-20"),sQuery(id+"F20.wireOp",EDGE,"E23.sketch_text.stroke-21"),sQuery(id+"F20.wireOp",EDGE,"E23.sketch_text.stroke-22"),sQuery(id+"F20.wireOp",EDGE,"E23.sketch_text.stroke-23"),sQuery(id+"F20.wireOp",EDGE,"E23.sketch_text.stroke-24")])]}),"instanceName":"1"});
            var Q11;
            Q11=makeQuery(id+"F26.opPattern","COPY",BODY,{"derivedFrom":makeQuery(id+"F25.opExtrude","SWEPT_BODY",BODY,{"disambiguationData":[OSD([sQuery(id+"F24.wireOp",EDGE,"E24.sketch_text.stroke-0"),sQuery(id+"F24.wireOp",EDGE,"E24.sketch_text.stroke-1"),sQuery(id+"F24.wireOp",EDGE,"E24.sketch_text.stroke-2"),sQuery(id+"F24.wireOp",EDGE,"E24.sketch_text.stroke-3"),sQuery(id+"F24.wireOp",EDGE,"E24.sketch_text.stroke-4"),sQuery(id+"F24.wireOp",EDGE,"E24.sketch_text.stroke-5"),sQuery(id+"F24.wireOp",EDGE,"E24.sketch_text.stroke-6"),sQuery(id+"F24.wireOp",EDGE,"E24.sketch_text.stroke-7"),sQuery(id+"F24.wireOp",EDGE,"E24.sketch_text.stroke-8")])]}),"instanceName":"1"});
            var Q12;
            Q12=makeQuery(id+"F26.opPattern","COPY",BODY,{"derivedFrom":makeQuery(id+"F25.opExtrude","SWEPT_BODY",BODY,{"disambiguationData":[OSD([sQuery(id+"F24.wireOp",EDGE,"E25.sketch_text.stroke-0"),sQuery(id+"F24.wireOp",EDGE,"E25.sketch_text.stroke-1"),sQuery(id+"F24.wireOp",EDGE,"E25.sketch_text.stroke-2"),sQuery(id+"F24.wireOp",EDGE,"E25.sketch_text.stroke-3"),sQuery(id+"F24.wireOp",EDGE,"E25.sketch_text.stroke-4"),sQuery(id+"F24.wireOp",EDGE,"E25.sketch_text.stroke-5"),sQuery(id+"F24.wireOp",EDGE,"E25.sketch_text.stroke-6"),sQuery(id+"F24.wireOp",EDGE,"E25.sketch_text.stroke-7"),sQuery(id+"F24.wireOp",EDGE,"E25.sketch_text.stroke-8"),sQuery(id+"F24.wireOp",EDGE,"E25.sketch_text.stroke-9"),sQuery(id+"F24.wireOp",EDGE,"E25.sketch_text.stroke-10"),sQuery(id+"F24.wireOp",EDGE,"E25.sketch_text.stroke-11"),sQuery(id+"F24.wireOp",EDGE,"E25.sketch_text.stroke-12"),sQuery(id+"F24.wireOp",EDGE,"E25.sketch_text.stroke-13"),sQuery(id+"F24.wireOp",EDGE,"E25.sketch_text.stroke-14"),sQuery(id+"F24.wireOp",EDGE,"E25.sketch_text.stroke-15"),sQuery(id+"F24.wireOp",EDGE,"E25.sketch_text.stroke-16"),sQuery(id+"F24.wireOp",EDGE,"E25.sketch_text.stroke-17"),sQuery(id+"F24.wireOp",EDGE,"E25.sketch_text.stroke-18"),sQuery(id+"F24.wireOp",EDGE,"E25.sketch_text.stroke-19")])]}),"instanceName":"1"});
            var Q13;
            Q13=makeQuery(id+"F26.opPattern","COPY",BODY,{"derivedFrom":makeQuery(id+"F25.opExtrude","SWEPT_BODY",BODY,{"disambiguationData":[OSD([sQuery(id+"F24.wireOp",EDGE,"E26.sketch_text.stroke-0"),sQuery(id+"F24.wireOp",EDGE,"E26.sketch_text.stroke-1"),sQuery(id+"F24.wireOp",EDGE,"E26.sketch_text.stroke-2"),sQuery(id+"F24.wireOp",EDGE,"E26.sketch_text.stroke-3"),sQuery(id+"F24.wireOp",EDGE,"E26.sketch_text.stroke-4"),sQuery(id+"F24.wireOp",EDGE,"E26.sketch_text.stroke-5"),sQuery(id+"F24.wireOp",EDGE,"E26.sketch_text.stroke-6"),sQuery(id+"F24.wireOp",EDGE,"E26.sketch_text.stroke-7"),sQuery(id+"F24.wireOp",EDGE,"E26.sketch_text.stroke-8"),sQuery(id+"F24.wireOp",EDGE,"E26.sketch_text.stroke-9"),sQuery(id+"F24.wireOp",EDGE,"E26.sketch_text.stroke-10"),sQuery(id+"F24.wireOp",EDGE,"E26.sketch_text.stroke-11"),sQuery(id+"F24.wireOp",EDGE,"E26.sketch_text.stroke-12"),sQuery(id+"F24.wireOp",EDGE,"E26.sketch_text.stroke-13"),sQuery(id+"F24.wireOp",EDGE,"E26.sketch_text.stroke-14"),sQuery(id+"F24.wireOp",EDGE,"E26.sketch_text.stroke-15"),sQuery(id+"F24.wireOp",EDGE,"E26.sketch_text.stroke-16"),sQuery(id+"F24.wireOp",EDGE,"E26.sketch_text.stroke-17"),sQuery(id+"F24.wireOp",EDGE,"E26.sketch_text.stroke-18"),sQuery(id+"F24.wireOp",EDGE,"E26.sketch_text.stroke-19"),sQuery(id+"F24.wireOp",EDGE,"E26.sketch_text.stroke-20"),sQuery(id+"F24.wireOp",EDGE,"E26.sketch_text.stroke-21"),sQuery(id+"F24.wireOp",EDGE,"E26.sketch_text.stroke-22"),sQuery(id+"F24.wireOp",EDGE,"E26.sketch_text.stroke-23"),sQuery(id+"F24.wireOp",EDGE,"E26.sketch_text.stroke-24"),sQuery(id+"F24.wireOp",EDGE,"E26.sketch_text.stroke-25"),sQuery(id+"F24.wireOp",EDGE,"E26.sketch_text.stroke-26"),sQuery(id+"F24.wireOp",EDGE,"E26.sketch_text.stroke-27")])]}),"instanceName":"1"});
            var Q14;
            Q14=makeQuery(id+"F26.opPattern","COPY",BODY,{"derivedFrom":makeQuery(id+"F25.opExtrude","SWEPT_BODY",BODY,{"disambiguationData":[OSD([sQuery(id+"F24.wireOp",EDGE,"E27.sketch_text.stroke-0"),sQuery(id+"F24.wireOp",EDGE,"E27.sketch_text.stroke-1"),sQuery(id+"F24.wireOp",EDGE,"E27.sketch_text.stroke-2"),sQuery(id+"F24.wireOp",EDGE,"E27.sketch_text.stroke-3"),sQuery(id+"F24.wireOp",EDGE,"E27.sketch_text.stroke-4"),sQuery(id+"F24.wireOp",EDGE,"E27.sketch_text.stroke-5"),sQuery(id+"F24.wireOp",EDGE,"E27.sketch_text.stroke-6"),sQuery(id+"F24.wireOp",EDGE,"E27.sketch_text.stroke-7"),sQuery(id+"F24.wireOp",EDGE,"E27.sketch_text.stroke-8"),sQuery(id+"F24.wireOp",EDGE,"E27.sketch_text.stroke-9"),sQuery(id+"F24.wireOp",EDGE,"E27.sketch_text.stroke-10"),sQuery(id+"F24.wireOp",EDGE,"E27.sketch_text.stroke-11"),sQuery(id+"F24.wireOp",EDGE,"E27.sketch_text.stroke-12"),sQuery(id+"F24.wireOp",EDGE,"E27.sketch_text.stroke-13"),sQuery(id+"F24.wireOp",EDGE,"E27.sketch_text.stroke-14"),sQuery(id+"F24.wireOp",EDGE,"E27.sketch_text.stroke-15"),sQuery(id+"F24.wireOp",EDGE,"E27.sketch_text.stroke-16")])]}),"instanceName":"1"});
            var Q15;
            Q15=makeQuery(id+"F26.opPattern","COPY",BODY,{"derivedFrom":makeQuery(id+"F25.opExtrude","SWEPT_BODY",BODY,{"disambiguationData":[OSD([sQuery(id+"F24.wireOp",EDGE,"E28.sketch_text.stroke-0"),sQuery(id+"F24.wireOp",EDGE,"E28.sketch_text.stroke-1"),sQuery(id+"F24.wireOp",EDGE,"E28.sketch_text.stroke-2"),sQuery(id+"F24.wireOp",EDGE,"E28.sketch_text.stroke-3"),sQuery(id+"F24.wireOp",EDGE,"E28.sketch_text.stroke-4"),sQuery(id+"F24.wireOp",EDGE,"E28.sketch_text.stroke-5"),sQuery(id+"F24.wireOp",EDGE,"E28.sketch_text.stroke-6"),sQuery(id+"F24.wireOp",EDGE,"E28.sketch_text.stroke-7"),sQuery(id+"F24.wireOp",EDGE,"E28.sketch_text.stroke-8"),sQuery(id+"F24.wireOp",EDGE,"E28.sketch_text.stroke-9"),sQuery(id+"F24.wireOp",EDGE,"E28.sketch_text.stroke-10"),sQuery(id+"F24.wireOp",EDGE,"E28.sketch_text.stroke-11"),sQuery(id+"F24.wireOp",EDGE,"E28.sketch_text.stroke-12"),sQuery(id+"F24.wireOp",EDGE,"E28.sketch_text.stroke-13"),sQuery(id+"F24.wireOp",EDGE,"E28.sketch_text.stroke-14"),sQuery(id+"F24.wireOp",EDGE,"E28.sketch_text.stroke-15"),sQuery(id+"F24.wireOp",EDGE,"E28.sketch_text.stroke-16"),sQuery(id+"F24.wireOp",EDGE,"E28.sketch_text.stroke-17"),sQuery(id+"F24.wireOp",EDGE,"E28.sketch_text.stroke-18")])]}),"instanceName":"1"});
            var Q16;
            Q16=makeQuery(id+"F26.opPattern","COPY",BODY,{"derivedFrom":makeQuery(id+"F25.opExtrude","SWEPT_BODY",BODY,{"disambiguationData":[OSD([sQuery(id+"F24.wireOp",EDGE,"E29.sketch_text.stroke-0"),sQuery(id+"F24.wireOp",EDGE,"E29.sketch_text.stroke-1"),sQuery(id+"F24.wireOp",EDGE,"E29.sketch_text.stroke-2"),sQuery(id+"F24.wireOp",EDGE,"E29.sketch_text.stroke-3"),sQuery(id+"F24.wireOp",EDGE,"E29.sketch_text.stroke-4"),sQuery(id+"F24.wireOp",EDGE,"E29.sketch_text.stroke-5"),sQuery(id+"F24.wireOp",EDGE,"E29.sketch_text.stroke-6"),sQuery(id+"F24.wireOp",EDGE,"E29.sketch_text.stroke-7"),sQuery(id+"F24.wireOp",EDGE,"E29.sketch_text.stroke-8"),sQuery(id+"F24.wireOp",EDGE,"E29.sketch_text.stroke-9"),sQuery(id+"F24.wireOp",EDGE,"E29.sketch_text.stroke-10"),sQuery(id+"F24.wireOp",EDGE,"E29.sketch_text.stroke-11"),sQuery(id+"F24.wireOp",EDGE,"E29.sketch_text.stroke-12"),sQuery(id+"F24.wireOp",EDGE,"E29.sketch_text.stroke-13"),sQuery(id+"F24.wireOp",EDGE,"E29.sketch_text.stroke-14"),sQuery(id+"F24.wireOp",EDGE,"E29.sketch_text.stroke-15"),sQuery(id+"F24.wireOp",EDGE,"E29.sketch_text.stroke-16"),sQuery(id+"F24.wireOp",EDGE,"E29.sketch_text.stroke-17"),sQuery(id+"F24.wireOp",EDGE,"E29.sketch_text.stroke-18"),sQuery(id+"F24.wireOp",EDGE,"E29.sketch_text.stroke-19"),sQuery(id+"F24.wireOp",EDGE,"E29.sketch_text.stroke-20"),sQuery(id+"F24.wireOp",EDGE,"E29.sketch_text.stroke-21"),sQuery(id+"F24.wireOp",EDGE,"E29.sketch_text.stroke-22"),sQuery(id+"F24.wireOp",EDGE,"E29.sketch_text.stroke-23"),sQuery(id+"F24.wireOp",EDGE,"E29.sketch_text.stroke-24")])]}),"instanceName":"1"});
            var Q17;
            Q17=makeQuery(id+"F26.opPattern","COPY",BODY,{"derivedFrom":makeQuery(id+"F25.opExtrude","SWEPT_BODY",BODY,{"disambiguationData":[OSD([sQuery(id+"F24.wireOp",EDGE,"E30.sketch_text.stroke-0"),sQuery(id+"F24.wireOp",EDGE,"E30.sketch_text.stroke-1"),sQuery(id+"F24.wireOp",EDGE,"E30.sketch_text.stroke-2"),sQuery(id+"F24.wireOp",EDGE,"E30.sketch_text.stroke-3"),sQuery(id+"F24.wireOp",EDGE,"E30.sketch_text.stroke-4"),sQuery(id+"F24.wireOp",EDGE,"E30.sketch_text.stroke-5"),sQuery(id+"F24.wireOp",EDGE,"E30.sketch_text.stroke-6")])]}),"instanceName":"1"});
            var Q18;
            Q18=makeQuery(id+"F26.opPattern","COPY",BODY,{"derivedFrom":makeQuery(id+"F25.opExtrude","SWEPT_BODY",BODY,{"disambiguationData":[OSD([sQuery(id+"F24.wireOp",EDGE,"E31.sketch_text.stroke-0"),sQuery(id+"F24.wireOp",EDGE,"E31.sketch_text.stroke-1"),sQuery(id+"F24.wireOp",EDGE,"E31.sketch_text.stroke-2"),sQuery(id+"F24.wireOp",EDGE,"E31.sketch_text.stroke-3"),sQuery(id+"F24.wireOp",EDGE,"E31.sketch_text.stroke-4"),sQuery(id+"F24.wireOp",EDGE,"E31.sketch_text.stroke-5"),sQuery(id+"F24.wireOp",EDGE,"E31.sketch_text.stroke-6"),sQuery(id+"F24.wireOp",EDGE,"E31.sketch_text.stroke-7"),sQuery(id+"F24.wireOp",EDGE,"E31.sketch_text.stroke-8"),sQuery(id+"F24.wireOp",EDGE,"E31.sketch_text.stroke-9"),sQuery(id+"F24.wireOp",EDGE,"E31.sketch_text.stroke-10"),sQuery(id+"F24.wireOp",EDGE,"E31.sketch_text.stroke-11"),sQuery(id+"F24.wireOp",EDGE,"E31.sketch_text.stroke-12"),sQuery(id+"F24.wireOp",EDGE,"E31.sketch_text.stroke-13"),sQuery(id+"F24.wireOp",EDGE,"E31.sketch_text.stroke-14"),sQuery(id+"F24.wireOp",EDGE,"E31.sketch_text.stroke-15"),sQuery(id+"F24.wireOp",EDGE,"E31.sketch_text.stroke-16"),sQuery(id+"F24.wireOp",EDGE,"E31.sketch_text.stroke-17"),sQuery(id+"F24.wireOp",EDGE,"E31.sketch_text.stroke-18"),sQuery(id+"F24.wireOp",EDGE,"E31.sketch_text.stroke-19"),sQuery(id+"F24.wireOp",EDGE,"E31.sketch_text.stroke-20"),sQuery(id+"F24.wireOp",EDGE,"E31.sketch_text.stroke-21"),sQuery(id+"F24.wireOp",EDGE,"E31.sketch_text.stroke-22"),sQuery(id+"F24.wireOp",EDGE,"E31.sketch_text.stroke-23"),sQuery(id+"F24.wireOp",EDGE,"E31.sketch_text.stroke-24"),sQuery(id+"F24.wireOp",EDGE,"E31.sketch_text.stroke-25"),sQuery(id+"F24.wireOp",EDGE,"E31.sketch_text.stroke-26"),sQuery(id+"F24.wireOp",EDGE,"E31.sketch_text.stroke-27"),sQuery(id+"F24.wireOp",EDGE,"E31.sketch_text.stroke-28"),sQuery(id+"F24.wireOp",EDGE,"E31.sketch_text.stroke-29"),sQuery(id+"F24.wireOp",EDGE,"E31.sketch_text.stroke-30")])]}),"instanceName":"1"});
            var Q19;
            Q19=makeQuery(id+"F26.opPattern","COPY",BODY,{"derivedFrom":makeQuery(id+"F25.opExtrude","SWEPT_BODY",BODY,{"disambiguationData":[OSD([sQuery(id+"F24.wireOp",EDGE,"E32.sketch_text.stroke-0"),sQuery(id+"F24.wireOp",EDGE,"E32.sketch_text.stroke-1"),sQuery(id+"F24.wireOp",EDGE,"E32.sketch_text.stroke-2"),sQuery(id+"F24.wireOp",EDGE,"E32.sketch_text.stroke-3"),sQuery(id+"F24.wireOp",EDGE,"E32.sketch_text.stroke-4"),sQuery(id+"F24.wireOp",EDGE,"E32.sketch_text.stroke-5"),sQuery(id+"F24.wireOp",EDGE,"E32.sketch_text.stroke-6"),sQuery(id+"F24.wireOp",EDGE,"E32.sketch_text.stroke-7"),sQuery(id+"F24.wireOp",EDGE,"E32.sketch_text.stroke-8"),sQuery(id+"F24.wireOp",EDGE,"E32.sketch_text.stroke-9"),sQuery(id+"F24.wireOp",EDGE,"E32.sketch_text.stroke-10"),sQuery(id+"F24.wireOp",EDGE,"E32.sketch_text.stroke-11"),sQuery(id+"F24.wireOp",EDGE,"E32.sketch_text.stroke-12"),sQuery(id+"F24.wireOp",EDGE,"E32.sketch_text.stroke-13"),sQuery(id+"F24.wireOp",EDGE,"E32.sketch_text.stroke-14"),sQuery(id+"F24.wireOp",EDGE,"E32.sketch_text.stroke-15"),sQuery(id+"F24.wireOp",EDGE,"E32.sketch_text.stroke-16"),sQuery(id+"F24.wireOp",EDGE,"E32.sketch_text.stroke-17"),sQuery(id+"F24.wireOp",EDGE,"E32.sketch_text.stroke-18"),sQuery(id+"F24.wireOp",EDGE,"E32.sketch_text.stroke-19"),sQuery(id+"F24.wireOp",EDGE,"E32.sketch_text.stroke-20"),sQuery(id+"F24.wireOp",EDGE,"E32.sketch_text.stroke-21"),sQuery(id+"F24.wireOp",EDGE,"E32.sketch_text.stroke-22"),sQuery(id+"F24.wireOp",EDGE,"E32.sketch_text.stroke-23"),sQuery(id+"F24.wireOp",EDGE,"E32.sketch_text.stroke-24"),sQuery(id+"F24.wireOp",EDGE,"E32.sketch_text.stroke-25")])]}),"instanceName":"1"});
            var Q20;
            Q20=makeQuery(id+"F26.opPattern","COPY",BODY,{"derivedFrom":makeQuery(id+"F25.opExtrude","SWEPT_BODY",BODY,{"disambiguationData":[OSD([sQuery(id+"F24.wireOp",EDGE,"E33.sketch_text.stroke-0"),sQuery(id+"F24.wireOp",EDGE,"E33.sketch_text.stroke-1"),sQuery(id+"F24.wireOp",EDGE,"E33.sketch_text.stroke-2"),sQuery(id+"F24.wireOp",EDGE,"E33.sketch_text.stroke-3"),sQuery(id+"F24.wireOp",EDGE,"E33.sketch_text.stroke-4"),sQuery(id+"F24.wireOp",EDGE,"E33.sketch_text.stroke-5"),sQuery(id+"F24.wireOp",EDGE,"E33.sketch_text.stroke-6"),sQuery(id+"F24.wireOp",EDGE,"E33.sketch_text.stroke-7"),sQuery(id+"F24.wireOp",EDGE,"E33.sketch_text.stroke-8")])]}),"instanceName":"1"});
            var Q21;
            Q21=makeQuery(id+"F26.opPattern","COPY",BODY,{"derivedFrom":makeQuery(id+"F25.opExtrude","SWEPT_BODY",BODY,{"disambiguationData":[OSD([sQuery(id+"F24.wireOp",EDGE,"E33.sketch_text.stroke-9"),sQuery(id+"F24.wireOp",EDGE,"E33.sketch_text.stroke-10"),sQuery(id+"F24.wireOp",EDGE,"E33.sketch_text.stroke-11"),sQuery(id+"F24.wireOp",EDGE,"E33.sketch_text.stroke-12"),sQuery(id+"F24.wireOp",EDGE,"E33.sketch_text.stroke-13"),sQuery(id+"F24.wireOp",EDGE,"E33.sketch_text.stroke-14"),sQuery(id+"F24.wireOp",EDGE,"E33.sketch_text.stroke-15"),sQuery(id+"F24.wireOp",EDGE,"E33.sketch_text.stroke-16"),sQuery(id+"F24.wireOp",EDGE,"E33.sketch_text.stroke-17"),sQuery(id+"F24.wireOp",EDGE,"E33.sketch_text.stroke-18"),sQuery(id+"F24.wireOp",EDGE,"E33.sketch_text.stroke-19"),sQuery(id+"F24.wireOp",EDGE,"E33.sketch_text.stroke-20"),sQuery(id+"F24.wireOp",EDGE,"E33.sketch_text.stroke-21"),sQuery(id+"F24.wireOp",EDGE,"E33.sketch_text.stroke-22"),sQuery(id+"F24.wireOp",EDGE,"E33.sketch_text.stroke-23"),sQuery(id+"F24.wireOp",EDGE,"E33.sketch_text.stroke-24")])]}),"instanceName":"1"});
            var Q22;
            Q22=makeQuery(id+"F26.opPattern","COPY",BODY,{"derivedFrom":makeQuery(id+"F25.opExtrude","SWEPT_BODY",BODY,{"disambiguationData":[OSD([sQuery(id+"F24.wireOp",EDGE,"E34.bottom"),sQuery(id+"F24.wireOp",EDGE,"E34.top"),sQuery(id+"F24.wireOp",EDGE,"E34.left"),sQuery(id+"F24.wireOp",EDGE,"E34.right")])]}),"instanceName":"1"});
            var Q23;
            Q23=makeQuery(id+"F26.opPattern","COPY",BODY,{"derivedFrom":makeQuery(id+"F25.opExtrude","SWEPT_BODY",BODY,{"disambiguationData":[OSD([sQuery(id+"F24.wireOp",EDGE,"E36.1.0.0"),sQuery(id+"F24.wireOp",EDGE,"E36.1.0.1"),sQuery(id+"F24.wireOp",EDGE,"E36.1.0.2"),sQuery(id+"F24.wireOp",EDGE,"E36.1.0.3")])]}),"instanceName":"1"});
            var Q24;
            Q24=makeQuery(id+"F26.opPattern","COPY",BODY,{"derivedFrom":makeQuery(id+"F25.opExtrude","SWEPT_BODY",BODY,{"disambiguationData":[OSD([sQuery(id+"F24.wireOp",EDGE,"E36.2.0.0"),sQuery(id+"F24.wireOp",EDGE,"E36.2.0.1"),sQuery(id+"F24.wireOp",EDGE,"E36.2.0.2"),sQuery(id+"F24.wireOp",EDGE,"E36.2.0.3")])]}),"instanceName":"1"});
            var Q25;
            Q25=makeQuery(id+"F26.opPattern","COPY",BODY,{"derivedFrom":makeQuery(id+"F25.opExtrude","SWEPT_BODY",BODY,{"disambiguationData":[OSD([sQuery(id+"F24.wireOp",EDGE,"E36.3.0.0"),sQuery(id+"F24.wireOp",EDGE,"E36.3.0.1"),sQuery(id+"F24.wireOp",EDGE,"E36.3.0.2"),sQuery(id+"F24.wireOp",EDGE,"E36.3.0.3")])]}),"instanceName":"1"});
            var Q26;
            Q26=makeQuery(id+"F26.opPattern","COPY",BODY,{"derivedFrom":makeQuery(id+"F25.opExtrude","SWEPT_BODY",BODY,{"disambiguationData":[OSD([sQuery(id+"F24.wireOp",EDGE,"E36.4.0.0"),sQuery(id+"F24.wireOp",EDGE,"E36.4.0.1"),sQuery(id+"F24.wireOp",EDGE,"E36.4.0.2"),sQuery(id+"F24.wireOp",EDGE,"E36.4.0.3")])]}),"instanceName":"1"});
            var Q27;
            Q27=makeQuery(id+"F26.opPattern","COPY",BODY,{"derivedFrom":makeQuery(id+"F25.opExtrude","SWEPT_BODY",BODY,{"disambiguationData":[OSD([sQuery(id+"F24.wireOp",EDGE,"E36.5.0.0"),sQuery(id+"F24.wireOp",EDGE,"E36.5.0.1"),sQuery(id+"F24.wireOp",EDGE,"E36.5.0.2"),sQuery(id+"F24.wireOp",EDGE,"E36.5.0.3")])]}),"instanceName":"1"});
            var Q28;
            Q28=makeQuery(id+"F26.opPattern","COPY",BODY,{"derivedFrom":makeQuery(id+"F25.opExtrude","SWEPT_BODY",BODY,{"disambiguationData":[OSD([sQuery(id+"F24.wireOp",EDGE,"E36.6.0.0"),sQuery(id+"F24.wireOp",EDGE,"E36.6.0.1"),sQuery(id+"F24.wireOp",EDGE,"E36.6.0.2"),sQuery(id+"F24.wireOp",EDGE,"E36.6.0.3")])]}),"instanceName":"1"});
            var Q29;
            Q29=makeQuery(id+"F26.opPattern","COPY",BODY,{"derivedFrom":makeQuery(id+"F25.opExtrude","SWEPT_BODY",BODY,{"disambiguationData":[OSD([sQuery(id+"F24.wireOp",EDGE,"E36.7.0.0"),sQuery(id+"F24.wireOp",EDGE,"E36.7.0.1"),sQuery(id+"F24.wireOp",EDGE,"E36.7.0.2"),sQuery(id+"F24.wireOp",EDGE,"E36.7.0.3")])]}),"instanceName":"1"});
            var Q30;
            Q30=makeQuery(id+"F26.opPattern","COPY",BODY,{"derivedFrom":makeQuery(id+"F25.opExtrude","SWEPT_BODY",BODY,{"disambiguationData":[OSD([sQuery(id+"F24.wireOp",EDGE,"E36.8.0.0"),sQuery(id+"F24.wireOp",EDGE,"E36.8.0.1"),sQuery(id+"F24.wireOp",EDGE,"E36.8.0.2"),sQuery(id+"F24.wireOp",EDGE,"E36.8.0.3")])]}),"instanceName":"1"});
            var Q31;
            Q31=makeQuery(id+"F26.opPattern","COPY",BODY,{"derivedFrom":makeQuery(id+"F25.opExtrude","SWEPT_BODY",BODY,{"disambiguationData":[OSD([sQuery(id+"F24.wireOp",EDGE,"E36.9.0.0"),sQuery(id+"F24.wireOp",EDGE,"E36.9.0.1"),sQuery(id+"F24.wireOp",EDGE,"E36.9.0.2"),sQuery(id+"F24.wireOp",EDGE,"E36.9.0.3")])]}),"instanceName":"1"});
            var Q32;
            Q32=sQuery(id+"F12.wireOp",EDGE,"E11");
            circularPattern(context, id + "F39", {"entities" : qUnion([Q0, Q1, Q2, Q3, Q4, Q5, Q6, Q7, Q8, Q9, Q10, Q11, Q12, Q13, Q14, Q15, Q16, Q17, Q18, Q19, Q20, Q21, Q22, Q23, Q24, Q25, Q26, Q27, Q28, Q29, Q30, Q31]), "axis" : qUnion([Q32]), "angle" : 360 * degree, "instanceCount" : 4, "equalSpace" : true});
        }
    });
